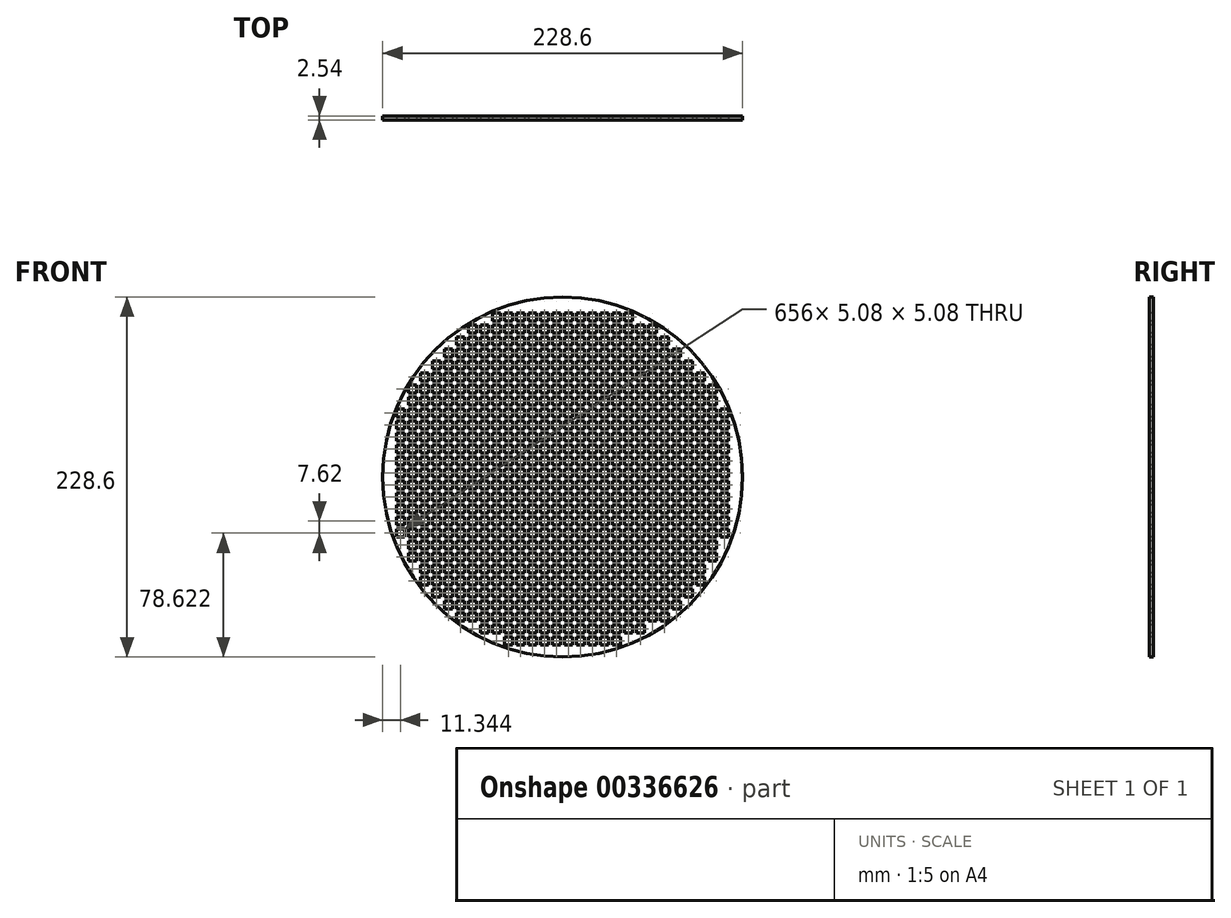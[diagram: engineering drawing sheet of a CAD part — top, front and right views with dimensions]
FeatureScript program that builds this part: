
annotation { "Feature Type Name" : "Feature", "Feature Type Description" : "" }
export const myFeature = defineFeature(function(context is Context, id is Id, definition is map)
    precondition{}
    {
        {
            var Q0;
            Q0=qCreatedBy(makeId("Front.planeOp"),FACE);
            var sketch = newSketch(context, id + "F0", { "sketchPlane" : qUnion([Q0])});
            skCircle(sketch, "E0", {"center": v(0, 0) * mm, "radius": 114.3 * mm});
            skSolve(sketch);
        }
        {
            var Q0;
            Q0=makeQuery(id+"F0.imprint","IMPRINT",FACE,{"disambiguationData":[TD([[makeQuery(id+"F0.imprint","IMPRINT",EDGE,{"derivedFrom":sQuery(id+"F0.wireOp",EDGE,"E0")}),1.0]])]});
            extrude(context, id + "F1", {"entities" : qUnion([Q0]), "depth" : 2.54 * mm});
        }
        {
            var Q0;
            Q0=makeQuery(id+"F1.opExtrude","CAP_FACE",FACE,{"disambiguationData":[OSD([sQuery(id+"F0.wireOp",EDGE,"E0")])],"isStart":false});
            var sketch = newSketch(context, id + "F2", { "sketchPlane" : qUnion([Q0])});
            skLineSegment(sketch, "E1.bottom", {"start": v(-67.4, 81.17) * mm, "end": v(-62.32, 81.17) * mm});
            skLineSegment(sketch, "E1.top", {"start": v(-67.4, 76.09) * mm, "end": v(-62.32, 76.09) * mm});
            skLineSegment(sketch, "E1.left", {"start": v(-67.4, 81.17) * mm, "end": v(-67.4, 76.09) * mm});
            skLineSegment(sketch, "E1.right", {"start": v(-62.32, 81.17) * mm, "end": v(-62.32, 76.09) * mm});
            skLineSegment(sketch, "E2.0.1.0", {"start": v(-67.4, 73.55) * mm, "end": v(-62.32, 73.55) * mm});
            skLineSegment(sketch, "E2.0.1.1", {"start": v(-67.4, 68.47) * mm, "end": v(-62.32, 68.47) * mm});
            skLineSegment(sketch, "E2.0.1.2", {"start": v(-67.4, 73.55) * mm, "end": v(-67.4, 68.47) * mm});
            skLineSegment(sketch, "E2.0.1.3", {"start": v(-62.32, 73.55) * mm, "end": v(-62.32, 68.47) * mm});
            skLineSegment(sketch, "E2.0.2.0", {"start": v(-67.4, 65.93) * mm, "end": v(-62.32, 65.93) * mm});
            skLineSegment(sketch, "E2.0.2.1", {"start": v(-67.4, 60.85) * mm, "end": v(-62.32, 60.85) * mm});
            skLineSegment(sketch, "E2.0.2.2", {"start": v(-67.4, 65.93) * mm, "end": v(-67.4, 60.85) * mm});
            skLineSegment(sketch, "E2.0.2.3", {"start": v(-62.32, 65.93) * mm, "end": v(-62.32, 60.85) * mm});
            skLineSegment(sketch, "E2.0.3.0", {"start": v(-67.4, 58.3) * mm, "end": v(-62.32, 58.3) * mm});
            skLineSegment(sketch, "E2.0.3.1", {"start": v(-67.4, 53.23) * mm, "end": v(-62.32, 53.23) * mm});
            skLineSegment(sketch, "E2.0.3.2", {"start": v(-67.4, 58.3) * mm, "end": v(-67.4, 53.23) * mm});
            skLineSegment(sketch, "E2.0.3.3", {"start": v(-62.32, 58.3) * mm, "end": v(-62.32, 53.23) * mm});
            skLineSegment(sketch, "E2.0.4.0", {"start": v(-67.4, 50.69) * mm, "end": v(-62.32, 50.69) * mm});
            skLineSegment(sketch, "E2.0.4.1", {"start": v(-67.4, 45.6) * mm, "end": v(-62.32, 45.6) * mm});
            skLineSegment(sketch, "E2.0.4.2", {"start": v(-67.4, 50.69) * mm, "end": v(-67.4, 45.6) * mm});
            skLineSegment(sketch, "E2.0.4.3", {"start": v(-62.32, 50.69) * mm, "end": v(-62.32, 45.6) * mm});
            skLineSegment(sketch, "E2.0.5.0", {"start": v(-67.4, 43.07) * mm, "end": v(-62.32, 43.07) * mm});
            skLineSegment(sketch, "E2.0.5.1", {"start": v(-67.4, 37.99) * mm, "end": v(-62.32, 37.99) * mm});
            skLineSegment(sketch, "E2.0.5.2", {"start": v(-67.4, 43.07) * mm, "end": v(-67.4, 37.99) * mm});
            skLineSegment(sketch, "E2.0.5.3", {"start": v(-62.32, 43.07) * mm, "end": v(-62.32, 37.99) * mm});
            skLineSegment(sketch, "E2.0.6.0", {"start": v(-67.4, 35.45) * mm, "end": v(-62.32, 35.45) * mm});
            skLineSegment(sketch, "E2.0.6.1", {"start": v(-67.4, 30.37) * mm, "end": v(-62.32, 30.37) * mm});
            skLineSegment(sketch, "E2.0.6.2", {"start": v(-67.4, 35.45) * mm, "end": v(-67.4, 30.37) * mm});
            skLineSegment(sketch, "E2.0.6.3", {"start": v(-62.32, 35.45) * mm, "end": v(-62.32, 30.37) * mm});
            skLineSegment(sketch, "E2.0.7.0", {"start": v(-67.4, 27.83) * mm, "end": v(-62.32, 27.83) * mm});
            skLineSegment(sketch, "E2.0.7.1", {"start": v(-67.4, 22.75) * mm, "end": v(-62.32, 22.75) * mm});
            skLineSegment(sketch, "E2.0.7.2", {"start": v(-67.4, 27.83) * mm, "end": v(-67.4, 22.75) * mm});
            skLineSegment(sketch, "E2.0.7.3", {"start": v(-62.32, 27.83) * mm, "end": v(-62.32, 22.75) * mm});
            skLineSegment(sketch, "E2.0.8.0", {"start": v(-67.4, 20.2) * mm, "end": v(-62.32, 20.2) * mm});
            skLineSegment(sketch, "E2.0.8.1", {"start": v(-67.4, 15.13) * mm, "end": v(-62.32, 15.13) * mm});
            skLineSegment(sketch, "E2.0.8.2", {"start": v(-67.4, 20.2) * mm, "end": v(-67.4, 15.13) * mm});
            skLineSegment(sketch, "E2.0.8.3", {"start": v(-62.32, 20.2) * mm, "end": v(-62.32, 15.13) * mm});
            skLineSegment(sketch, "E2.0.9.0", {"start": v(-67.4, 12.59) * mm, "end": v(-62.32, 12.59) * mm});
            skLineSegment(sketch, "E2.0.9.1", {"start": v(-67.4, 7.5) * mm, "end": v(-62.32, 7.5) * mm});
            skLineSegment(sketch, "E2.0.9.2", {"start": v(-67.4, 12.59) * mm, "end": v(-67.4, 7.5) * mm});
            skLineSegment(sketch, "E2.0.9.3", {"start": v(-62.32, 12.59) * mm, "end": v(-62.32, 7.5) * mm});
            skLineSegment(sketch, "E2.0.10.0", {"start": v(-67.4, 4.97) * mm, "end": v(-62.32, 4.97) * mm});
            skLineSegment(sketch, "E2.0.10.1", {"start": v(-67.4, -0.11) * mm, "end": v(-62.32, -0.11) * mm});
            skLineSegment(sketch, "E2.0.10.2", {"start": v(-67.4, 4.97) * mm, "end": v(-67.4, -0.11) * mm});
            skLineSegment(sketch, "E2.0.10.3", {"start": v(-62.32, 4.97) * mm, "end": v(-62.32, -0.11) * mm});
            skLineSegment(sketch, "E2.0.11.0", {"start": v(-67.4, -2.65) * mm, "end": v(-62.32, -2.65) * mm});
            skLineSegment(sketch, "E2.0.11.1", {"start": v(-67.4, -7.73) * mm, "end": v(-62.32, -7.73) * mm});
            skLineSegment(sketch, "E2.0.11.2", {"start": v(-67.4, -2.65) * mm, "end": v(-67.4, -7.73) * mm});
            skLineSegment(sketch, "E2.0.11.3", {"start": v(-62.32, -2.65) * mm, "end": v(-62.32, -7.73) * mm});
            skLineSegment(sketch, "E2.0.12.0", {"start": v(-67.4, -10.27) * mm, "end": v(-62.32, -10.27) * mm});
            skLineSegment(sketch, "E2.0.12.1", {"start": v(-67.4, -15.35) * mm, "end": v(-62.32, -15.35) * mm});
            skLineSegment(sketch, "E2.0.12.2", {"start": v(-67.4, -10.27) * mm, "end": v(-67.4, -15.35) * mm});
            skLineSegment(sketch, "E2.0.12.3", {"start": v(-62.32, -10.27) * mm, "end": v(-62.32, -15.35) * mm});
            skLineSegment(sketch, "E2.0.13.0", {"start": v(-67.4, -17.9) * mm, "end": v(-62.32, -17.9) * mm});
            skLineSegment(sketch, "E2.0.13.1", {"start": v(-67.4, -22.97) * mm, "end": v(-62.32, -22.97) * mm});
            skLineSegment(sketch, "E2.0.13.2", {"start": v(-67.4, -17.9) * mm, "end": v(-67.4, -22.97) * mm});
            skLineSegment(sketch, "E2.0.13.3", {"start": v(-62.32, -17.9) * mm, "end": v(-62.32, -22.97) * mm});
            skLineSegment(sketch, "E2.0.14.0", {"start": v(-67.4, -25.51) * mm, "end": v(-62.32, -25.51) * mm});
            skLineSegment(sketch, "E2.0.14.1", {"start": v(-67.4, -30.6) * mm, "end": v(-62.32, -30.6) * mm});
            skLineSegment(sketch, "E2.0.14.2", {"start": v(-67.4, -25.51) * mm, "end": v(-67.4, -30.6) * mm});
            skLineSegment(sketch, "E2.0.14.3", {"start": v(-62.32, -25.51) * mm, "end": v(-62.32, -30.6) * mm});
            skLineSegment(sketch, "E2.0.15.0", {"start": v(-67.4, -33.13) * mm, "end": v(-62.32, -33.13) * mm});
            skLineSegment(sketch, "E2.0.15.1", {"start": v(-67.4, -38.21) * mm, "end": v(-62.32, -38.21) * mm});
            skLineSegment(sketch, "E2.0.15.2", {"start": v(-67.4, -33.13) * mm, "end": v(-67.4, -38.21) * mm});
            skLineSegment(sketch, "E2.0.15.3", {"start": v(-62.32, -33.13) * mm, "end": v(-62.32, -38.21) * mm});
            skLineSegment(sketch, "E2.0.16.0", {"start": v(-67.4, -40.75) * mm, "end": v(-62.32, -40.75) * mm});
            skLineSegment(sketch, "E2.0.16.1", {"start": v(-67.4, -45.83) * mm, "end": v(-62.32, -45.83) * mm});
            skLineSegment(sketch, "E2.0.16.2", {"start": v(-67.4, -40.75) * mm, "end": v(-67.4, -45.83) * mm});
            skLineSegment(sketch, "E2.0.16.3", {"start": v(-62.32, -40.75) * mm, "end": v(-62.32, -45.83) * mm});
            skLineSegment(sketch, "E2.0.17.0", {"start": v(-67.4, -48.37) * mm, "end": v(-62.32, -48.37) * mm});
            skLineSegment(sketch, "E2.0.17.1", {"start": v(-67.4, -53.45) * mm, "end": v(-62.32, -53.45) * mm});
            skLineSegment(sketch, "E2.0.17.2", {"start": v(-67.4, -48.37) * mm, "end": v(-67.4, -53.45) * mm});
            skLineSegment(sketch, "E2.0.17.3", {"start": v(-62.32, -48.37) * mm, "end": v(-62.32, -53.45) * mm});
            skLineSegment(sketch, "E2.0.18.0", {"start": v(-67.4, -56) * mm, "end": v(-62.32, -56) * mm});
            skLineSegment(sketch, "E2.0.18.1", {"start": v(-67.4, -61.07) * mm, "end": v(-62.32, -61.07) * mm});
            skLineSegment(sketch, "E2.0.18.2", {"start": v(-67.4, -56) * mm, "end": v(-67.4, -61.07) * mm});
            skLineSegment(sketch, "E2.0.18.3", {"start": v(-62.32, -56) * mm, "end": v(-62.32, -61.07) * mm});
            skLineSegment(sketch, "E2.0.19.0", {"start": v(-67.4, -63.61) * mm, "end": v(-62.32, -63.61) * mm});
            skLineSegment(sketch, "E2.0.19.1", {"start": v(-67.4, -68.7) * mm, "end": v(-62.32, -68.7) * mm});
            skLineSegment(sketch, "E2.0.19.2", {"start": v(-67.4, -63.61) * mm, "end": v(-67.4, -68.7) * mm});
            skLineSegment(sketch, "E2.0.19.3", {"start": v(-62.32, -63.61) * mm, "end": v(-62.32, -68.7) * mm});
            skLineSegment(sketch, "E2.0.20.0", {"start": v(-67.4, -71.23) * mm, "end": v(-62.32, -71.23) * mm});
            skLineSegment(sketch, "E2.0.20.1", {"start": v(-67.4, -76.31) * mm, "end": v(-62.32, -76.31) * mm});
            skLineSegment(sketch, "E2.0.20.2", {"start": v(-67.4, -71.23) * mm, "end": v(-67.4, -76.31) * mm});
            skLineSegment(sketch, "E2.0.20.3", {"start": v(-62.32, -71.23) * mm, "end": v(-62.32, -76.31) * mm});
            skLineSegment(sketch, "E2.0.21.0", {"start": v(-67.4, -78.85) * mm, "end": v(-62.32, -78.85) * mm});
            skLineSegment(sketch, "E2.0.21.1", {"start": v(-67.4, -83.93) * mm, "end": v(-62.32, -83.93) * mm});
            skLineSegment(sketch, "E2.0.21.2", {"start": v(-67.4, -78.85) * mm, "end": v(-67.4, -83.93) * mm});
            skLineSegment(sketch, "E2.0.21.3", {"start": v(-62.32, -78.85) * mm, "end": v(-62.32, -83.93) * mm});
            skLineSegment(sketch, "E2.1.0.0", {"start": v(-59.78, 81.17) * mm, "end": v(-54.7, 81.17) * mm});
            skLineSegment(sketch, "E2.1.0.1", {"start": v(-59.78, 76.09) * mm, "end": v(-54.7, 76.09) * mm});
            skLineSegment(sketch, "E2.1.0.2", {"start": v(-59.78, 81.17) * mm, "end": v(-59.78, 76.09) * mm});
            skLineSegment(sketch, "E2.1.0.3", {"start": v(-54.7, 81.17) * mm, "end": v(-54.7, 76.09) * mm});
            skLineSegment(sketch, "E2.1.1.0", {"start": v(-59.78, 73.55) * mm, "end": v(-54.7, 73.55) * mm});
            skLineSegment(sketch, "E2.1.1.1", {"start": v(-59.78, 68.47) * mm, "end": v(-54.7, 68.47) * mm});
            skLineSegment(sketch, "E2.1.1.2", {"start": v(-59.78, 73.55) * mm, "end": v(-59.78, 68.47) * mm});
            skLineSegment(sketch, "E2.1.1.3", {"start": v(-54.7, 73.55) * mm, "end": v(-54.7, 68.47) * mm});
            skLineSegment(sketch, "E2.1.2.0", {"start": v(-59.78, 65.93) * mm, "end": v(-54.7, 65.93) * mm});
            skLineSegment(sketch, "E2.1.2.1", {"start": v(-59.78, 60.85) * mm, "end": v(-54.7, 60.85) * mm});
            skLineSegment(sketch, "E2.1.2.2", {"start": v(-59.78, 65.93) * mm, "end": v(-59.78, 60.85) * mm});
            skLineSegment(sketch, "E2.1.2.3", {"start": v(-54.7, 65.93) * mm, "end": v(-54.7, 60.85) * mm});
            skLineSegment(sketch, "E2.1.3.0", {"start": v(-59.78, 58.3) * mm, "end": v(-54.7, 58.3) * mm});
            skLineSegment(sketch, "E2.1.3.1", {"start": v(-59.78, 53.23) * mm, "end": v(-54.7, 53.23) * mm});
            skLineSegment(sketch, "E2.1.3.2", {"start": v(-59.78, 58.3) * mm, "end": v(-59.78, 53.23) * mm});
            skLineSegment(sketch, "E2.1.3.3", {"start": v(-54.7, 58.3) * mm, "end": v(-54.7, 53.23) * mm});
            skLineSegment(sketch, "E2.1.4.0", {"start": v(-59.78, 50.69) * mm, "end": v(-54.7, 50.69) * mm});
            skLineSegment(sketch, "E2.1.4.1", {"start": v(-59.78, 45.6) * mm, "end": v(-54.7, 45.6) * mm});
            skLineSegment(sketch, "E2.1.4.2", {"start": v(-59.78, 50.69) * mm, "end": v(-59.78, 45.6) * mm});
            skLineSegment(sketch, "E2.1.4.3", {"start": v(-54.7, 50.69) * mm, "end": v(-54.7, 45.6) * mm});
            skLineSegment(sketch, "E2.1.5.0", {"start": v(-59.78, 43.07) * mm, "end": v(-54.7, 43.07) * mm});
            skLineSegment(sketch, "E2.1.5.1", {"start": v(-59.78, 37.99) * mm, "end": v(-54.7, 37.99) * mm});
            skLineSegment(sketch, "E2.1.5.2", {"start": v(-59.78, 43.07) * mm, "end": v(-59.78, 37.99) * mm});
            skLineSegment(sketch, "E2.1.5.3", {"start": v(-54.7, 43.07) * mm, "end": v(-54.7, 37.99) * mm});
            skLineSegment(sketch, "E2.1.6.0", {"start": v(-59.78, 35.45) * mm, "end": v(-54.7, 35.45) * mm});
            skLineSegment(sketch, "E2.1.6.1", {"start": v(-59.78, 30.37) * mm, "end": v(-54.7, 30.37) * mm});
            skLineSegment(sketch, "E2.1.6.2", {"start": v(-59.78, 35.45) * mm, "end": v(-59.78, 30.37) * mm});
            skLineSegment(sketch, "E2.1.6.3", {"start": v(-54.7, 35.45) * mm, "end": v(-54.7, 30.37) * mm});
            skLineSegment(sketch, "E2.1.7.0", {"start": v(-59.78, 27.83) * mm, "end": v(-54.7, 27.83) * mm});
            skLineSegment(sketch, "E2.1.7.1", {"start": v(-59.78, 22.75) * mm, "end": v(-54.7, 22.75) * mm});
            skLineSegment(sketch, "E2.1.7.2", {"start": v(-59.78, 27.83) * mm, "end": v(-59.78, 22.75) * mm});
            skLineSegment(sketch, "E2.1.7.3", {"start": v(-54.7, 27.83) * mm, "end": v(-54.7, 22.75) * mm});
            skLineSegment(sketch, "E2.1.8.0", {"start": v(-59.78, 20.2) * mm, "end": v(-54.7, 20.2) * mm});
            skLineSegment(sketch, "E2.1.8.1", {"start": v(-59.78, 15.13) * mm, "end": v(-54.7, 15.13) * mm});
            skLineSegment(sketch, "E2.1.8.2", {"start": v(-59.78, 20.2) * mm, "end": v(-59.78, 15.13) * mm});
            skLineSegment(sketch, "E2.1.8.3", {"start": v(-54.7, 20.2) * mm, "end": v(-54.7, 15.13) * mm});
            skLineSegment(sketch, "E2.1.9.0", {"start": v(-59.78, 12.59) * mm, "end": v(-54.7, 12.59) * mm});
            skLineSegment(sketch, "E2.1.9.1", {"start": v(-59.78, 7.5) * mm, "end": v(-54.7, 7.5) * mm});
            skLineSegment(sketch, "E2.1.9.2", {"start": v(-59.78, 12.59) * mm, "end": v(-59.78, 7.5) * mm});
            skLineSegment(sketch, "E2.1.9.3", {"start": v(-54.7, 12.59) * mm, "end": v(-54.7, 7.5) * mm});
            skLineSegment(sketch, "E2.1.10.0", {"start": v(-59.78, 4.97) * mm, "end": v(-54.7, 4.97) * mm});
            skLineSegment(sketch, "E2.1.10.1", {"start": v(-59.78, -0.11) * mm, "end": v(-54.7, -0.11) * mm});
            skLineSegment(sketch, "E2.1.10.2", {"start": v(-59.78, 4.97) * mm, "end": v(-59.78, -0.11) * mm});
            skLineSegment(sketch, "E2.1.10.3", {"start": v(-54.7, 4.97) * mm, "end": v(-54.7, -0.11) * mm});
            skLineSegment(sketch, "E2.1.11.0", {"start": v(-59.78, -2.65) * mm, "end": v(-54.7, -2.65) * mm});
            skLineSegment(sketch, "E2.1.11.1", {"start": v(-59.78, -7.73) * mm, "end": v(-54.7, -7.73) * mm});
            skLineSegment(sketch, "E2.1.11.2", {"start": v(-59.78, -2.65) * mm, "end": v(-59.78, -7.73) * mm});
            skLineSegment(sketch, "E2.1.11.3", {"start": v(-54.7, -2.65) * mm, "end": v(-54.7, -7.73) * mm});
            skLineSegment(sketch, "E2.1.12.0", {"start": v(-59.78, -10.27) * mm, "end": v(-54.7, -10.27) * mm});
            skLineSegment(sketch, "E2.1.12.1", {"start": v(-59.78, -15.35) * mm, "end": v(-54.7, -15.35) * mm});
            skLineSegment(sketch, "E2.1.12.2", {"start": v(-59.78, -10.27) * mm, "end": v(-59.78, -15.35) * mm});
            skLineSegment(sketch, "E2.1.12.3", {"start": v(-54.7, -10.27) * mm, "end": v(-54.7, -15.35) * mm});
            skLineSegment(sketch, "E2.1.13.0", {"start": v(-59.78, -17.9) * mm, "end": v(-54.7, -17.9) * mm});
            skLineSegment(sketch, "E2.1.13.1", {"start": v(-59.78, -22.97) * mm, "end": v(-54.7, -22.97) * mm});
            skLineSegment(sketch, "E2.1.13.2", {"start": v(-59.78, -17.9) * mm, "end": v(-59.78, -22.97) * mm});
            skLineSegment(sketch, "E2.1.13.3", {"start": v(-54.7, -17.9) * mm, "end": v(-54.7, -22.97) * mm});
            skLineSegment(sketch, "E2.1.14.0", {"start": v(-59.78, -25.51) * mm, "end": v(-54.7, -25.51) * mm});
            skLineSegment(sketch, "E2.1.14.1", {"start": v(-59.78, -30.6) * mm, "end": v(-54.7, -30.6) * mm});
            skLineSegment(sketch, "E2.1.14.2", {"start": v(-59.78, -25.51) * mm, "end": v(-59.78, -30.6) * mm});
            skLineSegment(sketch, "E2.1.14.3", {"start": v(-54.7, -25.51) * mm, "end": v(-54.7, -30.6) * mm});
            skLineSegment(sketch, "E2.1.15.0", {"start": v(-59.78, -33.13) * mm, "end": v(-54.7, -33.13) * mm});
            skLineSegment(sketch, "E2.1.15.1", {"start": v(-59.78, -38.21) * mm, "end": v(-54.7, -38.21) * mm});
            skLineSegment(sketch, "E2.1.15.2", {"start": v(-59.78, -33.13) * mm, "end": v(-59.78, -38.21) * mm});
            skLineSegment(sketch, "E2.1.15.3", {"start": v(-54.7, -33.13) * mm, "end": v(-54.7, -38.21) * mm});
            skLineSegment(sketch, "E2.1.16.0", {"start": v(-59.78, -40.75) * mm, "end": v(-54.7, -40.75) * mm});
            skLineSegment(sketch, "E2.1.16.1", {"start": v(-59.78, -45.83) * mm, "end": v(-54.7, -45.83) * mm});
            skLineSegment(sketch, "E2.1.16.2", {"start": v(-59.78, -40.75) * mm, "end": v(-59.78, -45.83) * mm});
            skLineSegment(sketch, "E2.1.16.3", {"start": v(-54.7, -40.75) * mm, "end": v(-54.7, -45.83) * mm});
            skLineSegment(sketch, "E2.1.17.0", {"start": v(-59.78, -48.37) * mm, "end": v(-54.7, -48.37) * mm});
            skLineSegment(sketch, "E2.1.17.1", {"start": v(-59.78, -53.45) * mm, "end": v(-54.7, -53.45) * mm});
            skLineSegment(sketch, "E2.1.17.2", {"start": v(-59.78, -48.37) * mm, "end": v(-59.78, -53.45) * mm});
            skLineSegment(sketch, "E2.1.17.3", {"start": v(-54.7, -48.37) * mm, "end": v(-54.7, -53.45) * mm});
            skLineSegment(sketch, "E2.1.18.0", {"start": v(-59.78, -56) * mm, "end": v(-54.7, -56) * mm});
            skLineSegment(sketch, "E2.1.18.1", {"start": v(-59.78, -61.07) * mm, "end": v(-54.7, -61.07) * mm});
            skLineSegment(sketch, "E2.1.18.2", {"start": v(-59.78, -56) * mm, "end": v(-59.78, -61.07) * mm});
            skLineSegment(sketch, "E2.1.18.3", {"start": v(-54.7, -56) * mm, "end": v(-54.7, -61.07) * mm});
            skLineSegment(sketch, "E2.1.19.0", {"start": v(-59.78, -63.61) * mm, "end": v(-54.7, -63.61) * mm});
            skLineSegment(sketch, "E2.1.19.1", {"start": v(-59.78, -68.7) * mm, "end": v(-54.7, -68.7) * mm});
            skLineSegment(sketch, "E2.1.19.2", {"start": v(-59.78, -63.61) * mm, "end": v(-59.78, -68.7) * mm});
            skLineSegment(sketch, "E2.1.19.3", {"start": v(-54.7, -63.61) * mm, "end": v(-54.7, -68.7) * mm});
            skLineSegment(sketch, "E2.1.20.0", {"start": v(-59.78, -71.23) * mm, "end": v(-54.7, -71.23) * mm});
            skLineSegment(sketch, "E2.1.20.1", {"start": v(-59.78, -76.31) * mm, "end": v(-54.7, -76.31) * mm});
            skLineSegment(sketch, "E2.1.20.2", {"start": v(-59.78, -71.23) * mm, "end": v(-59.78, -76.31) * mm});
            skLineSegment(sketch, "E2.1.20.3", {"start": v(-54.7, -71.23) * mm, "end": v(-54.7, -76.31) * mm});
            skLineSegment(sketch, "E2.1.21.0", {"start": v(-59.78, -78.85) * mm, "end": v(-54.7, -78.85) * mm});
            skLineSegment(sketch, "E2.1.21.1", {"start": v(-59.78, -83.93) * mm, "end": v(-54.7, -83.93) * mm});
            skLineSegment(sketch, "E2.1.21.2", {"start": v(-59.78, -78.85) * mm, "end": v(-59.78, -83.93) * mm});
            skLineSegment(sketch, "E2.1.21.3", {"start": v(-54.7, -78.85) * mm, "end": v(-54.7, -83.93) * mm});
            skLineSegment(sketch, "E2.2.0.0", {"start": v(-52.16, 81.17) * mm, "end": v(-47.08, 81.17) * mm});
            skLineSegment(sketch, "E2.2.0.1", {"start": v(-52.16, 76.09) * mm, "end": v(-47.08, 76.09) * mm});
            skLineSegment(sketch, "E2.2.0.2", {"start": v(-52.16, 81.17) * mm, "end": v(-52.16, 76.09) * mm});
            skLineSegment(sketch, "E2.2.0.3", {"start": v(-47.08, 81.17) * mm, "end": v(-47.08, 76.09) * mm});
            skLineSegment(sketch, "E2.2.1.0", {"start": v(-52.16, 73.55) * mm, "end": v(-47.08, 73.55) * mm});
            skLineSegment(sketch, "E2.2.1.1", {"start": v(-52.16, 68.47) * mm, "end": v(-47.08, 68.47) * mm});
            skLineSegment(sketch, "E2.2.1.2", {"start": v(-52.16, 73.55) * mm, "end": v(-52.16, 68.47) * mm});
            skLineSegment(sketch, "E2.2.1.3", {"start": v(-47.08, 73.55) * mm, "end": v(-47.08, 68.47) * mm});
            skLineSegment(sketch, "E2.2.2.0", {"start": v(-52.16, 65.93) * mm, "end": v(-47.08, 65.93) * mm});
            skLineSegment(sketch, "E2.2.2.1", {"start": v(-52.16, 60.85) * mm, "end": v(-47.08, 60.85) * mm});
            skLineSegment(sketch, "E2.2.2.2", {"start": v(-52.16, 65.93) * mm, "end": v(-52.16, 60.85) * mm});
            skLineSegment(sketch, "E2.2.2.3", {"start": v(-47.08, 65.93) * mm, "end": v(-47.08, 60.85) * mm});
            skLineSegment(sketch, "E2.2.3.0", {"start": v(-52.16, 58.3) * mm, "end": v(-47.08, 58.3) * mm});
            skLineSegment(sketch, "E2.2.3.1", {"start": v(-52.16, 53.23) * mm, "end": v(-47.08, 53.23) * mm});
            skLineSegment(sketch, "E2.2.3.2", {"start": v(-52.16, 58.3) * mm, "end": v(-52.16, 53.23) * mm});
            skLineSegment(sketch, "E2.2.3.3", {"start": v(-47.08, 58.3) * mm, "end": v(-47.08, 53.23) * mm});
            skLineSegment(sketch, "E2.2.4.0", {"start": v(-52.16, 50.69) * mm, "end": v(-47.08, 50.69) * mm});
            skLineSegment(sketch, "E2.2.4.1", {"start": v(-52.16, 45.6) * mm, "end": v(-47.08, 45.6) * mm});
            skLineSegment(sketch, "E2.2.4.2", {"start": v(-52.16, 50.69) * mm, "end": v(-52.16, 45.6) * mm});
            skLineSegment(sketch, "E2.2.4.3", {"start": v(-47.08, 50.69) * mm, "end": v(-47.08, 45.6) * mm});
            skLineSegment(sketch, "E2.2.5.0", {"start": v(-52.16, 43.07) * mm, "end": v(-47.08, 43.07) * mm});
            skLineSegment(sketch, "E2.2.5.1", {"start": v(-52.16, 37.99) * mm, "end": v(-47.08, 37.99) * mm});
            skLineSegment(sketch, "E2.2.5.2", {"start": v(-52.16, 43.07) * mm, "end": v(-52.16, 37.99) * mm});
            skLineSegment(sketch, "E2.2.5.3", {"start": v(-47.08, 43.07) * mm, "end": v(-47.08, 37.99) * mm});
            skLineSegment(sketch, "E2.2.6.0", {"start": v(-52.16, 35.45) * mm, "end": v(-47.08, 35.45) * mm});
            skLineSegment(sketch, "E2.2.6.1", {"start": v(-52.16, 30.37) * mm, "end": v(-47.08, 30.37) * mm});
            skLineSegment(sketch, "E2.2.6.2", {"start": v(-52.16, 35.45) * mm, "end": v(-52.16, 30.37) * mm});
            skLineSegment(sketch, "E2.2.6.3", {"start": v(-47.08, 35.45) * mm, "end": v(-47.08, 30.37) * mm});
            skLineSegment(sketch, "E2.2.7.0", {"start": v(-52.16, 27.83) * mm, "end": v(-47.08, 27.83) * mm});
            skLineSegment(sketch, "E2.2.7.1", {"start": v(-52.16, 22.75) * mm, "end": v(-47.08, 22.75) * mm});
            skLineSegment(sketch, "E2.2.7.2", {"start": v(-52.16, 27.83) * mm, "end": v(-52.16, 22.75) * mm});
            skLineSegment(sketch, "E2.2.7.3", {"start": v(-47.08, 27.83) * mm, "end": v(-47.08, 22.75) * mm});
            skLineSegment(sketch, "E2.2.8.0", {"start": v(-52.16, 20.2) * mm, "end": v(-47.08, 20.2) * mm});
            skLineSegment(sketch, "E2.2.8.1", {"start": v(-52.16, 15.13) * mm, "end": v(-47.08, 15.13) * mm});
            skLineSegment(sketch, "E2.2.8.2", {"start": v(-52.16, 20.2) * mm, "end": v(-52.16, 15.13) * mm});
            skLineSegment(sketch, "E2.2.8.3", {"start": v(-47.08, 20.2) * mm, "end": v(-47.08, 15.13) * mm});
            skLineSegment(sketch, "E2.2.9.0", {"start": v(-52.16, 12.59) * mm, "end": v(-47.08, 12.59) * mm});
            skLineSegment(sketch, "E2.2.9.1", {"start": v(-52.16, 7.5) * mm, "end": v(-47.08, 7.5) * mm});
            skLineSegment(sketch, "E2.2.9.2", {"start": v(-52.16, 12.59) * mm, "end": v(-52.16, 7.5) * mm});
            skLineSegment(sketch, "E2.2.9.3", {"start": v(-47.08, 12.59) * mm, "end": v(-47.08, 7.5) * mm});
            skLineSegment(sketch, "E2.2.10.0", {"start": v(-52.16, 4.97) * mm, "end": v(-47.08, 4.97) * mm});
            skLineSegment(sketch, "E2.2.10.1", {"start": v(-52.16, -0.11) * mm, "end": v(-47.08, -0.11) * mm});
            skLineSegment(sketch, "E2.2.10.2", {"start": v(-52.16, 4.97) * mm, "end": v(-52.16, -0.11) * mm});
            skLineSegment(sketch, "E2.2.10.3", {"start": v(-47.08, 4.97) * mm, "end": v(-47.08, -0.11) * mm});
            skLineSegment(sketch, "E2.2.11.0", {"start": v(-52.16, -2.65) * mm, "end": v(-47.08, -2.65) * mm});
            skLineSegment(sketch, "E2.2.11.1", {"start": v(-52.16, -7.73) * mm, "end": v(-47.08, -7.73) * mm});
            skLineSegment(sketch, "E2.2.11.2", {"start": v(-52.16, -2.65) * mm, "end": v(-52.16, -7.73) * mm});
            skLineSegment(sketch, "E2.2.11.3", {"start": v(-47.08, -2.65) * mm, "end": v(-47.08, -7.73) * mm});
            skLineSegment(sketch, "E2.2.12.0", {"start": v(-52.16, -10.27) * mm, "end": v(-47.08, -10.27) * mm});
            skLineSegment(sketch, "E2.2.12.1", {"start": v(-52.16, -15.35) * mm, "end": v(-47.08, -15.35) * mm});
            skLineSegment(sketch, "E2.2.12.2", {"start": v(-52.16, -10.27) * mm, "end": v(-52.16, -15.35) * mm});
            skLineSegment(sketch, "E2.2.12.3", {"start": v(-47.08, -10.27) * mm, "end": v(-47.08, -15.35) * mm});
            skLineSegment(sketch, "E2.2.13.0", {"start": v(-52.16, -17.9) * mm, "end": v(-47.08, -17.9) * mm});
            skLineSegment(sketch, "E2.2.13.1", {"start": v(-52.16, -22.97) * mm, "end": v(-47.08, -22.97) * mm});
            skLineSegment(sketch, "E2.2.13.2", {"start": v(-52.16, -17.9) * mm, "end": v(-52.16, -22.97) * mm});
            skLineSegment(sketch, "E2.2.13.3", {"start": v(-47.08, -17.9) * mm, "end": v(-47.08, -22.97) * mm});
            skLineSegment(sketch, "E2.2.14.0", {"start": v(-52.16, -25.51) * mm, "end": v(-47.08, -25.51) * mm});
            skLineSegment(sketch, "E2.2.14.1", {"start": v(-52.16, -30.6) * mm, "end": v(-47.08, -30.6) * mm});
            skLineSegment(sketch, "E2.2.14.2", {"start": v(-52.16, -25.51) * mm, "end": v(-52.16, -30.6) * mm});
            skLineSegment(sketch, "E2.2.14.3", {"start": v(-47.08, -25.51) * mm, "end": v(-47.08, -30.6) * mm});
            skLineSegment(sketch, "E2.2.15.0", {"start": v(-52.16, -33.13) * mm, "end": v(-47.08, -33.13) * mm});
            skLineSegment(sketch, "E2.2.15.1", {"start": v(-52.16, -38.21) * mm, "end": v(-47.08, -38.21) * mm});
            skLineSegment(sketch, "E2.2.15.2", {"start": v(-52.16, -33.13) * mm, "end": v(-52.16, -38.21) * mm});
            skLineSegment(sketch, "E2.2.15.3", {"start": v(-47.08, -33.13) * mm, "end": v(-47.08, -38.21) * mm});
            skLineSegment(sketch, "E2.2.16.0", {"start": v(-52.16, -40.75) * mm, "end": v(-47.08, -40.75) * mm});
            skLineSegment(sketch, "E2.2.16.1", {"start": v(-52.16, -45.83) * mm, "end": v(-47.08, -45.83) * mm});
            skLineSegment(sketch, "E2.2.16.2", {"start": v(-52.16, -40.75) * mm, "end": v(-52.16, -45.83) * mm});
            skLineSegment(sketch, "E2.2.16.3", {"start": v(-47.08, -40.75) * mm, "end": v(-47.08, -45.83) * mm});
            skLineSegment(sketch, "E2.2.17.0", {"start": v(-52.16, -48.37) * mm, "end": v(-47.08, -48.37) * mm});
            skLineSegment(sketch, "E2.2.17.1", {"start": v(-52.16, -53.45) * mm, "end": v(-47.08, -53.45) * mm});
            skLineSegment(sketch, "E2.2.17.2", {"start": v(-52.16, -48.37) * mm, "end": v(-52.16, -53.45) * mm});
            skLineSegment(sketch, "E2.2.17.3", {"start": v(-47.08, -48.37) * mm, "end": v(-47.08, -53.45) * mm});
            skLineSegment(sketch, "E2.2.18.0", {"start": v(-52.16, -56) * mm, "end": v(-47.08, -56) * mm});
            skLineSegment(sketch, "E2.2.18.1", {"start": v(-52.16, -61.07) * mm, "end": v(-47.08, -61.07) * mm});
            skLineSegment(sketch, "E2.2.18.2", {"start": v(-52.16, -56) * mm, "end": v(-52.16, -61.07) * mm});
            skLineSegment(sketch, "E2.2.18.3", {"start": v(-47.08, -56) * mm, "end": v(-47.08, -61.07) * mm});
            skLineSegment(sketch, "E2.2.19.0", {"start": v(-52.16, -63.61) * mm, "end": v(-47.08, -63.61) * mm});
            skLineSegment(sketch, "E2.2.19.1", {"start": v(-52.16, -68.7) * mm, "end": v(-47.08, -68.7) * mm});
            skLineSegment(sketch, "E2.2.19.2", {"start": v(-52.16, -63.61) * mm, "end": v(-52.16, -68.7) * mm});
            skLineSegment(sketch, "E2.2.19.3", {"start": v(-47.08, -63.61) * mm, "end": v(-47.08, -68.7) * mm});
            skLineSegment(sketch, "E2.2.20.0", {"start": v(-52.16, -71.23) * mm, "end": v(-47.08, -71.23) * mm});
            skLineSegment(sketch, "E2.2.20.1", {"start": v(-52.16, -76.31) * mm, "end": v(-47.08, -76.31) * mm});
            skLineSegment(sketch, "E2.2.20.2", {"start": v(-52.16, -71.23) * mm, "end": v(-52.16, -76.31) * mm});
            skLineSegment(sketch, "E2.2.20.3", {"start": v(-47.08, -71.23) * mm, "end": v(-47.08, -76.31) * mm});
            skLineSegment(sketch, "E2.2.21.0", {"start": v(-52.16, -78.85) * mm, "end": v(-47.08, -78.85) * mm});
            skLineSegment(sketch, "E2.2.21.1", {"start": v(-52.16, -83.93) * mm, "end": v(-47.08, -83.93) * mm});
            skLineSegment(sketch, "E2.2.21.2", {"start": v(-52.16, -78.85) * mm, "end": v(-52.16, -83.93) * mm});
            skLineSegment(sketch, "E2.2.21.3", {"start": v(-47.08, -78.85) * mm, "end": v(-47.08, -83.93) * mm});
            skLineSegment(sketch, "E2.direction1", {"start": v(-67.4, 81.17) * mm, "end": v(-59.78, 81.17) * mm, "construction": true});
            skLineSegment(sketch, "E2.direction2", {"start": v(-67.4, 81.17) * mm, "end": v(-67.4, 73.55) * mm, "construction": true});
            skLineSegment(sketch, "E3.0.3.0", {"start": v(-44.54, 81.17) * mm, "end": v(-39.46, 81.17) * mm});
            skLineSegment(sketch, "E3.3.3.0", {"start": v(-44.54, 76.09) * mm, "end": v(-39.46, 76.09) * mm});
            skLineSegment(sketch, "E3.6.3.0", {"start": v(-44.54, 81.17) * mm, "end": v(-44.54, 76.09) * mm});
            skLineSegment(sketch, "E3.9.3.0", {"start": v(-39.46, 81.17) * mm, "end": v(-39.46, 76.09) * mm});
            skLineSegment(sketch, "E3.0.3.1", {"start": v(-44.54, 73.55) * mm, "end": v(-39.46, 73.55) * mm});
            skLineSegment(sketch, "E3.3.3.1", {"start": v(-44.54, 68.47) * mm, "end": v(-39.46, 68.47) * mm});
            skLineSegment(sketch, "E3.6.3.1", {"start": v(-44.54, 73.55) * mm, "end": v(-44.54, 68.47) * mm});
            skLineSegment(sketch, "E3.9.3.1", {"start": v(-39.46, 73.55) * mm, "end": v(-39.46, 68.47) * mm});
            skLineSegment(sketch, "E3.0.3.2", {"start": v(-44.54, 65.93) * mm, "end": v(-39.46, 65.93) * mm});
            skLineSegment(sketch, "E3.3.3.2", {"start": v(-44.54, 60.85) * mm, "end": v(-39.46, 60.85) * mm});
            skLineSegment(sketch, "E3.6.3.2", {"start": v(-44.54, 65.93) * mm, "end": v(-44.54, 60.85) * mm});
            skLineSegment(sketch, "E3.9.3.2", {"start": v(-39.46, 65.93) * mm, "end": v(-39.46, 60.85) * mm});
            skLineSegment(sketch, "E3.0.3.3", {"start": v(-44.54, 58.3) * mm, "end": v(-39.46, 58.3) * mm});
            skLineSegment(sketch, "E3.3.3.3", {"start": v(-44.54, 53.23) * mm, "end": v(-39.46, 53.23) * mm});
            skLineSegment(sketch, "E3.6.3.3", {"start": v(-44.54, 58.3) * mm, "end": v(-44.54, 53.23) * mm});
            skLineSegment(sketch, "E3.9.3.3", {"start": v(-39.46, 58.3) * mm, "end": v(-39.46, 53.23) * mm});
            skLineSegment(sketch, "E3.0.3.4", {"start": v(-44.54, 50.69) * mm, "end": v(-39.46, 50.69) * mm});
            skLineSegment(sketch, "E3.3.3.4", {"start": v(-44.54, 45.6) * mm, "end": v(-39.46, 45.6) * mm});
            skLineSegment(sketch, "E3.6.3.4", {"start": v(-44.54, 50.69) * mm, "end": v(-44.54, 45.6) * mm});
            skLineSegment(sketch, "E3.9.3.4", {"start": v(-39.46, 50.69) * mm, "end": v(-39.46, 45.6) * mm});
            skLineSegment(sketch, "E3.0.3.5", {"start": v(-44.54, 43.07) * mm, "end": v(-39.46, 43.07) * mm});
            skLineSegment(sketch, "E3.3.3.5", {"start": v(-44.54, 37.99) * mm, "end": v(-39.46, 37.99) * mm});
            skLineSegment(sketch, "E3.6.3.5", {"start": v(-44.54, 43.07) * mm, "end": v(-44.54, 37.99) * mm});
            skLineSegment(sketch, "E3.9.3.5", {"start": v(-39.46, 43.07) * mm, "end": v(-39.46, 37.99) * mm});
            skLineSegment(sketch, "E3.0.3.6", {"start": v(-44.54, 35.45) * mm, "end": v(-39.46, 35.45) * mm});
            skLineSegment(sketch, "E3.3.3.6", {"start": v(-44.54, 30.37) * mm, "end": v(-39.46, 30.37) * mm});
            skLineSegment(sketch, "E3.6.3.6", {"start": v(-44.54, 35.45) * mm, "end": v(-44.54, 30.37) * mm});
            skLineSegment(sketch, "E3.9.3.6", {"start": v(-39.46, 35.45) * mm, "end": v(-39.46, 30.37) * mm});
            skLineSegment(sketch, "E3.0.3.7", {"start": v(-44.54, 27.83) * mm, "end": v(-39.46, 27.83) * mm});
            skLineSegment(sketch, "E3.3.3.7", {"start": v(-44.54, 22.75) * mm, "end": v(-39.46, 22.75) * mm});
            skLineSegment(sketch, "E3.6.3.7", {"start": v(-44.54, 27.83) * mm, "end": v(-44.54, 22.75) * mm});
            skLineSegment(sketch, "E3.9.3.7", {"start": v(-39.46, 27.83) * mm, "end": v(-39.46, 22.75) * mm});
            skLineSegment(sketch, "E3.0.3.8", {"start": v(-44.54, 20.2) * mm, "end": v(-39.46, 20.2) * mm});
            skLineSegment(sketch, "E3.3.3.8", {"start": v(-44.54, 15.13) * mm, "end": v(-39.46, 15.13) * mm});
            skLineSegment(sketch, "E3.6.3.8", {"start": v(-44.54, 20.2) * mm, "end": v(-44.54, 15.13) * mm});
            skLineSegment(sketch, "E3.9.3.8", {"start": v(-39.46, 20.2) * mm, "end": v(-39.46, 15.13) * mm});
            skLineSegment(sketch, "E3.0.3.9", {"start": v(-44.54, 12.59) * mm, "end": v(-39.46, 12.59) * mm});
            skLineSegment(sketch, "E3.3.3.9", {"start": v(-44.54, 7.5) * mm, "end": v(-39.46, 7.5) * mm});
            skLineSegment(sketch, "E3.6.3.9", {"start": v(-44.54, 12.59) * mm, "end": v(-44.54, 7.5) * mm});
            skLineSegment(sketch, "E3.9.3.9", {"start": v(-39.46, 12.59) * mm, "end": v(-39.46, 7.5) * mm});
            skLineSegment(sketch, "E3.0.3.10", {"start": v(-44.54, 4.97) * mm, "end": v(-39.46, 4.97) * mm});
            skLineSegment(sketch, "E3.3.3.10", {"start": v(-44.54, -0.11) * mm, "end": v(-39.46, -0.11) * mm});
            skLineSegment(sketch, "E3.6.3.10", {"start": v(-44.54, 4.97) * mm, "end": v(-44.54, -0.11) * mm});
            skLineSegment(sketch, "E3.9.3.10", {"start": v(-39.46, 4.97) * mm, "end": v(-39.46, -0.11) * mm});
            skLineSegment(sketch, "E3.0.3.11", {"start": v(-44.54, -2.65) * mm, "end": v(-39.46, -2.65) * mm});
            skLineSegment(sketch, "E3.3.3.11", {"start": v(-44.54, -7.73) * mm, "end": v(-39.46, -7.73) * mm});
            skLineSegment(sketch, "E3.6.3.11", {"start": v(-44.54, -2.65) * mm, "end": v(-44.54, -7.73) * mm});
            skLineSegment(sketch, "E3.9.3.11", {"start": v(-39.46, -2.65) * mm, "end": v(-39.46, -7.73) * mm});
            skLineSegment(sketch, "E3.0.3.12", {"start": v(-44.54, -10.27) * mm, "end": v(-39.46, -10.27) * mm});
            skLineSegment(sketch, "E3.3.3.12", {"start": v(-44.54, -15.35) * mm, "end": v(-39.46, -15.35) * mm});
            skLineSegment(sketch, "E3.6.3.12", {"start": v(-44.54, -10.27) * mm, "end": v(-44.54, -15.35) * mm});
            skLineSegment(sketch, "E3.9.3.12", {"start": v(-39.46, -10.27) * mm, "end": v(-39.46, -15.35) * mm});
            skLineSegment(sketch, "E3.0.3.13", {"start": v(-44.54, -17.9) * mm, "end": v(-39.46, -17.9) * mm});
            skLineSegment(sketch, "E3.3.3.13", {"start": v(-44.54, -22.97) * mm, "end": v(-39.46, -22.97) * mm});
            skLineSegment(sketch, "E3.6.3.13", {"start": v(-44.54, -17.9) * mm, "end": v(-44.54, -22.97) * mm});
            skLineSegment(sketch, "E3.9.3.13", {"start": v(-39.46, -17.9) * mm, "end": v(-39.46, -22.97) * mm});
            skLineSegment(sketch, "E3.0.3.14", {"start": v(-44.54, -25.51) * mm, "end": v(-39.46, -25.51) * mm});
            skLineSegment(sketch, "E3.3.3.14", {"start": v(-44.54, -30.6) * mm, "end": v(-39.46, -30.6) * mm});
            skLineSegment(sketch, "E3.6.3.14", {"start": v(-44.54, -25.51) * mm, "end": v(-44.54, -30.6) * mm});
            skLineSegment(sketch, "E3.9.3.14", {"start": v(-39.46, -25.51) * mm, "end": v(-39.46, -30.6) * mm});
            skLineSegment(sketch, "E3.0.3.15", {"start": v(-44.54, -33.13) * mm, "end": v(-39.46, -33.13) * mm});
            skLineSegment(sketch, "E3.3.3.15", {"start": v(-44.54, -38.21) * mm, "end": v(-39.46, -38.21) * mm});
            skLineSegment(sketch, "E3.6.3.15", {"start": v(-44.54, -33.13) * mm, "end": v(-44.54, -38.21) * mm});
            skLineSegment(sketch, "E3.9.3.15", {"start": v(-39.46, -33.13) * mm, "end": v(-39.46, -38.21) * mm});
            skLineSegment(sketch, "E3.0.3.16", {"start": v(-44.54, -40.75) * mm, "end": v(-39.46, -40.75) * mm});
            skLineSegment(sketch, "E3.3.3.16", {"start": v(-44.54, -45.83) * mm, "end": v(-39.46, -45.83) * mm});
            skLineSegment(sketch, "E3.6.3.16", {"start": v(-44.54, -40.75) * mm, "end": v(-44.54, -45.83) * mm});
            skLineSegment(sketch, "E3.9.3.16", {"start": v(-39.46, -40.75) * mm, "end": v(-39.46, -45.83) * mm});
            skLineSegment(sketch, "E3.0.3.17", {"start": v(-44.54, -48.37) * mm, "end": v(-39.46, -48.37) * mm});
            skLineSegment(sketch, "E3.3.3.17", {"start": v(-44.54, -53.45) * mm, "end": v(-39.46, -53.45) * mm});
            skLineSegment(sketch, "E3.6.3.17", {"start": v(-44.54, -48.37) * mm, "end": v(-44.54, -53.45) * mm});
            skLineSegment(sketch, "E3.9.3.17", {"start": v(-39.46, -48.37) * mm, "end": v(-39.46, -53.45) * mm});
            skLineSegment(sketch, "E3.0.3.18", {"start": v(-44.54, -56) * mm, "end": v(-39.46, -56) * mm});
            skLineSegment(sketch, "E3.3.3.18", {"start": v(-44.54, -61.07) * mm, "end": v(-39.46, -61.07) * mm});
            skLineSegment(sketch, "E3.6.3.18", {"start": v(-44.54, -56) * mm, "end": v(-44.54, -61.07) * mm});
            skLineSegment(sketch, "E3.9.3.18", {"start": v(-39.46, -56) * mm, "end": v(-39.46, -61.07) * mm});
            skLineSegment(sketch, "E3.0.3.19", {"start": v(-44.54, -63.61) * mm, "end": v(-39.46, -63.61) * mm});
            skLineSegment(sketch, "E3.3.3.19", {"start": v(-44.54, -68.7) * mm, "end": v(-39.46, -68.7) * mm});
            skLineSegment(sketch, "E3.6.3.19", {"start": v(-44.54, -63.61) * mm, "end": v(-44.54, -68.7) * mm});
            skLineSegment(sketch, "E3.9.3.19", {"start": v(-39.46, -63.61) * mm, "end": v(-39.46, -68.7) * mm});
            skLineSegment(sketch, "E3.0.3.20", {"start": v(-44.54, -71.23) * mm, "end": v(-39.46, -71.23) * mm});
            skLineSegment(sketch, "E3.3.3.20", {"start": v(-44.54, -76.31) * mm, "end": v(-39.46, -76.31) * mm});
            skLineSegment(sketch, "E3.6.3.20", {"start": v(-44.54, -71.23) * mm, "end": v(-44.54, -76.31) * mm});
            skLineSegment(sketch, "E3.9.3.20", {"start": v(-39.46, -71.23) * mm, "end": v(-39.46, -76.31) * mm});
            skLineSegment(sketch, "E3.0.3.21", {"start": v(-44.54, -78.85) * mm, "end": v(-39.46, -78.85) * mm});
            skLineSegment(sketch, "E3.3.3.21", {"start": v(-44.54, -83.93) * mm, "end": v(-39.46, -83.93) * mm});
            skLineSegment(sketch, "E3.6.3.21", {"start": v(-44.54, -78.85) * mm, "end": v(-44.54, -83.93) * mm});
            skLineSegment(sketch, "E3.9.3.21", {"start": v(-39.46, -78.85) * mm, "end": v(-39.46, -83.93) * mm});
            skLineSegment(sketch, "E3.0.4.0", {"start": v(-36.92, 81.17) * mm, "end": v(-31.84, 81.17) * mm});
            skLineSegment(sketch, "E3.3.4.0", {"start": v(-36.92, 76.09) * mm, "end": v(-31.84, 76.09) * mm});
            skLineSegment(sketch, "E3.6.4.0", {"start": v(-36.92, 81.17) * mm, "end": v(-36.92, 76.09) * mm});
            skLineSegment(sketch, "E3.9.4.0", {"start": v(-31.84, 81.17) * mm, "end": v(-31.84, 76.09) * mm});
            skLineSegment(sketch, "E3.0.4.1", {"start": v(-36.92, 73.55) * mm, "end": v(-31.84, 73.55) * mm});
            skLineSegment(sketch, "E3.3.4.1", {"start": v(-36.92, 68.47) * mm, "end": v(-31.84, 68.47) * mm});
            skLineSegment(sketch, "E3.6.4.1", {"start": v(-36.92, 73.55) * mm, "end": v(-36.92, 68.47) * mm});
            skLineSegment(sketch, "E3.9.4.1", {"start": v(-31.84, 73.55) * mm, "end": v(-31.84, 68.47) * mm});
            skLineSegment(sketch, "E3.0.4.2", {"start": v(-36.92, 65.93) * mm, "end": v(-31.84, 65.93) * mm});
            skLineSegment(sketch, "E3.3.4.2", {"start": v(-36.92, 60.85) * mm, "end": v(-31.84, 60.85) * mm});
            skLineSegment(sketch, "E3.6.4.2", {"start": v(-36.92, 65.93) * mm, "end": v(-36.92, 60.85) * mm});
            skLineSegment(sketch, "E3.9.4.2", {"start": v(-31.84, 65.93) * mm, "end": v(-31.84, 60.85) * mm});
            skLineSegment(sketch, "E3.0.4.3", {"start": v(-36.92, 58.3) * mm, "end": v(-31.84, 58.3) * mm});
            skLineSegment(sketch, "E3.3.4.3", {"start": v(-36.92, 53.23) * mm, "end": v(-31.84, 53.23) * mm});
            skLineSegment(sketch, "E3.6.4.3", {"start": v(-36.92, 58.3) * mm, "end": v(-36.92, 53.23) * mm});
            skLineSegment(sketch, "E3.9.4.3", {"start": v(-31.84, 58.3) * mm, "end": v(-31.84, 53.23) * mm});
            skLineSegment(sketch, "E3.0.4.4", {"start": v(-36.92, 50.69) * mm, "end": v(-31.84, 50.69) * mm});
            skLineSegment(sketch, "E3.3.4.4", {"start": v(-36.92, 45.6) * mm, "end": v(-31.84, 45.6) * mm});
            skLineSegment(sketch, "E3.6.4.4", {"start": v(-36.92, 50.69) * mm, "end": v(-36.92, 45.6) * mm});
            skLineSegment(sketch, "E3.9.4.4", {"start": v(-31.84, 50.69) * mm, "end": v(-31.84, 45.6) * mm});
            skLineSegment(sketch, "E3.0.4.5", {"start": v(-36.92, 43.07) * mm, "end": v(-31.84, 43.07) * mm});
            skLineSegment(sketch, "E3.3.4.5", {"start": v(-36.92, 37.99) * mm, "end": v(-31.84, 37.99) * mm});
            skLineSegment(sketch, "E3.6.4.5", {"start": v(-36.92, 43.07) * mm, "end": v(-36.92, 37.99) * mm});
            skLineSegment(sketch, "E3.9.4.5", {"start": v(-31.84, 43.07) * mm, "end": v(-31.84, 37.99) * mm});
            skLineSegment(sketch, "E3.0.4.6", {"start": v(-36.92, 35.45) * mm, "end": v(-31.84, 35.45) * mm});
            skLineSegment(sketch, "E3.3.4.6", {"start": v(-36.92, 30.37) * mm, "end": v(-31.84, 30.37) * mm});
            skLineSegment(sketch, "E3.6.4.6", {"start": v(-36.92, 35.45) * mm, "end": v(-36.92, 30.37) * mm});
            skLineSegment(sketch, "E3.9.4.6", {"start": v(-31.84, 35.45) * mm, "end": v(-31.84, 30.37) * mm});
            skLineSegment(sketch, "E3.0.4.7", {"start": v(-36.92, 27.83) * mm, "end": v(-31.84, 27.83) * mm});
            skLineSegment(sketch, "E3.3.4.7", {"start": v(-36.92, 22.75) * mm, "end": v(-31.84, 22.75) * mm});
            skLineSegment(sketch, "E3.6.4.7", {"start": v(-36.92, 27.83) * mm, "end": v(-36.92, 22.75) * mm});
            skLineSegment(sketch, "E3.9.4.7", {"start": v(-31.84, 27.83) * mm, "end": v(-31.84, 22.75) * mm});
            skLineSegment(sketch, "E3.0.4.8", {"start": v(-36.92, 20.2) * mm, "end": v(-31.84, 20.2) * mm});
            skLineSegment(sketch, "E3.3.4.8", {"start": v(-36.92, 15.13) * mm, "end": v(-31.84, 15.13) * mm});
            skLineSegment(sketch, "E3.6.4.8", {"start": v(-36.92, 20.2) * mm, "end": v(-36.92, 15.13) * mm});
            skLineSegment(sketch, "E3.9.4.8", {"start": v(-31.84, 20.2) * mm, "end": v(-31.84, 15.13) * mm});
            skLineSegment(sketch, "E3.0.4.9", {"start": v(-36.92, 12.59) * mm, "end": v(-31.84, 12.59) * mm});
            skLineSegment(sketch, "E3.3.4.9", {"start": v(-36.92, 7.5) * mm, "end": v(-31.84, 7.5) * mm});
            skLineSegment(sketch, "E3.6.4.9", {"start": v(-36.92, 12.59) * mm, "end": v(-36.92, 7.5) * mm});
            skLineSegment(sketch, "E3.9.4.9", {"start": v(-31.84, 12.59) * mm, "end": v(-31.84, 7.5) * mm});
            skLineSegment(sketch, "E3.0.4.10", {"start": v(-36.92, 4.97) * mm, "end": v(-31.84, 4.97) * mm});
            skLineSegment(sketch, "E3.3.4.10", {"start": v(-36.92, -0.11) * mm, "end": v(-31.84, -0.11) * mm});
            skLineSegment(sketch, "E3.6.4.10", {"start": v(-36.92, 4.97) * mm, "end": v(-36.92, -0.11) * mm});
            skLineSegment(sketch, "E3.9.4.10", {"start": v(-31.84, 4.97) * mm, "end": v(-31.84, -0.11) * mm});
            skLineSegment(sketch, "E3.0.4.11", {"start": v(-36.92, -2.65) * mm, "end": v(-31.84, -2.65) * mm});
            skLineSegment(sketch, "E3.3.4.11", {"start": v(-36.92, -7.73) * mm, "end": v(-31.84, -7.73) * mm});
            skLineSegment(sketch, "E3.6.4.11", {"start": v(-36.92, -2.65) * mm, "end": v(-36.92, -7.73) * mm});
            skLineSegment(sketch, "E3.9.4.11", {"start": v(-31.84, -2.65) * mm, "end": v(-31.84, -7.73) * mm});
            skLineSegment(sketch, "E3.0.4.12", {"start": v(-36.92, -10.27) * mm, "end": v(-31.84, -10.27) * mm});
            skLineSegment(sketch, "E3.3.4.12", {"start": v(-36.92, -15.35) * mm, "end": v(-31.84, -15.35) * mm});
            skLineSegment(sketch, "E3.6.4.12", {"start": v(-36.92, -10.27) * mm, "end": v(-36.92, -15.35) * mm});
            skLineSegment(sketch, "E3.9.4.12", {"start": v(-31.84, -10.27) * mm, "end": v(-31.84, -15.35) * mm});
            skLineSegment(sketch, "E3.0.4.13", {"start": v(-36.92, -17.9) * mm, "end": v(-31.84, -17.9) * mm});
            skLineSegment(sketch, "E3.3.4.13", {"start": v(-36.92, -22.97) * mm, "end": v(-31.84, -22.97) * mm});
            skLineSegment(sketch, "E3.6.4.13", {"start": v(-36.92, -17.9) * mm, "end": v(-36.92, -22.97) * mm});
            skLineSegment(sketch, "E3.9.4.13", {"start": v(-31.84, -17.9) * mm, "end": v(-31.84, -22.97) * mm});
            skLineSegment(sketch, "E3.0.4.14", {"start": v(-36.92, -25.51) * mm, "end": v(-31.84, -25.51) * mm});
            skLineSegment(sketch, "E3.3.4.14", {"start": v(-36.92, -30.6) * mm, "end": v(-31.84, -30.6) * mm});
            skLineSegment(sketch, "E3.6.4.14", {"start": v(-36.92, -25.51) * mm, "end": v(-36.92, -30.6) * mm});
            skLineSegment(sketch, "E3.9.4.14", {"start": v(-31.84, -25.51) * mm, "end": v(-31.84, -30.6) * mm});
            skLineSegment(sketch, "E3.0.4.15", {"start": v(-36.92, -33.13) * mm, "end": v(-31.84, -33.13) * mm});
            skLineSegment(sketch, "E3.3.4.15", {"start": v(-36.92, -38.21) * mm, "end": v(-31.84, -38.21) * mm});
            skLineSegment(sketch, "E3.6.4.15", {"start": v(-36.92, -33.13) * mm, "end": v(-36.92, -38.21) * mm});
            skLineSegment(sketch, "E3.9.4.15", {"start": v(-31.84, -33.13) * mm, "end": v(-31.84, -38.21) * mm});
            skLineSegment(sketch, "E3.0.4.16", {"start": v(-36.92, -40.75) * mm, "end": v(-31.84, -40.75) * mm});
            skLineSegment(sketch, "E3.3.4.16", {"start": v(-36.92, -45.83) * mm, "end": v(-31.84, -45.83) * mm});
            skLineSegment(sketch, "E3.6.4.16", {"start": v(-36.92, -40.75) * mm, "end": v(-36.92, -45.83) * mm});
            skLineSegment(sketch, "E3.9.4.16", {"start": v(-31.84, -40.75) * mm, "end": v(-31.84, -45.83) * mm});
            skLineSegment(sketch, "E3.0.4.17", {"start": v(-36.92, -48.37) * mm, "end": v(-31.84, -48.37) * mm});
            skLineSegment(sketch, "E3.3.4.17", {"start": v(-36.92, -53.45) * mm, "end": v(-31.84, -53.45) * mm});
            skLineSegment(sketch, "E3.6.4.17", {"start": v(-36.92, -48.37) * mm, "end": v(-36.92, -53.45) * mm});
            skLineSegment(sketch, "E3.9.4.17", {"start": v(-31.84, -48.37) * mm, "end": v(-31.84, -53.45) * mm});
            skLineSegment(sketch, "E3.0.4.18", {"start": v(-36.92, -56) * mm, "end": v(-31.84, -56) * mm});
            skLineSegment(sketch, "E3.3.4.18", {"start": v(-36.92, -61.07) * mm, "end": v(-31.84, -61.07) * mm});
            skLineSegment(sketch, "E3.6.4.18", {"start": v(-36.92, -56) * mm, "end": v(-36.92, -61.07) * mm});
            skLineSegment(sketch, "E3.9.4.18", {"start": v(-31.84, -56) * mm, "end": v(-31.84, -61.07) * mm});
            skLineSegment(sketch, "E3.0.4.19", {"start": v(-36.92, -63.61) * mm, "end": v(-31.84, -63.61) * mm});
            skLineSegment(sketch, "E3.3.4.19", {"start": v(-36.92, -68.7) * mm, "end": v(-31.84, -68.7) * mm});
            skLineSegment(sketch, "E3.6.4.19", {"start": v(-36.92, -63.61) * mm, "end": v(-36.92, -68.7) * mm});
            skLineSegment(sketch, "E3.9.4.19", {"start": v(-31.84, -63.61) * mm, "end": v(-31.84, -68.7) * mm});
            skLineSegment(sketch, "E3.0.4.20", {"start": v(-36.92, -71.23) * mm, "end": v(-31.84, -71.23) * mm});
            skLineSegment(sketch, "E3.3.4.20", {"start": v(-36.92, -76.31) * mm, "end": v(-31.84, -76.31) * mm});
            skLineSegment(sketch, "E3.6.4.20", {"start": v(-36.92, -71.23) * mm, "end": v(-36.92, -76.31) * mm});
            skLineSegment(sketch, "E3.9.4.20", {"start": v(-31.84, -71.23) * mm, "end": v(-31.84, -76.31) * mm});
            skLineSegment(sketch, "E3.0.4.21", {"start": v(-36.92, -78.85) * mm, "end": v(-31.84, -78.85) * mm});
            skLineSegment(sketch, "E3.3.4.21", {"start": v(-36.92, -83.93) * mm, "end": v(-31.84, -83.93) * mm});
            skLineSegment(sketch, "E3.6.4.21", {"start": v(-36.92, -78.85) * mm, "end": v(-36.92, -83.93) * mm});
            skLineSegment(sketch, "E3.9.4.21", {"start": v(-31.84, -78.85) * mm, "end": v(-31.84, -83.93) * mm});
            skLineSegment(sketch, "E3.0.5.0", {"start": v(-29.3, 81.17) * mm, "end": v(-24.22, 81.17) * mm});
            skLineSegment(sketch, "E3.3.5.0", {"start": v(-29.3, 76.09) * mm, "end": v(-24.22, 76.09) * mm});
            skLineSegment(sketch, "E3.6.5.0", {"start": v(-29.3, 81.17) * mm, "end": v(-29.3, 76.09) * mm});
            skLineSegment(sketch, "E3.9.5.0", {"start": v(-24.22, 81.17) * mm, "end": v(-24.22, 76.09) * mm});
            skLineSegment(sketch, "E3.0.5.1", {"start": v(-29.3, 73.55) * mm, "end": v(-24.22, 73.55) * mm});
            skLineSegment(sketch, "E3.3.5.1", {"start": v(-29.3, 68.47) * mm, "end": v(-24.22, 68.47) * mm});
            skLineSegment(sketch, "E3.6.5.1", {"start": v(-29.3, 73.55) * mm, "end": v(-29.3, 68.47) * mm});
            skLineSegment(sketch, "E3.9.5.1", {"start": v(-24.22, 73.55) * mm, "end": v(-24.22, 68.47) * mm});
            skLineSegment(sketch, "E3.0.5.2", {"start": v(-29.3, 65.93) * mm, "end": v(-24.22, 65.93) * mm});
            skLineSegment(sketch, "E3.3.5.2", {"start": v(-29.3, 60.85) * mm, "end": v(-24.22, 60.85) * mm});
            skLineSegment(sketch, "E3.6.5.2", {"start": v(-29.3, 65.93) * mm, "end": v(-29.3, 60.85) * mm});
            skLineSegment(sketch, "E3.9.5.2", {"start": v(-24.22, 65.93) * mm, "end": v(-24.22, 60.85) * mm});
            skLineSegment(sketch, "E3.0.5.3", {"start": v(-29.3, 58.3) * mm, "end": v(-24.22, 58.3) * mm});
            skLineSegment(sketch, "E3.3.5.3", {"start": v(-29.3, 53.23) * mm, "end": v(-24.22, 53.23) * mm});
            skLineSegment(sketch, "E3.6.5.3", {"start": v(-29.3, 58.3) * mm, "end": v(-29.3, 53.23) * mm});
            skLineSegment(sketch, "E3.9.5.3", {"start": v(-24.22, 58.3) * mm, "end": v(-24.22, 53.23) * mm});
            skLineSegment(sketch, "E3.0.5.4", {"start": v(-29.3, 50.69) * mm, "end": v(-24.22, 50.69) * mm});
            skLineSegment(sketch, "E3.3.5.4", {"start": v(-29.3, 45.6) * mm, "end": v(-24.22, 45.6) * mm});
            skLineSegment(sketch, "E3.6.5.4", {"start": v(-29.3, 50.69) * mm, "end": v(-29.3, 45.6) * mm});
            skLineSegment(sketch, "E3.9.5.4", {"start": v(-24.22, 50.69) * mm, "end": v(-24.22, 45.6) * mm});
            skLineSegment(sketch, "E3.0.5.5", {"start": v(-29.3, 43.07) * mm, "end": v(-24.22, 43.07) * mm});
            skLineSegment(sketch, "E3.3.5.5", {"start": v(-29.3, 37.99) * mm, "end": v(-24.22, 37.99) * mm});
            skLineSegment(sketch, "E3.6.5.5", {"start": v(-29.3, 43.07) * mm, "end": v(-29.3, 37.99) * mm});
            skLineSegment(sketch, "E3.9.5.5", {"start": v(-24.22, 43.07) * mm, "end": v(-24.22, 37.99) * mm});
            skLineSegment(sketch, "E3.0.5.6", {"start": v(-29.3, 35.45) * mm, "end": v(-24.22, 35.45) * mm});
            skLineSegment(sketch, "E3.3.5.6", {"start": v(-29.3, 30.37) * mm, "end": v(-24.22, 30.37) * mm});
            skLineSegment(sketch, "E3.6.5.6", {"start": v(-29.3, 35.45) * mm, "end": v(-29.3, 30.37) * mm});
            skLineSegment(sketch, "E3.9.5.6", {"start": v(-24.22, 35.45) * mm, "end": v(-24.22, 30.37) * mm});
            skLineSegment(sketch, "E3.0.5.7", {"start": v(-29.3, 27.83) * mm, "end": v(-24.22, 27.83) * mm});
            skLineSegment(sketch, "E3.3.5.7", {"start": v(-29.3, 22.75) * mm, "end": v(-24.22, 22.75) * mm});
            skLineSegment(sketch, "E3.6.5.7", {"start": v(-29.3, 27.83) * mm, "end": v(-29.3, 22.75) * mm});
            skLineSegment(sketch, "E3.9.5.7", {"start": v(-24.22, 27.83) * mm, "end": v(-24.22, 22.75) * mm});
            skLineSegment(sketch, "E3.0.5.8", {"start": v(-29.3, 20.2) * mm, "end": v(-24.22, 20.2) * mm});
            skLineSegment(sketch, "E3.3.5.8", {"start": v(-29.3, 15.13) * mm, "end": v(-24.22, 15.13) * mm});
            skLineSegment(sketch, "E3.6.5.8", {"start": v(-29.3, 20.2) * mm, "end": v(-29.3, 15.13) * mm});
            skLineSegment(sketch, "E3.9.5.8", {"start": v(-24.22, 20.2) * mm, "end": v(-24.22, 15.13) * mm});
            skLineSegment(sketch, "E3.0.5.9", {"start": v(-29.3, 12.59) * mm, "end": v(-24.22, 12.59) * mm});
            skLineSegment(sketch, "E3.3.5.9", {"start": v(-29.3, 7.5) * mm, "end": v(-24.22, 7.5) * mm});
            skLineSegment(sketch, "E3.6.5.9", {"start": v(-29.3, 12.59) * mm, "end": v(-29.3, 7.5) * mm});
            skLineSegment(sketch, "E3.9.5.9", {"start": v(-24.22, 12.59) * mm, "end": v(-24.22, 7.5) * mm});
            skLineSegment(sketch, "E3.0.5.10", {"start": v(-29.3, 4.97) * mm, "end": v(-24.22, 4.97) * mm});
            skLineSegment(sketch, "E3.3.5.10", {"start": v(-29.3, -0.11) * mm, "end": v(-24.22, -0.11) * mm});
            skLineSegment(sketch, "E3.6.5.10", {"start": v(-29.3, 4.97) * mm, "end": v(-29.3, -0.11) * mm});
            skLineSegment(sketch, "E3.9.5.10", {"start": v(-24.22, 4.97) * mm, "end": v(-24.22, -0.11) * mm});
            skLineSegment(sketch, "E3.0.5.11", {"start": v(-29.3, -2.65) * mm, "end": v(-24.22, -2.65) * mm});
            skLineSegment(sketch, "E3.3.5.11", {"start": v(-29.3, -7.73) * mm, "end": v(-24.22, -7.73) * mm});
            skLineSegment(sketch, "E3.6.5.11", {"start": v(-29.3, -2.65) * mm, "end": v(-29.3, -7.73) * mm});
            skLineSegment(sketch, "E3.9.5.11", {"start": v(-24.22, -2.65) * mm, "end": v(-24.22, -7.73) * mm});
            skLineSegment(sketch, "E3.0.5.12", {"start": v(-29.3, -10.27) * mm, "end": v(-24.22, -10.27) * mm});
            skLineSegment(sketch, "E3.3.5.12", {"start": v(-29.3, -15.35) * mm, "end": v(-24.22, -15.35) * mm});
            skLineSegment(sketch, "E3.6.5.12", {"start": v(-29.3, -10.27) * mm, "end": v(-29.3, -15.35) * mm});
            skLineSegment(sketch, "E3.9.5.12", {"start": v(-24.22, -10.27) * mm, "end": v(-24.22, -15.35) * mm});
            skLineSegment(sketch, "E3.0.5.13", {"start": v(-29.3, -17.9) * mm, "end": v(-24.22, -17.9) * mm});
            skLineSegment(sketch, "E3.3.5.13", {"start": v(-29.3, -22.97) * mm, "end": v(-24.22, -22.97) * mm});
            skLineSegment(sketch, "E3.6.5.13", {"start": v(-29.3, -17.9) * mm, "end": v(-29.3, -22.97) * mm});
            skLineSegment(sketch, "E3.9.5.13", {"start": v(-24.22, -17.9) * mm, "end": v(-24.22, -22.97) * mm});
            skLineSegment(sketch, "E3.0.5.14", {"start": v(-29.3, -25.51) * mm, "end": v(-24.22, -25.51) * mm});
            skLineSegment(sketch, "E3.3.5.14", {"start": v(-29.3, -30.6) * mm, "end": v(-24.22, -30.6) * mm});
            skLineSegment(sketch, "E3.6.5.14", {"start": v(-29.3, -25.51) * mm, "end": v(-29.3, -30.6) * mm});
            skLineSegment(sketch, "E3.9.5.14", {"start": v(-24.22, -25.51) * mm, "end": v(-24.22, -30.6) * mm});
            skLineSegment(sketch, "E3.0.5.15", {"start": v(-29.3, -33.13) * mm, "end": v(-24.22, -33.13) * mm});
            skLineSegment(sketch, "E3.3.5.15", {"start": v(-29.3, -38.21) * mm, "end": v(-24.22, -38.21) * mm});
            skLineSegment(sketch, "E3.6.5.15", {"start": v(-29.3, -33.13) * mm, "end": v(-29.3, -38.21) * mm});
            skLineSegment(sketch, "E3.9.5.15", {"start": v(-24.22, -33.13) * mm, "end": v(-24.22, -38.21) * mm});
            skLineSegment(sketch, "E3.0.5.16", {"start": v(-29.3, -40.75) * mm, "end": v(-24.22, -40.75) * mm});
            skLineSegment(sketch, "E3.3.5.16", {"start": v(-29.3, -45.83) * mm, "end": v(-24.22, -45.83) * mm});
            skLineSegment(sketch, "E3.6.5.16", {"start": v(-29.3, -40.75) * mm, "end": v(-29.3, -45.83) * mm});
            skLineSegment(sketch, "E3.9.5.16", {"start": v(-24.22, -40.75) * mm, "end": v(-24.22, -45.83) * mm});
            skLineSegment(sketch, "E3.0.5.17", {"start": v(-29.3, -48.37) * mm, "end": v(-24.22, -48.37) * mm});
            skLineSegment(sketch, "E3.3.5.17", {"start": v(-29.3, -53.45) * mm, "end": v(-24.22, -53.45) * mm});
            skLineSegment(sketch, "E3.6.5.17", {"start": v(-29.3, -48.37) * mm, "end": v(-29.3, -53.45) * mm});
            skLineSegment(sketch, "E3.9.5.17", {"start": v(-24.22, -48.37) * mm, "end": v(-24.22, -53.45) * mm});
            skLineSegment(sketch, "E3.0.5.18", {"start": v(-29.3, -56) * mm, "end": v(-24.22, -56) * mm});
            skLineSegment(sketch, "E3.3.5.18", {"start": v(-29.3, -61.07) * mm, "end": v(-24.22, -61.07) * mm});
            skLineSegment(sketch, "E3.6.5.18", {"start": v(-29.3, -56) * mm, "end": v(-29.3, -61.07) * mm});
            skLineSegment(sketch, "E3.9.5.18", {"start": v(-24.22, -56) * mm, "end": v(-24.22, -61.07) * mm});
            skLineSegment(sketch, "E3.0.5.19", {"start": v(-29.3, -63.61) * mm, "end": v(-24.22, -63.61) * mm});
            skLineSegment(sketch, "E3.3.5.19", {"start": v(-29.3, -68.7) * mm, "end": v(-24.22, -68.7) * mm});
            skLineSegment(sketch, "E3.6.5.19", {"start": v(-29.3, -63.61) * mm, "end": v(-29.3, -68.7) * mm});
            skLineSegment(sketch, "E3.9.5.19", {"start": v(-24.22, -63.61) * mm, "end": v(-24.22, -68.7) * mm});
            skLineSegment(sketch, "E3.0.5.20", {"start": v(-29.3, -71.23) * mm, "end": v(-24.22, -71.23) * mm});
            skLineSegment(sketch, "E3.3.5.20", {"start": v(-29.3, -76.31) * mm, "end": v(-24.22, -76.31) * mm});
            skLineSegment(sketch, "E3.6.5.20", {"start": v(-29.3, -71.23) * mm, "end": v(-29.3, -76.31) * mm});
            skLineSegment(sketch, "E3.9.5.20", {"start": v(-24.22, -71.23) * mm, "end": v(-24.22, -76.31) * mm});
            skLineSegment(sketch, "E3.0.5.21", {"start": v(-29.3, -78.85) * mm, "end": v(-24.22, -78.85) * mm});
            skLineSegment(sketch, "E3.3.5.21", {"start": v(-29.3, -83.93) * mm, "end": v(-24.22, -83.93) * mm});
            skLineSegment(sketch, "E3.6.5.21", {"start": v(-29.3, -78.85) * mm, "end": v(-29.3, -83.93) * mm});
            skLineSegment(sketch, "E3.9.5.21", {"start": v(-24.22, -78.85) * mm, "end": v(-24.22, -83.93) * mm});
            skLineSegment(sketch, "E3.0.6.0", {"start": v(-21.68, 81.17) * mm, "end": v(-16.6, 81.17) * mm});
            skLineSegment(sketch, "E3.3.6.0", {"start": v(-21.68, 76.09) * mm, "end": v(-16.6, 76.09) * mm});
            skLineSegment(sketch, "E3.6.6.0", {"start": v(-21.68, 81.17) * mm, "end": v(-21.68, 76.09) * mm});
            skLineSegment(sketch, "E3.9.6.0", {"start": v(-16.6, 81.17) * mm, "end": v(-16.6, 76.09) * mm});
            skLineSegment(sketch, "E3.0.6.1", {"start": v(-21.68, 73.55) * mm, "end": v(-16.6, 73.55) * mm});
            skLineSegment(sketch, "E3.3.6.1", {"start": v(-21.68, 68.47) * mm, "end": v(-16.6, 68.47) * mm});
            skLineSegment(sketch, "E3.6.6.1", {"start": v(-21.68, 73.55) * mm, "end": v(-21.68, 68.47) * mm});
            skLineSegment(sketch, "E3.9.6.1", {"start": v(-16.6, 73.55) * mm, "end": v(-16.6, 68.47) * mm});
            skLineSegment(sketch, "E3.0.6.2", {"start": v(-21.68, 65.93) * mm, "end": v(-16.6, 65.93) * mm});
            skLineSegment(sketch, "E3.3.6.2", {"start": v(-21.68, 60.85) * mm, "end": v(-16.6, 60.85) * mm});
            skLineSegment(sketch, "E3.6.6.2", {"start": v(-21.68, 65.93) * mm, "end": v(-21.68, 60.85) * mm});
            skLineSegment(sketch, "E3.9.6.2", {"start": v(-16.6, 65.93) * mm, "end": v(-16.6, 60.85) * mm});
            skLineSegment(sketch, "E3.0.6.3", {"start": v(-21.68, 58.3) * mm, "end": v(-16.6, 58.3) * mm});
            skLineSegment(sketch, "E3.3.6.3", {"start": v(-21.68, 53.23) * mm, "end": v(-16.6, 53.23) * mm});
            skLineSegment(sketch, "E3.6.6.3", {"start": v(-21.68, 58.3) * mm, "end": v(-21.68, 53.23) * mm});
            skLineSegment(sketch, "E3.9.6.3", {"start": v(-16.6, 58.3) * mm, "end": v(-16.6, 53.23) * mm});
            skLineSegment(sketch, "E3.0.6.4", {"start": v(-21.68, 50.69) * mm, "end": v(-16.6, 50.69) * mm});
            skLineSegment(sketch, "E3.3.6.4", {"start": v(-21.68, 45.6) * mm, "end": v(-16.6, 45.6) * mm});
            skLineSegment(sketch, "E3.6.6.4", {"start": v(-21.68, 50.69) * mm, "end": v(-21.68, 45.6) * mm});
            skLineSegment(sketch, "E3.9.6.4", {"start": v(-16.6, 50.69) * mm, "end": v(-16.6, 45.6) * mm});
            skLineSegment(sketch, "E3.0.6.5", {"start": v(-21.68, 43.07) * mm, "end": v(-16.6, 43.07) * mm});
            skLineSegment(sketch, "E3.3.6.5", {"start": v(-21.68, 37.99) * mm, "end": v(-16.6, 37.99) * mm});
            skLineSegment(sketch, "E3.6.6.5", {"start": v(-21.68, 43.07) * mm, "end": v(-21.68, 37.99) * mm});
            skLineSegment(sketch, "E3.9.6.5", {"start": v(-16.6, 43.07) * mm, "end": v(-16.6, 37.99) * mm});
            skLineSegment(sketch, "E3.0.6.6", {"start": v(-21.68, 35.45) * mm, "end": v(-16.6, 35.45) * mm});
            skLineSegment(sketch, "E3.3.6.6", {"start": v(-21.68, 30.37) * mm, "end": v(-16.6, 30.37) * mm});
            skLineSegment(sketch, "E3.6.6.6", {"start": v(-21.68, 35.45) * mm, "end": v(-21.68, 30.37) * mm});
            skLineSegment(sketch, "E3.9.6.6", {"start": v(-16.6, 35.45) * mm, "end": v(-16.6, 30.37) * mm});
            skLineSegment(sketch, "E3.0.6.7", {"start": v(-21.68, 27.83) * mm, "end": v(-16.6, 27.83) * mm});
            skLineSegment(sketch, "E3.3.6.7", {"start": v(-21.68, 22.75) * mm, "end": v(-16.6, 22.75) * mm});
            skLineSegment(sketch, "E3.6.6.7", {"start": v(-21.68, 27.83) * mm, "end": v(-21.68, 22.75) * mm});
            skLineSegment(sketch, "E3.9.6.7", {"start": v(-16.6, 27.83) * mm, "end": v(-16.6, 22.75) * mm});
            skLineSegment(sketch, "E3.0.6.8", {"start": v(-21.68, 20.2) * mm, "end": v(-16.6, 20.2) * mm});
            skLineSegment(sketch, "E3.3.6.8", {"start": v(-21.68, 15.13) * mm, "end": v(-16.6, 15.13) * mm});
            skLineSegment(sketch, "E3.6.6.8", {"start": v(-21.68, 20.2) * mm, "end": v(-21.68, 15.13) * mm});
            skLineSegment(sketch, "E3.9.6.8", {"start": v(-16.6, 20.2) * mm, "end": v(-16.6, 15.13) * mm});
            skLineSegment(sketch, "E3.0.6.9", {"start": v(-21.68, 12.59) * mm, "end": v(-16.6, 12.59) * mm});
            skLineSegment(sketch, "E3.3.6.9", {"start": v(-21.68, 7.5) * mm, "end": v(-16.6, 7.5) * mm});
            skLineSegment(sketch, "E3.6.6.9", {"start": v(-21.68, 12.59) * mm, "end": v(-21.68, 7.5) * mm});
            skLineSegment(sketch, "E3.9.6.9", {"start": v(-16.6, 12.59) * mm, "end": v(-16.6, 7.5) * mm});
            skLineSegment(sketch, "E3.0.6.10", {"start": v(-21.68, 4.97) * mm, "end": v(-16.6, 4.97) * mm});
            skLineSegment(sketch, "E3.3.6.10", {"start": v(-21.68, -0.11) * mm, "end": v(-16.6, -0.11) * mm});
            skLineSegment(sketch, "E3.6.6.10", {"start": v(-21.68, 4.97) * mm, "end": v(-21.68, -0.11) * mm});
            skLineSegment(sketch, "E3.9.6.10", {"start": v(-16.6, 4.97) * mm, "end": v(-16.6, -0.11) * mm});
            skLineSegment(sketch, "E3.0.6.11", {"start": v(-21.68, -2.65) * mm, "end": v(-16.6, -2.65) * mm});
            skLineSegment(sketch, "E3.3.6.11", {"start": v(-21.68, -7.73) * mm, "end": v(-16.6, -7.73) * mm});
            skLineSegment(sketch, "E3.6.6.11", {"start": v(-21.68, -2.65) * mm, "end": v(-21.68, -7.73) * mm});
            skLineSegment(sketch, "E3.9.6.11", {"start": v(-16.6, -2.65) * mm, "end": v(-16.6, -7.73) * mm});
            skLineSegment(sketch, "E3.0.6.12", {"start": v(-21.68, -10.27) * mm, "end": v(-16.6, -10.27) * mm});
            skLineSegment(sketch, "E3.3.6.12", {"start": v(-21.68, -15.35) * mm, "end": v(-16.6, -15.35) * mm});
            skLineSegment(sketch, "E3.6.6.12", {"start": v(-21.68, -10.27) * mm, "end": v(-21.68, -15.35) * mm});
            skLineSegment(sketch, "E3.9.6.12", {"start": v(-16.6, -10.27) * mm, "end": v(-16.6, -15.35) * mm});
            skLineSegment(sketch, "E3.0.6.13", {"start": v(-21.68, -17.9) * mm, "end": v(-16.6, -17.9) * mm});
            skLineSegment(sketch, "E3.3.6.13", {"start": v(-21.68, -22.97) * mm, "end": v(-16.6, -22.97) * mm});
            skLineSegment(sketch, "E3.6.6.13", {"start": v(-21.68, -17.9) * mm, "end": v(-21.68, -22.97) * mm});
            skLineSegment(sketch, "E3.9.6.13", {"start": v(-16.6, -17.9) * mm, "end": v(-16.6, -22.97) * mm});
            skLineSegment(sketch, "E3.0.6.14", {"start": v(-21.68, -25.51) * mm, "end": v(-16.6, -25.51) * mm});
            skLineSegment(sketch, "E3.3.6.14", {"start": v(-21.68, -30.6) * mm, "end": v(-16.6, -30.6) * mm});
            skLineSegment(sketch, "E3.6.6.14", {"start": v(-21.68, -25.51) * mm, "end": v(-21.68, -30.6) * mm});
            skLineSegment(sketch, "E3.9.6.14", {"start": v(-16.6, -25.51) * mm, "end": v(-16.6, -30.6) * mm});
            skLineSegment(sketch, "E3.0.6.15", {"start": v(-21.68, -33.13) * mm, "end": v(-16.6, -33.13) * mm});
            skLineSegment(sketch, "E3.3.6.15", {"start": v(-21.68, -38.21) * mm, "end": v(-16.6, -38.21) * mm});
            skLineSegment(sketch, "E3.6.6.15", {"start": v(-21.68, -33.13) * mm, "end": v(-21.68, -38.21) * mm});
            skLineSegment(sketch, "E3.9.6.15", {"start": v(-16.6, -33.13) * mm, "end": v(-16.6, -38.21) * mm});
            skLineSegment(sketch, "E3.0.6.16", {"start": v(-21.68, -40.75) * mm, "end": v(-16.6, -40.75) * mm});
            skLineSegment(sketch, "E3.3.6.16", {"start": v(-21.68, -45.83) * mm, "end": v(-16.6, -45.83) * mm});
            skLineSegment(sketch, "E3.6.6.16", {"start": v(-21.68, -40.75) * mm, "end": v(-21.68, -45.83) * mm});
            skLineSegment(sketch, "E3.9.6.16", {"start": v(-16.6, -40.75) * mm, "end": v(-16.6, -45.83) * mm});
            skLineSegment(sketch, "E3.0.6.17", {"start": v(-21.68, -48.37) * mm, "end": v(-16.6, -48.37) * mm});
            skLineSegment(sketch, "E3.3.6.17", {"start": v(-21.68, -53.45) * mm, "end": v(-16.6, -53.45) * mm});
            skLineSegment(sketch, "E3.6.6.17", {"start": v(-21.68, -48.37) * mm, "end": v(-21.68, -53.45) * mm});
            skLineSegment(sketch, "E3.9.6.17", {"start": v(-16.6, -48.37) * mm, "end": v(-16.6, -53.45) * mm});
            skLineSegment(sketch, "E3.0.6.18", {"start": v(-21.68, -56) * mm, "end": v(-16.6, -56) * mm});
            skLineSegment(sketch, "E3.3.6.18", {"start": v(-21.68, -61.07) * mm, "end": v(-16.6, -61.07) * mm});
            skLineSegment(sketch, "E3.6.6.18", {"start": v(-21.68, -56) * mm, "end": v(-21.68, -61.07) * mm});
            skLineSegment(sketch, "E3.9.6.18", {"start": v(-16.6, -56) * mm, "end": v(-16.6, -61.07) * mm});
            skLineSegment(sketch, "E3.0.6.19", {"start": v(-21.68, -63.61) * mm, "end": v(-16.6, -63.61) * mm});
            skLineSegment(sketch, "E3.3.6.19", {"start": v(-21.68, -68.7) * mm, "end": v(-16.6, -68.7) * mm});
            skLineSegment(sketch, "E3.6.6.19", {"start": v(-21.68, -63.61) * mm, "end": v(-21.68, -68.7) * mm});
            skLineSegment(sketch, "E3.9.6.19", {"start": v(-16.6, -63.61) * mm, "end": v(-16.6, -68.7) * mm});
            skLineSegment(sketch, "E3.0.6.20", {"start": v(-21.68, -71.23) * mm, "end": v(-16.6, -71.23) * mm});
            skLineSegment(sketch, "E3.3.6.20", {"start": v(-21.68, -76.31) * mm, "end": v(-16.6, -76.31) * mm});
            skLineSegment(sketch, "E3.6.6.20", {"start": v(-21.68, -71.23) * mm, "end": v(-21.68, -76.31) * mm});
            skLineSegment(sketch, "E3.9.6.20", {"start": v(-16.6, -71.23) * mm, "end": v(-16.6, -76.31) * mm});
            skLineSegment(sketch, "E3.0.6.21", {"start": v(-21.68, -78.85) * mm, "end": v(-16.6, -78.85) * mm});
            skLineSegment(sketch, "E3.3.6.21", {"start": v(-21.68, -83.93) * mm, "end": v(-16.6, -83.93) * mm});
            skLineSegment(sketch, "E3.6.6.21", {"start": v(-21.68, -78.85) * mm, "end": v(-21.68, -83.93) * mm});
            skLineSegment(sketch, "E3.9.6.21", {"start": v(-16.6, -78.85) * mm, "end": v(-16.6, -83.93) * mm});
            skLineSegment(sketch, "E3.0.7.0", {"start": v(-14.06, 81.17) * mm, "end": v(-8.98, 81.17) * mm});
            skLineSegment(sketch, "E3.3.7.0", {"start": v(-14.06, 76.09) * mm, "end": v(-8.98, 76.09) * mm});
            skLineSegment(sketch, "E3.6.7.0", {"start": v(-14.06, 81.17) * mm, "end": v(-14.06, 76.09) * mm});
            skLineSegment(sketch, "E3.9.7.0", {"start": v(-8.98, 81.17) * mm, "end": v(-8.98, 76.09) * mm});
            skLineSegment(sketch, "E3.0.7.1", {"start": v(-14.06, 73.55) * mm, "end": v(-8.98, 73.55) * mm});
            skLineSegment(sketch, "E3.3.7.1", {"start": v(-14.06, 68.47) * mm, "end": v(-8.98, 68.47) * mm});
            skLineSegment(sketch, "E3.6.7.1", {"start": v(-14.06, 73.55) * mm, "end": v(-14.06, 68.47) * mm});
            skLineSegment(sketch, "E3.9.7.1", {"start": v(-8.98, 73.55) * mm, "end": v(-8.98, 68.47) * mm});
            skLineSegment(sketch, "E3.0.7.2", {"start": v(-14.06, 65.93) * mm, "end": v(-8.98, 65.93) * mm});
            skLineSegment(sketch, "E3.3.7.2", {"start": v(-14.06, 60.85) * mm, "end": v(-8.98, 60.85) * mm});
            skLineSegment(sketch, "E3.6.7.2", {"start": v(-14.06, 65.93) * mm, "end": v(-14.06, 60.85) * mm});
            skLineSegment(sketch, "E3.9.7.2", {"start": v(-8.98, 65.93) * mm, "end": v(-8.98, 60.85) * mm});
            skLineSegment(sketch, "E3.0.7.3", {"start": v(-14.06, 58.3) * mm, "end": v(-8.98, 58.3) * mm});
            skLineSegment(sketch, "E3.3.7.3", {"start": v(-14.06, 53.23) * mm, "end": v(-8.98, 53.23) * mm});
            skLineSegment(sketch, "E3.6.7.3", {"start": v(-14.06, 58.3) * mm, "end": v(-14.06, 53.23) * mm});
            skLineSegment(sketch, "E3.9.7.3", {"start": v(-8.98, 58.3) * mm, "end": v(-8.98, 53.23) * mm});
            skLineSegment(sketch, "E3.0.7.4", {"start": v(-14.06, 50.69) * mm, "end": v(-8.98, 50.69) * mm});
            skLineSegment(sketch, "E3.3.7.4", {"start": v(-14.06, 45.6) * mm, "end": v(-8.98, 45.6) * mm});
            skLineSegment(sketch, "E3.6.7.4", {"start": v(-14.06, 50.69) * mm, "end": v(-14.06, 45.6) * mm});
            skLineSegment(sketch, "E3.9.7.4", {"start": v(-8.98, 50.69) * mm, "end": v(-8.98, 45.6) * mm});
            skLineSegment(sketch, "E3.0.7.5", {"start": v(-14.06, 43.07) * mm, "end": v(-8.98, 43.07) * mm});
            skLineSegment(sketch, "E3.3.7.5", {"start": v(-14.06, 37.99) * mm, "end": v(-8.98, 37.99) * mm});
            skLineSegment(sketch, "E3.6.7.5", {"start": v(-14.06, 43.07) * mm, "end": v(-14.06, 37.99) * mm});
            skLineSegment(sketch, "E3.9.7.5", {"start": v(-8.98, 43.07) * mm, "end": v(-8.98, 37.99) * mm});
            skLineSegment(sketch, "E3.0.7.6", {"start": v(-14.06, 35.45) * mm, "end": v(-8.98, 35.45) * mm});
            skLineSegment(sketch, "E3.3.7.6", {"start": v(-14.06, 30.37) * mm, "end": v(-8.98, 30.37) * mm});
            skLineSegment(sketch, "E3.6.7.6", {"start": v(-14.06, 35.45) * mm, "end": v(-14.06, 30.37) * mm});
            skLineSegment(sketch, "E3.9.7.6", {"start": v(-8.98, 35.45) * mm, "end": v(-8.98, 30.37) * mm});
            skLineSegment(sketch, "E3.0.7.7", {"start": v(-14.06, 27.83) * mm, "end": v(-8.98, 27.83) * mm});
            skLineSegment(sketch, "E3.3.7.7", {"start": v(-14.06, 22.75) * mm, "end": v(-8.98, 22.75) * mm});
            skLineSegment(sketch, "E3.6.7.7", {"start": v(-14.06, 27.83) * mm, "end": v(-14.06, 22.75) * mm});
            skLineSegment(sketch, "E3.9.7.7", {"start": v(-8.98, 27.83) * mm, "end": v(-8.98, 22.75) * mm});
            skLineSegment(sketch, "E3.0.7.8", {"start": v(-14.06, 20.2) * mm, "end": v(-8.98, 20.2) * mm});
            skLineSegment(sketch, "E3.3.7.8", {"start": v(-14.06, 15.13) * mm, "end": v(-8.98, 15.13) * mm});
            skLineSegment(sketch, "E3.6.7.8", {"start": v(-14.06, 20.2) * mm, "end": v(-14.06, 15.13) * mm});
            skLineSegment(sketch, "E3.9.7.8", {"start": v(-8.98, 20.2) * mm, "end": v(-8.98, 15.13) * mm});
            skLineSegment(sketch, "E3.0.7.9", {"start": v(-14.06, 12.59) * mm, "end": v(-8.98, 12.59) * mm});
            skLineSegment(sketch, "E3.3.7.9", {"start": v(-14.06, 7.5) * mm, "end": v(-8.98, 7.5) * mm});
            skLineSegment(sketch, "E3.6.7.9", {"start": v(-14.06, 12.59) * mm, "end": v(-14.06, 7.5) * mm});
            skLineSegment(sketch, "E3.9.7.9", {"start": v(-8.98, 12.59) * mm, "end": v(-8.98, 7.5) * mm});
            skLineSegment(sketch, "E3.0.7.10", {"start": v(-14.06, 4.97) * mm, "end": v(-8.98, 4.97) * mm});
            skLineSegment(sketch, "E3.3.7.10", {"start": v(-14.06, -0.11) * mm, "end": v(-8.98, -0.11) * mm});
            skLineSegment(sketch, "E3.6.7.10", {"start": v(-14.06, 4.97) * mm, "end": v(-14.06, -0.11) * mm});
            skLineSegment(sketch, "E3.9.7.10", {"start": v(-8.98, 4.97) * mm, "end": v(-8.98, -0.11) * mm});
            skLineSegment(sketch, "E3.0.7.11", {"start": v(-14.06, -2.65) * mm, "end": v(-8.98, -2.65) * mm});
            skLineSegment(sketch, "E3.3.7.11", {"start": v(-14.06, -7.73) * mm, "end": v(-8.98, -7.73) * mm});
            skLineSegment(sketch, "E3.6.7.11", {"start": v(-14.06, -2.65) * mm, "end": v(-14.06, -7.73) * mm});
            skLineSegment(sketch, "E3.9.7.11", {"start": v(-8.98, -2.65) * mm, "end": v(-8.98, -7.73) * mm});
            skLineSegment(sketch, "E3.0.7.12", {"start": v(-14.06, -10.27) * mm, "end": v(-8.98, -10.27) * mm});
            skLineSegment(sketch, "E3.3.7.12", {"start": v(-14.06, -15.35) * mm, "end": v(-8.98, -15.35) * mm});
            skLineSegment(sketch, "E3.6.7.12", {"start": v(-14.06, -10.27) * mm, "end": v(-14.06, -15.35) * mm});
            skLineSegment(sketch, "E3.9.7.12", {"start": v(-8.98, -10.27) * mm, "end": v(-8.98, -15.35) * mm});
            skLineSegment(sketch, "E3.0.7.13", {"start": v(-14.06, -17.9) * mm, "end": v(-8.98, -17.9) * mm});
            skLineSegment(sketch, "E3.3.7.13", {"start": v(-14.06, -22.97) * mm, "end": v(-8.98, -22.97) * mm});
            skLineSegment(sketch, "E3.6.7.13", {"start": v(-14.06, -17.9) * mm, "end": v(-14.06, -22.97) * mm});
            skLineSegment(sketch, "E3.9.7.13", {"start": v(-8.98, -17.9) * mm, "end": v(-8.98, -22.97) * mm});
            skLineSegment(sketch, "E3.0.7.14", {"start": v(-14.06, -25.51) * mm, "end": v(-8.98, -25.51) * mm});
            skLineSegment(sketch, "E3.3.7.14", {"start": v(-14.06, -30.6) * mm, "end": v(-8.98, -30.6) * mm});
            skLineSegment(sketch, "E3.6.7.14", {"start": v(-14.06, -25.51) * mm, "end": v(-14.06, -30.6) * mm});
            skLineSegment(sketch, "E3.9.7.14", {"start": v(-8.98, -25.51) * mm, "end": v(-8.98, -30.6) * mm});
            skLineSegment(sketch, "E3.0.7.15", {"start": v(-14.06, -33.13) * mm, "end": v(-8.98, -33.13) * mm});
            skLineSegment(sketch, "E3.3.7.15", {"start": v(-14.06, -38.21) * mm, "end": v(-8.98, -38.21) * mm});
            skLineSegment(sketch, "E3.6.7.15", {"start": v(-14.06, -33.13) * mm, "end": v(-14.06, -38.21) * mm});
            skLineSegment(sketch, "E3.9.7.15", {"start": v(-8.98, -33.13) * mm, "end": v(-8.98, -38.21) * mm});
            skLineSegment(sketch, "E3.0.7.16", {"start": v(-14.06, -40.75) * mm, "end": v(-8.98, -40.75) * mm});
            skLineSegment(sketch, "E3.3.7.16", {"start": v(-14.06, -45.83) * mm, "end": v(-8.98, -45.83) * mm});
            skLineSegment(sketch, "E3.6.7.16", {"start": v(-14.06, -40.75) * mm, "end": v(-14.06, -45.83) * mm});
            skLineSegment(sketch, "E3.9.7.16", {"start": v(-8.98, -40.75) * mm, "end": v(-8.98, -45.83) * mm});
            skLineSegment(sketch, "E3.0.7.17", {"start": v(-14.06, -48.37) * mm, "end": v(-8.98, -48.37) * mm});
            skLineSegment(sketch, "E3.3.7.17", {"start": v(-14.06, -53.45) * mm, "end": v(-8.98, -53.45) * mm});
            skLineSegment(sketch, "E3.6.7.17", {"start": v(-14.06, -48.37) * mm, "end": v(-14.06, -53.45) * mm});
            skLineSegment(sketch, "E3.9.7.17", {"start": v(-8.98, -48.37) * mm, "end": v(-8.98, -53.45) * mm});
            skLineSegment(sketch, "E3.0.7.18", {"start": v(-14.06, -56) * mm, "end": v(-8.98, -56) * mm});
            skLineSegment(sketch, "E3.3.7.18", {"start": v(-14.06, -61.07) * mm, "end": v(-8.98, -61.07) * mm});
            skLineSegment(sketch, "E3.6.7.18", {"start": v(-14.06, -56) * mm, "end": v(-14.06, -61.07) * mm});
            skLineSegment(sketch, "E3.9.7.18", {"start": v(-8.98, -56) * mm, "end": v(-8.98, -61.07) * mm});
            skLineSegment(sketch, "E3.0.7.19", {"start": v(-14.06, -63.61) * mm, "end": v(-8.98, -63.61) * mm});
            skLineSegment(sketch, "E3.3.7.19", {"start": v(-14.06, -68.7) * mm, "end": v(-8.98, -68.7) * mm});
            skLineSegment(sketch, "E3.6.7.19", {"start": v(-14.06, -63.61) * mm, "end": v(-14.06, -68.7) * mm});
            skLineSegment(sketch, "E3.9.7.19", {"start": v(-8.98, -63.61) * mm, "end": v(-8.98, -68.7) * mm});
            skLineSegment(sketch, "E3.0.7.20", {"start": v(-14.06, -71.23) * mm, "end": v(-8.98, -71.23) * mm});
            skLineSegment(sketch, "E3.3.7.20", {"start": v(-14.06, -76.31) * mm, "end": v(-8.98, -76.31) * mm});
            skLineSegment(sketch, "E3.6.7.20", {"start": v(-14.06, -71.23) * mm, "end": v(-14.06, -76.31) * mm});
            skLineSegment(sketch, "E3.9.7.20", {"start": v(-8.98, -71.23) * mm, "end": v(-8.98, -76.31) * mm});
            skLineSegment(sketch, "E3.0.7.21", {"start": v(-14.06, -78.85) * mm, "end": v(-8.98, -78.85) * mm});
            skLineSegment(sketch, "E3.3.7.21", {"start": v(-14.06, -83.93) * mm, "end": v(-8.98, -83.93) * mm});
            skLineSegment(sketch, "E3.6.7.21", {"start": v(-14.06, -78.85) * mm, "end": v(-14.06, -83.93) * mm});
            skLineSegment(sketch, "E3.9.7.21", {"start": v(-8.98, -78.85) * mm, "end": v(-8.98, -83.93) * mm});
            skLineSegment(sketch, "E3.0.8.0", {"start": v(-6.44, 81.17) * mm, "end": v(-1.36, 81.17) * mm});
            skLineSegment(sketch, "E3.3.8.0", {"start": v(-6.44, 76.09) * mm, "end": v(-1.36, 76.09) * mm});
            skLineSegment(sketch, "E3.6.8.0", {"start": v(-6.44, 81.17) * mm, "end": v(-6.44, 76.09) * mm});
            skLineSegment(sketch, "E3.9.8.0", {"start": v(-1.36, 81.17) * mm, "end": v(-1.36, 76.09) * mm});
            skLineSegment(sketch, "E3.0.8.1", {"start": v(-6.44, 73.55) * mm, "end": v(-1.36, 73.55) * mm});
            skLineSegment(sketch, "E3.3.8.1", {"start": v(-6.44, 68.47) * mm, "end": v(-1.36, 68.47) * mm});
            skLineSegment(sketch, "E3.6.8.1", {"start": v(-6.44, 73.55) * mm, "end": v(-6.44, 68.47) * mm});
            skLineSegment(sketch, "E3.9.8.1", {"start": v(-1.36, 73.55) * mm, "end": v(-1.36, 68.47) * mm});
            skLineSegment(sketch, "E3.0.8.2", {"start": v(-6.44, 65.93) * mm, "end": v(-1.36, 65.93) * mm});
            skLineSegment(sketch, "E3.3.8.2", {"start": v(-6.44, 60.85) * mm, "end": v(-1.36, 60.85) * mm});
            skLineSegment(sketch, "E3.6.8.2", {"start": v(-6.44, 65.93) * mm, "end": v(-6.44, 60.85) * mm});
            skLineSegment(sketch, "E3.9.8.2", {"start": v(-1.36, 65.93) * mm, "end": v(-1.36, 60.85) * mm});
            skLineSegment(sketch, "E3.0.8.3", {"start": v(-6.44, 58.3) * mm, "end": v(-1.36, 58.3) * mm});
            skLineSegment(sketch, "E3.3.8.3", {"start": v(-6.44, 53.23) * mm, "end": v(-1.36, 53.23) * mm});
            skLineSegment(sketch, "E3.6.8.3", {"start": v(-6.44, 58.3) * mm, "end": v(-6.44, 53.23) * mm});
            skLineSegment(sketch, "E3.9.8.3", {"start": v(-1.36, 58.3) * mm, "end": v(-1.36, 53.23) * mm});
            skLineSegment(sketch, "E3.0.8.4", {"start": v(-6.44, 50.69) * mm, "end": v(-1.36, 50.69) * mm});
            skLineSegment(sketch, "E3.3.8.4", {"start": v(-6.44, 45.6) * mm, "end": v(-1.36, 45.6) * mm});
            skLineSegment(sketch, "E3.6.8.4", {"start": v(-6.44, 50.69) * mm, "end": v(-6.44, 45.6) * mm});
            skLineSegment(sketch, "E3.9.8.4", {"start": v(-1.36, 50.69) * mm, "end": v(-1.36, 45.6) * mm});
            skLineSegment(sketch, "E3.0.8.5", {"start": v(-6.44, 43.07) * mm, "end": v(-1.36, 43.07) * mm});
            skLineSegment(sketch, "E3.3.8.5", {"start": v(-6.44, 37.99) * mm, "end": v(-1.36, 37.99) * mm});
            skLineSegment(sketch, "E3.6.8.5", {"start": v(-6.44, 43.07) * mm, "end": v(-6.44, 37.99) * mm});
            skLineSegment(sketch, "E3.9.8.5", {"start": v(-1.36, 43.07) * mm, "end": v(-1.36, 37.99) * mm});
            skLineSegment(sketch, "E3.0.8.6", {"start": v(-6.44, 35.45) * mm, "end": v(-1.36, 35.45) * mm});
            skLineSegment(sketch, "E3.3.8.6", {"start": v(-6.44, 30.37) * mm, "end": v(-1.36, 30.37) * mm});
            skLineSegment(sketch, "E3.6.8.6", {"start": v(-6.44, 35.45) * mm, "end": v(-6.44, 30.37) * mm});
            skLineSegment(sketch, "E3.9.8.6", {"start": v(-1.36, 35.45) * mm, "end": v(-1.36, 30.37) * mm});
            skLineSegment(sketch, "E3.0.8.7", {"start": v(-6.44, 27.83) * mm, "end": v(-1.36, 27.83) * mm});
            skLineSegment(sketch, "E3.3.8.7", {"start": v(-6.44, 22.75) * mm, "end": v(-1.36, 22.75) * mm});
            skLineSegment(sketch, "E3.6.8.7", {"start": v(-6.44, 27.83) * mm, "end": v(-6.44, 22.75) * mm});
            skLineSegment(sketch, "E3.9.8.7", {"start": v(-1.36, 27.83) * mm, "end": v(-1.36, 22.75) * mm});
            skLineSegment(sketch, "E3.0.8.8", {"start": v(-6.44, 20.2) * mm, "end": v(-1.36, 20.2) * mm});
            skLineSegment(sketch, "E3.3.8.8", {"start": v(-6.44, 15.13) * mm, "end": v(-1.36, 15.13) * mm});
            skLineSegment(sketch, "E3.6.8.8", {"start": v(-6.44, 20.2) * mm, "end": v(-6.44, 15.13) * mm});
            skLineSegment(sketch, "E3.9.8.8", {"start": v(-1.36, 20.2) * mm, "end": v(-1.36, 15.13) * mm});
            skLineSegment(sketch, "E3.0.8.9", {"start": v(-6.44, 12.59) * mm, "end": v(-1.36, 12.59) * mm});
            skLineSegment(sketch, "E3.3.8.9", {"start": v(-6.44, 7.5) * mm, "end": v(-1.36, 7.5) * mm});
            skLineSegment(sketch, "E3.6.8.9", {"start": v(-6.44, 12.59) * mm, "end": v(-6.44, 7.5) * mm});
            skLineSegment(sketch, "E3.9.8.9", {"start": v(-1.36, 12.59) * mm, "end": v(-1.36, 7.5) * mm});
            skLineSegment(sketch, "E3.0.8.10", {"start": v(-6.44, 4.97) * mm, "end": v(-1.36, 4.97) * mm});
            skLineSegment(sketch, "E3.3.8.10", {"start": v(-6.44, -0.11) * mm, "end": v(-1.36, -0.11) * mm});
            skLineSegment(sketch, "E3.6.8.10", {"start": v(-6.44, 4.97) * mm, "end": v(-6.44, -0.11) * mm});
            skLineSegment(sketch, "E3.9.8.10", {"start": v(-1.36, 4.97) * mm, "end": v(-1.36, -0.11) * mm});
            skLineSegment(sketch, "E3.0.8.11", {"start": v(-6.44, -2.65) * mm, "end": v(-1.36, -2.65) * mm});
            skLineSegment(sketch, "E3.3.8.11", {"start": v(-6.44, -7.73) * mm, "end": v(-1.36, -7.73) * mm});
            skLineSegment(sketch, "E3.6.8.11", {"start": v(-6.44, -2.65) * mm, "end": v(-6.44, -7.73) * mm});
            skLineSegment(sketch, "E3.9.8.11", {"start": v(-1.36, -2.65) * mm, "end": v(-1.36, -7.73) * mm});
            skLineSegment(sketch, "E3.0.8.12", {"start": v(-6.44, -10.27) * mm, "end": v(-1.36, -10.27) * mm});
            skLineSegment(sketch, "E3.3.8.12", {"start": v(-6.44, -15.35) * mm, "end": v(-1.36, -15.35) * mm});
            skLineSegment(sketch, "E3.6.8.12", {"start": v(-6.44, -10.27) * mm, "end": v(-6.44, -15.35) * mm});
            skLineSegment(sketch, "E3.9.8.12", {"start": v(-1.36, -10.27) * mm, "end": v(-1.36, -15.35) * mm});
            skLineSegment(sketch, "E3.0.8.13", {"start": v(-6.44, -17.9) * mm, "end": v(-1.36, -17.9) * mm});
            skLineSegment(sketch, "E3.3.8.13", {"start": v(-6.44, -22.97) * mm, "end": v(-1.36, -22.97) * mm});
            skLineSegment(sketch, "E3.6.8.13", {"start": v(-6.44, -17.9) * mm, "end": v(-6.44, -22.97) * mm});
            skLineSegment(sketch, "E3.9.8.13", {"start": v(-1.36, -17.9) * mm, "end": v(-1.36, -22.97) * mm});
            skLineSegment(sketch, "E3.0.8.14", {"start": v(-6.44, -25.51) * mm, "end": v(-1.36, -25.51) * mm});
            skLineSegment(sketch, "E3.3.8.14", {"start": v(-6.44, -30.6) * mm, "end": v(-1.36, -30.6) * mm});
            skLineSegment(sketch, "E3.6.8.14", {"start": v(-6.44, -25.51) * mm, "end": v(-6.44, -30.6) * mm});
            skLineSegment(sketch, "E3.9.8.14", {"start": v(-1.36, -25.51) * mm, "end": v(-1.36, -30.6) * mm});
            skLineSegment(sketch, "E3.0.8.15", {"start": v(-6.44, -33.13) * mm, "end": v(-1.36, -33.13) * mm});
            skLineSegment(sketch, "E3.3.8.15", {"start": v(-6.44, -38.21) * mm, "end": v(-1.36, -38.21) * mm});
            skLineSegment(sketch, "E3.6.8.15", {"start": v(-6.44, -33.13) * mm, "end": v(-6.44, -38.21) * mm});
            skLineSegment(sketch, "E3.9.8.15", {"start": v(-1.36, -33.13) * mm, "end": v(-1.36, -38.21) * mm});
            skLineSegment(sketch, "E3.0.8.16", {"start": v(-6.44, -40.75) * mm, "end": v(-1.36, -40.75) * mm});
            skLineSegment(sketch, "E3.3.8.16", {"start": v(-6.44, -45.83) * mm, "end": v(-1.36, -45.83) * mm});
            skLineSegment(sketch, "E3.6.8.16", {"start": v(-6.44, -40.75) * mm, "end": v(-6.44, -45.83) * mm});
            skLineSegment(sketch, "E3.9.8.16", {"start": v(-1.36, -40.75) * mm, "end": v(-1.36, -45.83) * mm});
            skLineSegment(sketch, "E3.0.8.17", {"start": v(-6.44, -48.37) * mm, "end": v(-1.36, -48.37) * mm});
            skLineSegment(sketch, "E3.3.8.17", {"start": v(-6.44, -53.45) * mm, "end": v(-1.36, -53.45) * mm});
            skLineSegment(sketch, "E3.6.8.17", {"start": v(-6.44, -48.37) * mm, "end": v(-6.44, -53.45) * mm});
            skLineSegment(sketch, "E3.9.8.17", {"start": v(-1.36, -48.37) * mm, "end": v(-1.36, -53.45) * mm});
            skLineSegment(sketch, "E3.0.8.18", {"start": v(-6.44, -56) * mm, "end": v(-1.36, -56) * mm});
            skLineSegment(sketch, "E3.3.8.18", {"start": v(-6.44, -61.07) * mm, "end": v(-1.36, -61.07) * mm});
            skLineSegment(sketch, "E3.6.8.18", {"start": v(-6.44, -56) * mm, "end": v(-6.44, -61.07) * mm});
            skLineSegment(sketch, "E3.9.8.18", {"start": v(-1.36, -56) * mm, "end": v(-1.36, -61.07) * mm});
            skLineSegment(sketch, "E3.0.8.19", {"start": v(-6.44, -63.61) * mm, "end": v(-1.36, -63.61) * mm});
            skLineSegment(sketch, "E3.3.8.19", {"start": v(-6.44, -68.7) * mm, "end": v(-1.36, -68.7) * mm});
            skLineSegment(sketch, "E3.6.8.19", {"start": v(-6.44, -63.61) * mm, "end": v(-6.44, -68.7) * mm});
            skLineSegment(sketch, "E3.9.8.19", {"start": v(-1.36, -63.61) * mm, "end": v(-1.36, -68.7) * mm});
            skLineSegment(sketch, "E3.0.8.20", {"start": v(-6.44, -71.23) * mm, "end": v(-1.36, -71.23) * mm});
            skLineSegment(sketch, "E3.3.8.20", {"start": v(-6.44, -76.31) * mm, "end": v(-1.36, -76.31) * mm});
            skLineSegment(sketch, "E3.6.8.20", {"start": v(-6.44, -71.23) * mm, "end": v(-6.44, -76.31) * mm});
            skLineSegment(sketch, "E3.9.8.20", {"start": v(-1.36, -71.23) * mm, "end": v(-1.36, -76.31) * mm});
            skLineSegment(sketch, "E3.0.8.21", {"start": v(-6.44, -78.85) * mm, "end": v(-1.36, -78.85) * mm});
            skLineSegment(sketch, "E3.3.8.21", {"start": v(-6.44, -83.93) * mm, "end": v(-1.36, -83.93) * mm});
            skLineSegment(sketch, "E3.6.8.21", {"start": v(-6.44, -78.85) * mm, "end": v(-6.44, -83.93) * mm});
            skLineSegment(sketch, "E3.9.8.21", {"start": v(-1.36, -78.85) * mm, "end": v(-1.36, -83.93) * mm});
            skLineSegment(sketch, "E3.0.9.0", {"start": v(1.18, 81.17) * mm, "end": v(6.26, 81.17) * mm});
            skLineSegment(sketch, "E3.3.9.0", {"start": v(1.18, 76.09) * mm, "end": v(6.26, 76.09) * mm});
            skLineSegment(sketch, "E3.6.9.0", {"start": v(1.18, 81.17) * mm, "end": v(1.18, 76.09) * mm});
            skLineSegment(sketch, "E3.9.9.0", {"start": v(6.26, 81.17) * mm, "end": v(6.26, 76.09) * mm});
            skLineSegment(sketch, "E3.0.9.1", {"start": v(1.18, 73.55) * mm, "end": v(6.26, 73.55) * mm});
            skLineSegment(sketch, "E3.3.9.1", {"start": v(1.18, 68.47) * mm, "end": v(6.26, 68.47) * mm});
            skLineSegment(sketch, "E3.6.9.1", {"start": v(1.18, 73.55) * mm, "end": v(1.18, 68.47) * mm});
            skLineSegment(sketch, "E3.9.9.1", {"start": v(6.26, 73.55) * mm, "end": v(6.26, 68.47) * mm});
            skLineSegment(sketch, "E3.0.9.2", {"start": v(1.18, 65.93) * mm, "end": v(6.26, 65.93) * mm});
            skLineSegment(sketch, "E3.3.9.2", {"start": v(1.18, 60.85) * mm, "end": v(6.26, 60.85) * mm});
            skLineSegment(sketch, "E3.6.9.2", {"start": v(1.18, 65.93) * mm, "end": v(1.18, 60.85) * mm});
            skLineSegment(sketch, "E3.9.9.2", {"start": v(6.26, 65.93) * mm, "end": v(6.26, 60.85) * mm});
            skLineSegment(sketch, "E3.0.9.3", {"start": v(1.18, 58.3) * mm, "end": v(6.26, 58.3) * mm});
            skLineSegment(sketch, "E3.3.9.3", {"start": v(1.18, 53.23) * mm, "end": v(6.26, 53.23) * mm});
            skLineSegment(sketch, "E3.6.9.3", {"start": v(1.18, 58.3) * mm, "end": v(1.18, 53.23) * mm});
            skLineSegment(sketch, "E3.9.9.3", {"start": v(6.26, 58.3) * mm, "end": v(6.26, 53.23) * mm});
            skLineSegment(sketch, "E3.0.9.4", {"start": v(1.18, 50.69) * mm, "end": v(6.26, 50.69) * mm});
            skLineSegment(sketch, "E3.3.9.4", {"start": v(1.18, 45.6) * mm, "end": v(6.26, 45.6) * mm});
            skLineSegment(sketch, "E3.6.9.4", {"start": v(1.18, 50.69) * mm, "end": v(1.18, 45.6) * mm});
            skLineSegment(sketch, "E3.9.9.4", {"start": v(6.26, 50.69) * mm, "end": v(6.26, 45.6) * mm});
            skLineSegment(sketch, "E3.0.9.5", {"start": v(1.18, 43.07) * mm, "end": v(6.26, 43.07) * mm});
            skLineSegment(sketch, "E3.3.9.5", {"start": v(1.18, 37.99) * mm, "end": v(6.26, 37.99) * mm});
            skLineSegment(sketch, "E3.6.9.5", {"start": v(1.18, 43.07) * mm, "end": v(1.18, 37.99) * mm});
            skLineSegment(sketch, "E3.9.9.5", {"start": v(6.26, 43.07) * mm, "end": v(6.26, 37.99) * mm});
            skLineSegment(sketch, "E3.0.9.6", {"start": v(1.18, 35.45) * mm, "end": v(6.26, 35.45) * mm});
            skLineSegment(sketch, "E3.3.9.6", {"start": v(1.18, 30.37) * mm, "end": v(6.26, 30.37) * mm});
            skLineSegment(sketch, "E3.6.9.6", {"start": v(1.18, 35.45) * mm, "end": v(1.18, 30.37) * mm});
            skLineSegment(sketch, "E3.9.9.6", {"start": v(6.26, 35.45) * mm, "end": v(6.26, 30.37) * mm});
            skLineSegment(sketch, "E3.0.9.7", {"start": v(1.18, 27.83) * mm, "end": v(6.26, 27.83) * mm});
            skLineSegment(sketch, "E3.3.9.7", {"start": v(1.18, 22.75) * mm, "end": v(6.26, 22.75) * mm});
            skLineSegment(sketch, "E3.6.9.7", {"start": v(1.18, 27.83) * mm, "end": v(1.18, 22.75) * mm});
            skLineSegment(sketch, "E3.9.9.7", {"start": v(6.26, 27.83) * mm, "end": v(6.26, 22.75) * mm});
            skLineSegment(sketch, "E3.0.9.8", {"start": v(1.18, 20.2) * mm, "end": v(6.26, 20.2) * mm});
            skLineSegment(sketch, "E3.3.9.8", {"start": v(1.18, 15.13) * mm, "end": v(6.26, 15.13) * mm});
            skLineSegment(sketch, "E3.6.9.8", {"start": v(1.18, 20.2) * mm, "end": v(1.18, 15.13) * mm});
            skLineSegment(sketch, "E3.9.9.8", {"start": v(6.26, 20.2) * mm, "end": v(6.26, 15.13) * mm});
            skLineSegment(sketch, "E3.0.9.9", {"start": v(1.18, 12.59) * mm, "end": v(6.26, 12.59) * mm});
            skLineSegment(sketch, "E3.3.9.9", {"start": v(1.18, 7.5) * mm, "end": v(6.26, 7.5) * mm});
            skLineSegment(sketch, "E3.6.9.9", {"start": v(1.18, 12.59) * mm, "end": v(1.18, 7.5) * mm});
            skLineSegment(sketch, "E3.9.9.9", {"start": v(6.26, 12.59) * mm, "end": v(6.26, 7.5) * mm});
            skLineSegment(sketch, "E3.0.9.10", {"start": v(1.18, 4.97) * mm, "end": v(6.26, 4.97) * mm});
            skLineSegment(sketch, "E3.3.9.10", {"start": v(1.18, -0.11) * mm, "end": v(6.26, -0.11) * mm});
            skLineSegment(sketch, "E3.6.9.10", {"start": v(1.18, 4.97) * mm, "end": v(1.18, -0.11) * mm});
            skLineSegment(sketch, "E3.9.9.10", {"start": v(6.26, 4.97) * mm, "end": v(6.26, -0.11) * mm});
            skLineSegment(sketch, "E3.0.9.11", {"start": v(1.18, -2.65) * mm, "end": v(6.26, -2.65) * mm});
            skLineSegment(sketch, "E3.3.9.11", {"start": v(1.18, -7.73) * mm, "end": v(6.26, -7.73) * mm});
            skLineSegment(sketch, "E3.6.9.11", {"start": v(1.18, -2.65) * mm, "end": v(1.18, -7.73) * mm});
            skLineSegment(sketch, "E3.9.9.11", {"start": v(6.26, -2.65) * mm, "end": v(6.26, -7.73) * mm});
            skLineSegment(sketch, "E3.0.9.12", {"start": v(1.18, -10.27) * mm, "end": v(6.26, -10.27) * mm});
            skLineSegment(sketch, "E3.3.9.12", {"start": v(1.18, -15.35) * mm, "end": v(6.26, -15.35) * mm});
            skLineSegment(sketch, "E3.6.9.12", {"start": v(1.18, -10.27) * mm, "end": v(1.18, -15.35) * mm});
            skLineSegment(sketch, "E3.9.9.12", {"start": v(6.26, -10.27) * mm, "end": v(6.26, -15.35) * mm});
            skLineSegment(sketch, "E3.0.9.13", {"start": v(1.18, -17.9) * mm, "end": v(6.26, -17.9) * mm});
            skLineSegment(sketch, "E3.3.9.13", {"start": v(1.18, -22.97) * mm, "end": v(6.26, -22.97) * mm});
            skLineSegment(sketch, "E3.6.9.13", {"start": v(1.18, -17.9) * mm, "end": v(1.18, -22.97) * mm});
            skLineSegment(sketch, "E3.9.9.13", {"start": v(6.26, -17.9) * mm, "end": v(6.26, -22.97) * mm});
            skLineSegment(sketch, "E3.0.9.14", {"start": v(1.18, -25.51) * mm, "end": v(6.26, -25.51) * mm});
            skLineSegment(sketch, "E3.3.9.14", {"start": v(1.18, -30.6) * mm, "end": v(6.26, -30.6) * mm});
            skLineSegment(sketch, "E3.6.9.14", {"start": v(1.18, -25.51) * mm, "end": v(1.18, -30.6) * mm});
            skLineSegment(sketch, "E3.9.9.14", {"start": v(6.26, -25.51) * mm, "end": v(6.26, -30.6) * mm});
            skLineSegment(sketch, "E3.0.9.15", {"start": v(1.18, -33.13) * mm, "end": v(6.26, -33.13) * mm});
            skLineSegment(sketch, "E3.3.9.15", {"start": v(1.18, -38.21) * mm, "end": v(6.26, -38.21) * mm});
            skLineSegment(sketch, "E3.6.9.15", {"start": v(1.18, -33.13) * mm, "end": v(1.18, -38.21) * mm});
            skLineSegment(sketch, "E3.9.9.15", {"start": v(6.26, -33.13) * mm, "end": v(6.26, -38.21) * mm});
            skLineSegment(sketch, "E3.0.9.16", {"start": v(1.18, -40.75) * mm, "end": v(6.26, -40.75) * mm});
            skLineSegment(sketch, "E3.3.9.16", {"start": v(1.18, -45.83) * mm, "end": v(6.26, -45.83) * mm});
            skLineSegment(sketch, "E3.6.9.16", {"start": v(1.18, -40.75) * mm, "end": v(1.18, -45.83) * mm});
            skLineSegment(sketch, "E3.9.9.16", {"start": v(6.26, -40.75) * mm, "end": v(6.26, -45.83) * mm});
            skLineSegment(sketch, "E3.0.9.17", {"start": v(1.18, -48.37) * mm, "end": v(6.26, -48.37) * mm});
            skLineSegment(sketch, "E3.3.9.17", {"start": v(1.18, -53.45) * mm, "end": v(6.26, -53.45) * mm});
            skLineSegment(sketch, "E3.6.9.17", {"start": v(1.18, -48.37) * mm, "end": v(1.18, -53.45) * mm});
            skLineSegment(sketch, "E3.9.9.17", {"start": v(6.26, -48.37) * mm, "end": v(6.26, -53.45) * mm});
            skLineSegment(sketch, "E3.0.9.18", {"start": v(1.18, -56) * mm, "end": v(6.26, -56) * mm});
            skLineSegment(sketch, "E3.3.9.18", {"start": v(1.18, -61.07) * mm, "end": v(6.26, -61.07) * mm});
            skLineSegment(sketch, "E3.6.9.18", {"start": v(1.18, -56) * mm, "end": v(1.18, -61.07) * mm});
            skLineSegment(sketch, "E3.9.9.18", {"start": v(6.26, -56) * mm, "end": v(6.26, -61.07) * mm});
            skLineSegment(sketch, "E3.0.9.19", {"start": v(1.18, -63.61) * mm, "end": v(6.26, -63.61) * mm});
            skLineSegment(sketch, "E3.3.9.19", {"start": v(1.18, -68.7) * mm, "end": v(6.26, -68.7) * mm});
            skLineSegment(sketch, "E3.6.9.19", {"start": v(1.18, -63.61) * mm, "end": v(1.18, -68.7) * mm});
            skLineSegment(sketch, "E3.9.9.19", {"start": v(6.26, -63.61) * mm, "end": v(6.26, -68.7) * mm});
            skLineSegment(sketch, "E3.0.9.20", {"start": v(1.18, -71.23) * mm, "end": v(6.26, -71.23) * mm});
            skLineSegment(sketch, "E3.3.9.20", {"start": v(1.18, -76.31) * mm, "end": v(6.26, -76.31) * mm});
            skLineSegment(sketch, "E3.6.9.20", {"start": v(1.18, -71.23) * mm, "end": v(1.18, -76.31) * mm});
            skLineSegment(sketch, "E3.9.9.20", {"start": v(6.26, -71.23) * mm, "end": v(6.26, -76.31) * mm});
            skLineSegment(sketch, "E3.0.9.21", {"start": v(1.18, -78.85) * mm, "end": v(6.26, -78.85) * mm});
            skLineSegment(sketch, "E3.3.9.21", {"start": v(1.18, -83.93) * mm, "end": v(6.26, -83.93) * mm});
            skLineSegment(sketch, "E3.6.9.21", {"start": v(1.18, -78.85) * mm, "end": v(1.18, -83.93) * mm});
            skLineSegment(sketch, "E3.9.9.21", {"start": v(6.26, -78.85) * mm, "end": v(6.26, -83.93) * mm});
            skLineSegment(sketch, "E3.0.10.0", {"start": v(8.8, 81.17) * mm, "end": v(13.88, 81.17) * mm});
            skLineSegment(sketch, "E3.3.10.0", {"start": v(8.8, 76.09) * mm, "end": v(13.88, 76.09) * mm});
            skLineSegment(sketch, "E3.6.10.0", {"start": v(8.8, 81.17) * mm, "end": v(8.8, 76.09) * mm});
            skLineSegment(sketch, "E3.9.10.0", {"start": v(13.88, 81.17) * mm, "end": v(13.88, 76.09) * mm});
            skLineSegment(sketch, "E3.0.10.1", {"start": v(8.8, 73.55) * mm, "end": v(13.88, 73.55) * mm});
            skLineSegment(sketch, "E3.3.10.1", {"start": v(8.8, 68.47) * mm, "end": v(13.88, 68.47) * mm});
            skLineSegment(sketch, "E3.6.10.1", {"start": v(8.8, 73.55) * mm, "end": v(8.8, 68.47) * mm});
            skLineSegment(sketch, "E3.9.10.1", {"start": v(13.88, 73.55) * mm, "end": v(13.88, 68.47) * mm});
            skLineSegment(sketch, "E3.0.10.2", {"start": v(8.8, 65.93) * mm, "end": v(13.88, 65.93) * mm});
            skLineSegment(sketch, "E3.3.10.2", {"start": v(8.8, 60.85) * mm, "end": v(13.88, 60.85) * mm});
            skLineSegment(sketch, "E3.6.10.2", {"start": v(8.8, 65.93) * mm, "end": v(8.8, 60.85) * mm});
            skLineSegment(sketch, "E3.9.10.2", {"start": v(13.88, 65.93) * mm, "end": v(13.88, 60.85) * mm});
            skLineSegment(sketch, "E3.0.10.3", {"start": v(8.8, 58.3) * mm, "end": v(13.88, 58.3) * mm});
            skLineSegment(sketch, "E3.3.10.3", {"start": v(8.8, 53.23) * mm, "end": v(13.88, 53.23) * mm});
            skLineSegment(sketch, "E3.6.10.3", {"start": v(8.8, 58.3) * mm, "end": v(8.8, 53.23) * mm});
            skLineSegment(sketch, "E3.9.10.3", {"start": v(13.88, 58.3) * mm, "end": v(13.88, 53.23) * mm});
            skLineSegment(sketch, "E3.0.10.4", {"start": v(8.8, 50.69) * mm, "end": v(13.88, 50.69) * mm});
            skLineSegment(sketch, "E3.3.10.4", {"start": v(8.8, 45.6) * mm, "end": v(13.88, 45.6) * mm});
            skLineSegment(sketch, "E3.6.10.4", {"start": v(8.8, 50.69) * mm, "end": v(8.8, 45.6) * mm});
            skLineSegment(sketch, "E3.9.10.4", {"start": v(13.88, 50.69) * mm, "end": v(13.88, 45.6) * mm});
            skLineSegment(sketch, "E3.0.10.5", {"start": v(8.8, 43.07) * mm, "end": v(13.88, 43.07) * mm});
            skLineSegment(sketch, "E3.3.10.5", {"start": v(8.8, 37.99) * mm, "end": v(13.88, 37.99) * mm});
            skLineSegment(sketch, "E3.6.10.5", {"start": v(8.8, 43.07) * mm, "end": v(8.8, 37.99) * mm});
            skLineSegment(sketch, "E3.9.10.5", {"start": v(13.88, 43.07) * mm, "end": v(13.88, 37.99) * mm});
            skLineSegment(sketch, "E3.0.10.6", {"start": v(8.8, 35.45) * mm, "end": v(13.88, 35.45) * mm});
            skLineSegment(sketch, "E3.3.10.6", {"start": v(8.8, 30.37) * mm, "end": v(13.88, 30.37) * mm});
            skLineSegment(sketch, "E3.6.10.6", {"start": v(8.8, 35.45) * mm, "end": v(8.8, 30.37) * mm});
            skLineSegment(sketch, "E3.9.10.6", {"start": v(13.88, 35.45) * mm, "end": v(13.88, 30.37) * mm});
            skLineSegment(sketch, "E3.0.10.7", {"start": v(8.8, 27.83) * mm, "end": v(13.88, 27.83) * mm});
            skLineSegment(sketch, "E3.3.10.7", {"start": v(8.8, 22.75) * mm, "end": v(13.88, 22.75) * mm});
            skLineSegment(sketch, "E3.6.10.7", {"start": v(8.8, 27.83) * mm, "end": v(8.8, 22.75) * mm});
            skLineSegment(sketch, "E3.9.10.7", {"start": v(13.88, 27.83) * mm, "end": v(13.88, 22.75) * mm});
            skLineSegment(sketch, "E3.0.10.8", {"start": v(8.8, 20.2) * mm, "end": v(13.88, 20.2) * mm});
            skLineSegment(sketch, "E3.3.10.8", {"start": v(8.8, 15.13) * mm, "end": v(13.88, 15.13) * mm});
            skLineSegment(sketch, "E3.6.10.8", {"start": v(8.8, 20.2) * mm, "end": v(8.8, 15.13) * mm});
            skLineSegment(sketch, "E3.9.10.8", {"start": v(13.88, 20.2) * mm, "end": v(13.88, 15.13) * mm});
            skLineSegment(sketch, "E3.0.10.9", {"start": v(8.8, 12.59) * mm, "end": v(13.88, 12.59) * mm});
            skLineSegment(sketch, "E3.3.10.9", {"start": v(8.8, 7.5) * mm, "end": v(13.88, 7.5) * mm});
            skLineSegment(sketch, "E3.6.10.9", {"start": v(8.8, 12.59) * mm, "end": v(8.8, 7.5) * mm});
            skLineSegment(sketch, "E3.9.10.9", {"start": v(13.88, 12.59) * mm, "end": v(13.88, 7.5) * mm});
            skLineSegment(sketch, "E3.0.10.10", {"start": v(8.8, 4.97) * mm, "end": v(13.88, 4.97) * mm});
            skLineSegment(sketch, "E3.3.10.10", {"start": v(8.8, -0.11) * mm, "end": v(13.88, -0.11) * mm});
            skLineSegment(sketch, "E3.6.10.10", {"start": v(8.8, 4.97) * mm, "end": v(8.8, -0.11) * mm});
            skLineSegment(sketch, "E3.9.10.10", {"start": v(13.88, 4.97) * mm, "end": v(13.88, -0.11) * mm});
            skLineSegment(sketch, "E3.0.10.11", {"start": v(8.8, -2.65) * mm, "end": v(13.88, -2.65) * mm});
            skLineSegment(sketch, "E3.3.10.11", {"start": v(8.8, -7.73) * mm, "end": v(13.88, -7.73) * mm});
            skLineSegment(sketch, "E3.6.10.11", {"start": v(8.8, -2.65) * mm, "end": v(8.8, -7.73) * mm});
            skLineSegment(sketch, "E3.9.10.11", {"start": v(13.88, -2.65) * mm, "end": v(13.88, -7.73) * mm});
            skLineSegment(sketch, "E3.0.10.12", {"start": v(8.8, -10.27) * mm, "end": v(13.88, -10.27) * mm});
            skLineSegment(sketch, "E3.3.10.12", {"start": v(8.8, -15.35) * mm, "end": v(13.88, -15.35) * mm});
            skLineSegment(sketch, "E3.6.10.12", {"start": v(8.8, -10.27) * mm, "end": v(8.8, -15.35) * mm});
            skLineSegment(sketch, "E3.9.10.12", {"start": v(13.88, -10.27) * mm, "end": v(13.88, -15.35) * mm});
            skLineSegment(sketch, "E3.0.10.13", {"start": v(8.8, -17.9) * mm, "end": v(13.88, -17.9) * mm});
            skLineSegment(sketch, "E3.3.10.13", {"start": v(8.8, -22.97) * mm, "end": v(13.88, -22.97) * mm});
            skLineSegment(sketch, "E3.6.10.13", {"start": v(8.8, -17.9) * mm, "end": v(8.8, -22.97) * mm});
            skLineSegment(sketch, "E3.9.10.13", {"start": v(13.88, -17.9) * mm, "end": v(13.88, -22.97) * mm});
            skLineSegment(sketch, "E3.0.10.14", {"start": v(8.8, -25.51) * mm, "end": v(13.88, -25.51) * mm});
            skLineSegment(sketch, "E3.3.10.14", {"start": v(8.8, -30.6) * mm, "end": v(13.88, -30.6) * mm});
            skLineSegment(sketch, "E3.6.10.14", {"start": v(8.8, -25.51) * mm, "end": v(8.8, -30.6) * mm});
            skLineSegment(sketch, "E3.9.10.14", {"start": v(13.88, -25.51) * mm, "end": v(13.88, -30.6) * mm});
            skLineSegment(sketch, "E3.0.10.15", {"start": v(8.8, -33.13) * mm, "end": v(13.88, -33.13) * mm});
            skLineSegment(sketch, "E3.3.10.15", {"start": v(8.8, -38.21) * mm, "end": v(13.88, -38.21) * mm});
            skLineSegment(sketch, "E3.6.10.15", {"start": v(8.8, -33.13) * mm, "end": v(8.8, -38.21) * mm});
            skLineSegment(sketch, "E3.9.10.15", {"start": v(13.88, -33.13) * mm, "end": v(13.88, -38.21) * mm});
            skLineSegment(sketch, "E3.0.10.16", {"start": v(8.8, -40.75) * mm, "end": v(13.88, -40.75) * mm});
            skLineSegment(sketch, "E3.3.10.16", {"start": v(8.8, -45.83) * mm, "end": v(13.88, -45.83) * mm});
            skLineSegment(sketch, "E3.6.10.16", {"start": v(8.8, -40.75) * mm, "end": v(8.8, -45.83) * mm});
            skLineSegment(sketch, "E3.9.10.16", {"start": v(13.88, -40.75) * mm, "end": v(13.88, -45.83) * mm});
            skLineSegment(sketch, "E3.0.10.17", {"start": v(8.8, -48.37) * mm, "end": v(13.88, -48.37) * mm});
            skLineSegment(sketch, "E3.3.10.17", {"start": v(8.8, -53.45) * mm, "end": v(13.88, -53.45) * mm});
            skLineSegment(sketch, "E3.6.10.17", {"start": v(8.8, -48.37) * mm, "end": v(8.8, -53.45) * mm});
            skLineSegment(sketch, "E3.9.10.17", {"start": v(13.88, -48.37) * mm, "end": v(13.88, -53.45) * mm});
            skLineSegment(sketch, "E3.0.10.18", {"start": v(8.8, -56) * mm, "end": v(13.88, -56) * mm});
            skLineSegment(sketch, "E3.3.10.18", {"start": v(8.8, -61.07) * mm, "end": v(13.88, -61.07) * mm});
            skLineSegment(sketch, "E3.6.10.18", {"start": v(8.8, -56) * mm, "end": v(8.8, -61.07) * mm});
            skLineSegment(sketch, "E3.9.10.18", {"start": v(13.88, -56) * mm, "end": v(13.88, -61.07) * mm});
            skLineSegment(sketch, "E3.0.10.19", {"start": v(8.8, -63.61) * mm, "end": v(13.88, -63.61) * mm});
            skLineSegment(sketch, "E3.3.10.19", {"start": v(8.8, -68.7) * mm, "end": v(13.88, -68.7) * mm});
            skLineSegment(sketch, "E3.6.10.19", {"start": v(8.8, -63.61) * mm, "end": v(8.8, -68.7) * mm});
            skLineSegment(sketch, "E3.9.10.19", {"start": v(13.88, -63.61) * mm, "end": v(13.88, -68.7) * mm});
            skLineSegment(sketch, "E3.0.10.20", {"start": v(8.8, -71.23) * mm, "end": v(13.88, -71.23) * mm});
            skLineSegment(sketch, "E3.3.10.20", {"start": v(8.8, -76.31) * mm, "end": v(13.88, -76.31) * mm});
            skLineSegment(sketch, "E3.6.10.20", {"start": v(8.8, -71.23) * mm, "end": v(8.8, -76.31) * mm});
            skLineSegment(sketch, "E3.9.10.20", {"start": v(13.88, -71.23) * mm, "end": v(13.88, -76.31) * mm});
            skLineSegment(sketch, "E3.0.10.21", {"start": v(8.8, -78.85) * mm, "end": v(13.88, -78.85) * mm});
            skLineSegment(sketch, "E3.3.10.21", {"start": v(8.8, -83.93) * mm, "end": v(13.88, -83.93) * mm});
            skLineSegment(sketch, "E3.6.10.21", {"start": v(8.8, -78.85) * mm, "end": v(8.8, -83.93) * mm});
            skLineSegment(sketch, "E3.9.10.21", {"start": v(13.88, -78.85) * mm, "end": v(13.88, -83.93) * mm});
            skLineSegment(sketch, "E3.0.11.0", {"start": v(16.42, 81.17) * mm, "end": v(21.5, 81.17) * mm});
            skLineSegment(sketch, "E3.3.11.0", {"start": v(16.42, 76.09) * mm, "end": v(21.5, 76.09) * mm});
            skLineSegment(sketch, "E3.6.11.0", {"start": v(16.42, 81.17) * mm, "end": v(16.42, 76.09) * mm});
            skLineSegment(sketch, "E3.9.11.0", {"start": v(21.5, 81.17) * mm, "end": v(21.5, 76.09) * mm});
            skLineSegment(sketch, "E3.0.11.1", {"start": v(16.42, 73.55) * mm, "end": v(21.5, 73.55) * mm});
            skLineSegment(sketch, "E3.3.11.1", {"start": v(16.42, 68.47) * mm, "end": v(21.5, 68.47) * mm});
            skLineSegment(sketch, "E3.6.11.1", {"start": v(16.42, 73.55) * mm, "end": v(16.42, 68.47) * mm});
            skLineSegment(sketch, "E3.9.11.1", {"start": v(21.5, 73.55) * mm, "end": v(21.5, 68.47) * mm});
            skLineSegment(sketch, "E3.0.11.2", {"start": v(16.42, 65.93) * mm, "end": v(21.5, 65.93) * mm});
            skLineSegment(sketch, "E3.3.11.2", {"start": v(16.42, 60.85) * mm, "end": v(21.5, 60.85) * mm});
            skLineSegment(sketch, "E3.6.11.2", {"start": v(16.42, 65.93) * mm, "end": v(16.42, 60.85) * mm});
            skLineSegment(sketch, "E3.9.11.2", {"start": v(21.5, 65.93) * mm, "end": v(21.5, 60.85) * mm});
            skLineSegment(sketch, "E3.0.11.3", {"start": v(16.42, 58.3) * mm, "end": v(21.5, 58.3) * mm});
            skLineSegment(sketch, "E3.3.11.3", {"start": v(16.42, 53.23) * mm, "end": v(21.5, 53.23) * mm});
            skLineSegment(sketch, "E3.6.11.3", {"start": v(16.42, 58.3) * mm, "end": v(16.42, 53.23) * mm});
            skLineSegment(sketch, "E3.9.11.3", {"start": v(21.5, 58.3) * mm, "end": v(21.5, 53.23) * mm});
            skLineSegment(sketch, "E3.0.11.4", {"start": v(16.42, 50.69) * mm, "end": v(21.5, 50.69) * mm});
            skLineSegment(sketch, "E3.3.11.4", {"start": v(16.42, 45.6) * mm, "end": v(21.5, 45.6) * mm});
            skLineSegment(sketch, "E3.6.11.4", {"start": v(16.42, 50.69) * mm, "end": v(16.42, 45.6) * mm});
            skLineSegment(sketch, "E3.9.11.4", {"start": v(21.5, 50.69) * mm, "end": v(21.5, 45.6) * mm});
            skLineSegment(sketch, "E3.0.11.5", {"start": v(16.42, 43.07) * mm, "end": v(21.5, 43.07) * mm});
            skLineSegment(sketch, "E3.3.11.5", {"start": v(16.42, 37.99) * mm, "end": v(21.5, 37.99) * mm});
            skLineSegment(sketch, "E3.6.11.5", {"start": v(16.42, 43.07) * mm, "end": v(16.42, 37.99) * mm});
            skLineSegment(sketch, "E3.9.11.5", {"start": v(21.5, 43.07) * mm, "end": v(21.5, 37.99) * mm});
            skLineSegment(sketch, "E3.0.11.6", {"start": v(16.42, 35.45) * mm, "end": v(21.5, 35.45) * mm});
            skLineSegment(sketch, "E3.3.11.6", {"start": v(16.42, 30.37) * mm, "end": v(21.5, 30.37) * mm});
            skLineSegment(sketch, "E3.6.11.6", {"start": v(16.42, 35.45) * mm, "end": v(16.42, 30.37) * mm});
            skLineSegment(sketch, "E3.9.11.6", {"start": v(21.5, 35.45) * mm, "end": v(21.5, 30.37) * mm});
            skLineSegment(sketch, "E3.0.11.7", {"start": v(16.42, 27.83) * mm, "end": v(21.5, 27.83) * mm});
            skLineSegment(sketch, "E3.3.11.7", {"start": v(16.42, 22.75) * mm, "end": v(21.5, 22.75) * mm});
            skLineSegment(sketch, "E3.6.11.7", {"start": v(16.42, 27.83) * mm, "end": v(16.42, 22.75) * mm});
            skLineSegment(sketch, "E3.9.11.7", {"start": v(21.5, 27.83) * mm, "end": v(21.5, 22.75) * mm});
            skLineSegment(sketch, "E3.0.11.8", {"start": v(16.42, 20.2) * mm, "end": v(21.5, 20.2) * mm});
            skLineSegment(sketch, "E3.3.11.8", {"start": v(16.42, 15.13) * mm, "end": v(21.5, 15.13) * mm});
            skLineSegment(sketch, "E3.6.11.8", {"start": v(16.42, 20.2) * mm, "end": v(16.42, 15.13) * mm});
            skLineSegment(sketch, "E3.9.11.8", {"start": v(21.5, 20.2) * mm, "end": v(21.5, 15.13) * mm});
            skLineSegment(sketch, "E3.0.11.9", {"start": v(16.42, 12.59) * mm, "end": v(21.5, 12.59) * mm});
            skLineSegment(sketch, "E3.3.11.9", {"start": v(16.42, 7.5) * mm, "end": v(21.5, 7.5) * mm});
            skLineSegment(sketch, "E3.6.11.9", {"start": v(16.42, 12.59) * mm, "end": v(16.42, 7.5) * mm});
            skLineSegment(sketch, "E3.9.11.9", {"start": v(21.5, 12.59) * mm, "end": v(21.5, 7.5) * mm});
            skLineSegment(sketch, "E3.0.11.10", {"start": v(16.42, 4.97) * mm, "end": v(21.5, 4.97) * mm});
            skLineSegment(sketch, "E3.3.11.10", {"start": v(16.42, -0.11) * mm, "end": v(21.5, -0.11) * mm});
            skLineSegment(sketch, "E3.6.11.10", {"start": v(16.42, 4.97) * mm, "end": v(16.42, -0.11) * mm});
            skLineSegment(sketch, "E3.9.11.10", {"start": v(21.5, 4.97) * mm, "end": v(21.5, -0.11) * mm});
            skLineSegment(sketch, "E3.0.11.11", {"start": v(16.42, -2.65) * mm, "end": v(21.5, -2.65) * mm});
            skLineSegment(sketch, "E3.3.11.11", {"start": v(16.42, -7.73) * mm, "end": v(21.5, -7.73) * mm});
            skLineSegment(sketch, "E3.6.11.11", {"start": v(16.42, -2.65) * mm, "end": v(16.42, -7.73) * mm});
            skLineSegment(sketch, "E3.9.11.11", {"start": v(21.5, -2.65) * mm, "end": v(21.5, -7.73) * mm});
            skLineSegment(sketch, "E3.0.11.12", {"start": v(16.42, -10.27) * mm, "end": v(21.5, -10.27) * mm});
            skLineSegment(sketch, "E3.3.11.12", {"start": v(16.42, -15.35) * mm, "end": v(21.5, -15.35) * mm});
            skLineSegment(sketch, "E3.6.11.12", {"start": v(16.42, -10.27) * mm, "end": v(16.42, -15.35) * mm});
            skLineSegment(sketch, "E3.9.11.12", {"start": v(21.5, -10.27) * mm, "end": v(21.5, -15.35) * mm});
            skLineSegment(sketch, "E3.0.11.13", {"start": v(16.42, -17.9) * mm, "end": v(21.5, -17.9) * mm});
            skLineSegment(sketch, "E3.3.11.13", {"start": v(16.42, -22.97) * mm, "end": v(21.5, -22.97) * mm});
            skLineSegment(sketch, "E3.6.11.13", {"start": v(16.42, -17.9) * mm, "end": v(16.42, -22.97) * mm});
            skLineSegment(sketch, "E3.9.11.13", {"start": v(21.5, -17.9) * mm, "end": v(21.5, -22.97) * mm});
            skLineSegment(sketch, "E3.0.11.14", {"start": v(16.42, -25.51) * mm, "end": v(21.5, -25.51) * mm});
            skLineSegment(sketch, "E3.3.11.14", {"start": v(16.42, -30.6) * mm, "end": v(21.5, -30.6) * mm});
            skLineSegment(sketch, "E3.6.11.14", {"start": v(16.42, -25.51) * mm, "end": v(16.42, -30.6) * mm});
            skLineSegment(sketch, "E3.9.11.14", {"start": v(21.5, -25.51) * mm, "end": v(21.5, -30.6) * mm});
            skLineSegment(sketch, "E3.0.11.15", {"start": v(16.42, -33.13) * mm, "end": v(21.5, -33.13) * mm});
            skLineSegment(sketch, "E3.3.11.15", {"start": v(16.42, -38.21) * mm, "end": v(21.5, -38.21) * mm});
            skLineSegment(sketch, "E3.6.11.15", {"start": v(16.42, -33.13) * mm, "end": v(16.42, -38.21) * mm});
            skLineSegment(sketch, "E3.9.11.15", {"start": v(21.5, -33.13) * mm, "end": v(21.5, -38.21) * mm});
            skLineSegment(sketch, "E3.0.11.16", {"start": v(16.42, -40.75) * mm, "end": v(21.5, -40.75) * mm});
            skLineSegment(sketch, "E3.3.11.16", {"start": v(16.42, -45.83) * mm, "end": v(21.5, -45.83) * mm});
            skLineSegment(sketch, "E3.6.11.16", {"start": v(16.42, -40.75) * mm, "end": v(16.42, -45.83) * mm});
            skLineSegment(sketch, "E3.9.11.16", {"start": v(21.5, -40.75) * mm, "end": v(21.5, -45.83) * mm});
            skLineSegment(sketch, "E3.0.11.17", {"start": v(16.42, -48.37) * mm, "end": v(21.5, -48.37) * mm});
            skLineSegment(sketch, "E3.3.11.17", {"start": v(16.42, -53.45) * mm, "end": v(21.5, -53.45) * mm});
            skLineSegment(sketch, "E3.6.11.17", {"start": v(16.42, -48.37) * mm, "end": v(16.42, -53.45) * mm});
            skLineSegment(sketch, "E3.9.11.17", {"start": v(21.5, -48.37) * mm, "end": v(21.5, -53.45) * mm});
            skLineSegment(sketch, "E3.0.11.18", {"start": v(16.42, -56) * mm, "end": v(21.5, -56) * mm});
            skLineSegment(sketch, "E3.3.11.18", {"start": v(16.42, -61.07) * mm, "end": v(21.5, -61.07) * mm});
            skLineSegment(sketch, "E3.6.11.18", {"start": v(16.42, -56) * mm, "end": v(16.42, -61.07) * mm});
            skLineSegment(sketch, "E3.9.11.18", {"start": v(21.5, -56) * mm, "end": v(21.5, -61.07) * mm});
            skLineSegment(sketch, "E3.0.11.19", {"start": v(16.42, -63.61) * mm, "end": v(21.5, -63.61) * mm});
            skLineSegment(sketch, "E3.3.11.19", {"start": v(16.42, -68.7) * mm, "end": v(21.5, -68.7) * mm});
            skLineSegment(sketch, "E3.6.11.19", {"start": v(16.42, -63.61) * mm, "end": v(16.42, -68.7) * mm});
            skLineSegment(sketch, "E3.9.11.19", {"start": v(21.5, -63.61) * mm, "end": v(21.5, -68.7) * mm});
            skLineSegment(sketch, "E3.0.11.20", {"start": v(16.42, -71.23) * mm, "end": v(21.5, -71.23) * mm});
            skLineSegment(sketch, "E3.3.11.20", {"start": v(16.42, -76.31) * mm, "end": v(21.5, -76.31) * mm});
            skLineSegment(sketch, "E3.6.11.20", {"start": v(16.42, -71.23) * mm, "end": v(16.42, -76.31) * mm});
            skLineSegment(sketch, "E3.9.11.20", {"start": v(21.5, -71.23) * mm, "end": v(21.5, -76.31) * mm});
            skLineSegment(sketch, "E3.0.11.21", {"start": v(16.42, -78.85) * mm, "end": v(21.5, -78.85) * mm});
            skLineSegment(sketch, "E3.3.11.21", {"start": v(16.42, -83.93) * mm, "end": v(21.5, -83.93) * mm});
            skLineSegment(sketch, "E3.6.11.21", {"start": v(16.42, -78.85) * mm, "end": v(16.42, -83.93) * mm});
            skLineSegment(sketch, "E3.9.11.21", {"start": v(21.5, -78.85) * mm, "end": v(21.5, -83.93) * mm});
            skLineSegment(sketch, "E3.0.12.0", {"start": v(24.04, 81.17) * mm, "end": v(29.12, 81.17) * mm});
            skLineSegment(sketch, "E3.3.12.0", {"start": v(24.04, 76.09) * mm, "end": v(29.12, 76.09) * mm});
            skLineSegment(sketch, "E3.6.12.0", {"start": v(24.04, 81.17) * mm, "end": v(24.04, 76.09) * mm});
            skLineSegment(sketch, "E3.9.12.0", {"start": v(29.12, 81.17) * mm, "end": v(29.12, 76.09) * mm});
            skLineSegment(sketch, "E3.0.12.1", {"start": v(24.04, 73.55) * mm, "end": v(29.12, 73.55) * mm});
            skLineSegment(sketch, "E3.3.12.1", {"start": v(24.04, 68.47) * mm, "end": v(29.12, 68.47) * mm});
            skLineSegment(sketch, "E3.6.12.1", {"start": v(24.04, 73.55) * mm, "end": v(24.04, 68.47) * mm});
            skLineSegment(sketch, "E3.9.12.1", {"start": v(29.12, 73.55) * mm, "end": v(29.12, 68.47) * mm});
            skLineSegment(sketch, "E3.0.12.2", {"start": v(24.04, 65.93) * mm, "end": v(29.12, 65.93) * mm});
            skLineSegment(sketch, "E3.3.12.2", {"start": v(24.04, 60.85) * mm, "end": v(29.12, 60.85) * mm});
            skLineSegment(sketch, "E3.6.12.2", {"start": v(24.04, 65.93) * mm, "end": v(24.04, 60.85) * mm});
            skLineSegment(sketch, "E3.9.12.2", {"start": v(29.12, 65.93) * mm, "end": v(29.12, 60.85) * mm});
            skLineSegment(sketch, "E3.0.12.3", {"start": v(24.04, 58.3) * mm, "end": v(29.12, 58.3) * mm});
            skLineSegment(sketch, "E3.3.12.3", {"start": v(24.04, 53.23) * mm, "end": v(29.12, 53.23) * mm});
            skLineSegment(sketch, "E3.6.12.3", {"start": v(24.04, 58.3) * mm, "end": v(24.04, 53.23) * mm});
            skLineSegment(sketch, "E3.9.12.3", {"start": v(29.12, 58.3) * mm, "end": v(29.12, 53.23) * mm});
            skLineSegment(sketch, "E3.0.12.4", {"start": v(24.04, 50.69) * mm, "end": v(29.12, 50.69) * mm});
            skLineSegment(sketch, "E3.3.12.4", {"start": v(24.04, 45.6) * mm, "end": v(29.12, 45.6) * mm});
            skLineSegment(sketch, "E3.6.12.4", {"start": v(24.04, 50.69) * mm, "end": v(24.04, 45.6) * mm});
            skLineSegment(sketch, "E3.9.12.4", {"start": v(29.12, 50.69) * mm, "end": v(29.12, 45.6) * mm});
            skLineSegment(sketch, "E3.0.12.5", {"start": v(24.04, 43.07) * mm, "end": v(29.12, 43.07) * mm});
            skLineSegment(sketch, "E3.3.12.5", {"start": v(24.04, 37.99) * mm, "end": v(29.12, 37.99) * mm});
            skLineSegment(sketch, "E3.6.12.5", {"start": v(24.04, 43.07) * mm, "end": v(24.04, 37.99) * mm});
            skLineSegment(sketch, "E3.9.12.5", {"start": v(29.12, 43.07) * mm, "end": v(29.12, 37.99) * mm});
            skLineSegment(sketch, "E3.0.12.6", {"start": v(24.04, 35.45) * mm, "end": v(29.12, 35.45) * mm});
            skLineSegment(sketch, "E3.3.12.6", {"start": v(24.04, 30.37) * mm, "end": v(29.12, 30.37) * mm});
            skLineSegment(sketch, "E3.6.12.6", {"start": v(24.04, 35.45) * mm, "end": v(24.04, 30.37) * mm});
            skLineSegment(sketch, "E3.9.12.6", {"start": v(29.12, 35.45) * mm, "end": v(29.12, 30.37) * mm});
            skLineSegment(sketch, "E3.0.12.7", {"start": v(24.04, 27.83) * mm, "end": v(29.12, 27.83) * mm});
            skLineSegment(sketch, "E3.3.12.7", {"start": v(24.04, 22.75) * mm, "end": v(29.12, 22.75) * mm});
            skLineSegment(sketch, "E3.6.12.7", {"start": v(24.04, 27.83) * mm, "end": v(24.04, 22.75) * mm});
            skLineSegment(sketch, "E3.9.12.7", {"start": v(29.12, 27.83) * mm, "end": v(29.12, 22.75) * mm});
            skLineSegment(sketch, "E3.0.12.8", {"start": v(24.04, 20.2) * mm, "end": v(29.12, 20.2) * mm});
            skLineSegment(sketch, "E3.3.12.8", {"start": v(24.04, 15.13) * mm, "end": v(29.12, 15.13) * mm});
            skLineSegment(sketch, "E3.6.12.8", {"start": v(24.04, 20.2) * mm, "end": v(24.04, 15.13) * mm});
            skLineSegment(sketch, "E3.9.12.8", {"start": v(29.12, 20.2) * mm, "end": v(29.12, 15.13) * mm});
            skLineSegment(sketch, "E3.0.12.9", {"start": v(24.04, 12.59) * mm, "end": v(29.12, 12.59) * mm});
            skLineSegment(sketch, "E3.3.12.9", {"start": v(24.04, 7.5) * mm, "end": v(29.12, 7.5) * mm});
            skLineSegment(sketch, "E3.6.12.9", {"start": v(24.04, 12.59) * mm, "end": v(24.04, 7.5) * mm});
            skLineSegment(sketch, "E3.9.12.9", {"start": v(29.12, 12.59) * mm, "end": v(29.12, 7.5) * mm});
            skLineSegment(sketch, "E3.0.12.10", {"start": v(24.04, 4.97) * mm, "end": v(29.12, 4.97) * mm});
            skLineSegment(sketch, "E3.3.12.10", {"start": v(24.04, -0.11) * mm, "end": v(29.12, -0.11) * mm});
            skLineSegment(sketch, "E3.6.12.10", {"start": v(24.04, 4.97) * mm, "end": v(24.04, -0.11) * mm});
            skLineSegment(sketch, "E3.9.12.10", {"start": v(29.12, 4.97) * mm, "end": v(29.12, -0.11) * mm});
            skLineSegment(sketch, "E3.0.12.11", {"start": v(24.04, -2.65) * mm, "end": v(29.12, -2.65) * mm});
            skLineSegment(sketch, "E3.3.12.11", {"start": v(24.04, -7.73) * mm, "end": v(29.12, -7.73) * mm});
            skLineSegment(sketch, "E3.6.12.11", {"start": v(24.04, -2.65) * mm, "end": v(24.04, -7.73) * mm});
            skLineSegment(sketch, "E3.9.12.11", {"start": v(29.12, -2.65) * mm, "end": v(29.12, -7.73) * mm});
            skLineSegment(sketch, "E3.0.12.12", {"start": v(24.04, -10.27) * mm, "end": v(29.12, -10.27) * mm});
            skLineSegment(sketch, "E3.3.12.12", {"start": v(24.04, -15.35) * mm, "end": v(29.12, -15.35) * mm});
            skLineSegment(sketch, "E3.6.12.12", {"start": v(24.04, -10.27) * mm, "end": v(24.04, -15.35) * mm});
            skLineSegment(sketch, "E3.9.12.12", {"start": v(29.12, -10.27) * mm, "end": v(29.12, -15.35) * mm});
            skLineSegment(sketch, "E3.0.12.13", {"start": v(24.04, -17.9) * mm, "end": v(29.12, -17.9) * mm});
            skLineSegment(sketch, "E3.3.12.13", {"start": v(24.04, -22.97) * mm, "end": v(29.12, -22.97) * mm});
            skLineSegment(sketch, "E3.6.12.13", {"start": v(24.04, -17.9) * mm, "end": v(24.04, -22.97) * mm});
            skLineSegment(sketch, "E3.9.12.13", {"start": v(29.12, -17.9) * mm, "end": v(29.12, -22.97) * mm});
            skLineSegment(sketch, "E3.0.12.14", {"start": v(24.04, -25.51) * mm, "end": v(29.12, -25.51) * mm});
            skLineSegment(sketch, "E3.3.12.14", {"start": v(24.04, -30.6) * mm, "end": v(29.12, -30.6) * mm});
            skLineSegment(sketch, "E3.6.12.14", {"start": v(24.04, -25.51) * mm, "end": v(24.04, -30.6) * mm});
            skLineSegment(sketch, "E3.9.12.14", {"start": v(29.12, -25.51) * mm, "end": v(29.12, -30.6) * mm});
            skLineSegment(sketch, "E3.0.12.15", {"start": v(24.04, -33.13) * mm, "end": v(29.12, -33.13) * mm});
            skLineSegment(sketch, "E3.3.12.15", {"start": v(24.04, -38.21) * mm, "end": v(29.12, -38.21) * mm});
            skLineSegment(sketch, "E3.6.12.15", {"start": v(24.04, -33.13) * mm, "end": v(24.04, -38.21) * mm});
            skLineSegment(sketch, "E3.9.12.15", {"start": v(29.12, -33.13) * mm, "end": v(29.12, -38.21) * mm});
            skLineSegment(sketch, "E3.0.12.16", {"start": v(24.04, -40.75) * mm, "end": v(29.12, -40.75) * mm});
            skLineSegment(sketch, "E3.3.12.16", {"start": v(24.04, -45.83) * mm, "end": v(29.12, -45.83) * mm});
            skLineSegment(sketch, "E3.6.12.16", {"start": v(24.04, -40.75) * mm, "end": v(24.04, -45.83) * mm});
            skLineSegment(sketch, "E3.9.12.16", {"start": v(29.12, -40.75) * mm, "end": v(29.12, -45.83) * mm});
            skLineSegment(sketch, "E3.0.12.17", {"start": v(24.04, -48.37) * mm, "end": v(29.12, -48.37) * mm});
            skLineSegment(sketch, "E3.3.12.17", {"start": v(24.04, -53.45) * mm, "end": v(29.12, -53.45) * mm});
            skLineSegment(sketch, "E3.6.12.17", {"start": v(24.04, -48.37) * mm, "end": v(24.04, -53.45) * mm});
            skLineSegment(sketch, "E3.9.12.17", {"start": v(29.12, -48.37) * mm, "end": v(29.12, -53.45) * mm});
            skLineSegment(sketch, "E3.0.12.18", {"start": v(24.04, -56) * mm, "end": v(29.12, -56) * mm});
            skLineSegment(sketch, "E3.3.12.18", {"start": v(24.04, -61.07) * mm, "end": v(29.12, -61.07) * mm});
            skLineSegment(sketch, "E3.6.12.18", {"start": v(24.04, -56) * mm, "end": v(24.04, -61.07) * mm});
            skLineSegment(sketch, "E3.9.12.18", {"start": v(29.12, -56) * mm, "end": v(29.12, -61.07) * mm});
            skLineSegment(sketch, "E3.0.12.19", {"start": v(24.04, -63.61) * mm, "end": v(29.12, -63.61) * mm});
            skLineSegment(sketch, "E3.3.12.19", {"start": v(24.04, -68.7) * mm, "end": v(29.12, -68.7) * mm});
            skLineSegment(sketch, "E3.6.12.19", {"start": v(24.04, -63.61) * mm, "end": v(24.04, -68.7) * mm});
            skLineSegment(sketch, "E3.9.12.19", {"start": v(29.12, -63.61) * mm, "end": v(29.12, -68.7) * mm});
            skLineSegment(sketch, "E3.0.12.20", {"start": v(24.04, -71.23) * mm, "end": v(29.12, -71.23) * mm});
            skLineSegment(sketch, "E3.3.12.20", {"start": v(24.04, -76.31) * mm, "end": v(29.12, -76.31) * mm});
            skLineSegment(sketch, "E3.6.12.20", {"start": v(24.04, -71.23) * mm, "end": v(24.04, -76.31) * mm});
            skLineSegment(sketch, "E3.9.12.20", {"start": v(29.12, -71.23) * mm, "end": v(29.12, -76.31) * mm});
            skLineSegment(sketch, "E3.0.12.21", {"start": v(24.04, -78.85) * mm, "end": v(29.12, -78.85) * mm});
            skLineSegment(sketch, "E3.3.12.21", {"start": v(24.04, -83.93) * mm, "end": v(29.12, -83.93) * mm});
            skLineSegment(sketch, "E3.6.12.21", {"start": v(24.04, -78.85) * mm, "end": v(24.04, -83.93) * mm});
            skLineSegment(sketch, "E3.9.12.21", {"start": v(29.12, -78.85) * mm, "end": v(29.12, -83.93) * mm});
            skLineSegment(sketch, "E3.0.13.0", {"start": v(31.66, 81.17) * mm, "end": v(36.74, 81.17) * mm});
            skLineSegment(sketch, "E3.3.13.0", {"start": v(31.66, 76.09) * mm, "end": v(36.74, 76.09) * mm});
            skLineSegment(sketch, "E3.6.13.0", {"start": v(31.66, 81.17) * mm, "end": v(31.66, 76.09) * mm});
            skLineSegment(sketch, "E3.9.13.0", {"start": v(36.74, 81.17) * mm, "end": v(36.74, 76.09) * mm});
            skLineSegment(sketch, "E3.0.13.1", {"start": v(31.66, 73.55) * mm, "end": v(36.74, 73.55) * mm});
            skLineSegment(sketch, "E3.3.13.1", {"start": v(31.66, 68.47) * mm, "end": v(36.74, 68.47) * mm});
            skLineSegment(sketch, "E3.6.13.1", {"start": v(31.66, 73.55) * mm, "end": v(31.66, 68.47) * mm});
            skLineSegment(sketch, "E3.9.13.1", {"start": v(36.74, 73.55) * mm, "end": v(36.74, 68.47) * mm});
            skLineSegment(sketch, "E3.0.13.2", {"start": v(31.66, 65.93) * mm, "end": v(36.74, 65.93) * mm});
            skLineSegment(sketch, "E3.3.13.2", {"start": v(31.66, 60.85) * mm, "end": v(36.74, 60.85) * mm});
            skLineSegment(sketch, "E3.6.13.2", {"start": v(31.66, 65.93) * mm, "end": v(31.66, 60.85) * mm});
            skLineSegment(sketch, "E3.9.13.2", {"start": v(36.74, 65.93) * mm, "end": v(36.74, 60.85) * mm});
            skLineSegment(sketch, "E3.0.13.3", {"start": v(31.66, 58.3) * mm, "end": v(36.74, 58.3) * mm});
            skLineSegment(sketch, "E3.3.13.3", {"start": v(31.66, 53.23) * mm, "end": v(36.74, 53.23) * mm});
            skLineSegment(sketch, "E3.6.13.3", {"start": v(31.66, 58.3) * mm, "end": v(31.66, 53.23) * mm});
            skLineSegment(sketch, "E3.9.13.3", {"start": v(36.74, 58.3) * mm, "end": v(36.74, 53.23) * mm});
            skLineSegment(sketch, "E3.0.13.4", {"start": v(31.66, 50.69) * mm, "end": v(36.74, 50.69) * mm});
            skLineSegment(sketch, "E3.3.13.4", {"start": v(31.66, 45.6) * mm, "end": v(36.74, 45.6) * mm});
            skLineSegment(sketch, "E3.6.13.4", {"start": v(31.66, 50.69) * mm, "end": v(31.66, 45.6) * mm});
            skLineSegment(sketch, "E3.9.13.4", {"start": v(36.74, 50.69) * mm, "end": v(36.74, 45.6) * mm});
            skLineSegment(sketch, "E3.0.13.5", {"start": v(31.66, 43.07) * mm, "end": v(36.74, 43.07) * mm});
            skLineSegment(sketch, "E3.3.13.5", {"start": v(31.66, 37.99) * mm, "end": v(36.74, 37.99) * mm});
            skLineSegment(sketch, "E3.6.13.5", {"start": v(31.66, 43.07) * mm, "end": v(31.66, 37.99) * mm});
            skLineSegment(sketch, "E3.9.13.5", {"start": v(36.74, 43.07) * mm, "end": v(36.74, 37.99) * mm});
            skLineSegment(sketch, "E3.0.13.6", {"start": v(31.66, 35.45) * mm, "end": v(36.74, 35.45) * mm});
            skLineSegment(sketch, "E3.3.13.6", {"start": v(31.66, 30.37) * mm, "end": v(36.74, 30.37) * mm});
            skLineSegment(sketch, "E3.6.13.6", {"start": v(31.66, 35.45) * mm, "end": v(31.66, 30.37) * mm});
            skLineSegment(sketch, "E3.9.13.6", {"start": v(36.74, 35.45) * mm, "end": v(36.74, 30.37) * mm});
            skLineSegment(sketch, "E3.0.13.7", {"start": v(31.66, 27.83) * mm, "end": v(36.74, 27.83) * mm});
            skLineSegment(sketch, "E3.3.13.7", {"start": v(31.66, 22.75) * mm, "end": v(36.74, 22.75) * mm});
            skLineSegment(sketch, "E3.6.13.7", {"start": v(31.66, 27.83) * mm, "end": v(31.66, 22.75) * mm});
            skLineSegment(sketch, "E3.9.13.7", {"start": v(36.74, 27.83) * mm, "end": v(36.74, 22.75) * mm});
            skLineSegment(sketch, "E3.0.13.8", {"start": v(31.66, 20.2) * mm, "end": v(36.74, 20.2) * mm});
            skLineSegment(sketch, "E3.3.13.8", {"start": v(31.66, 15.13) * mm, "end": v(36.74, 15.13) * mm});
            skLineSegment(sketch, "E3.6.13.8", {"start": v(31.66, 20.2) * mm, "end": v(31.66, 15.13) * mm});
            skLineSegment(sketch, "E3.9.13.8", {"start": v(36.74, 20.2) * mm, "end": v(36.74, 15.13) * mm});
            skLineSegment(sketch, "E3.0.13.9", {"start": v(31.66, 12.59) * mm, "end": v(36.74, 12.59) * mm});
            skLineSegment(sketch, "E3.3.13.9", {"start": v(31.66, 7.5) * mm, "end": v(36.74, 7.5) * mm});
            skLineSegment(sketch, "E3.6.13.9", {"start": v(31.66, 12.59) * mm, "end": v(31.66, 7.5) * mm});
            skLineSegment(sketch, "E3.9.13.9", {"start": v(36.74, 12.59) * mm, "end": v(36.74, 7.5) * mm});
            skLineSegment(sketch, "E3.0.13.10", {"start": v(31.66, 4.97) * mm, "end": v(36.74, 4.97) * mm});
            skLineSegment(sketch, "E3.3.13.10", {"start": v(31.66, -0.11) * mm, "end": v(36.74, -0.11) * mm});
            skLineSegment(sketch, "E3.6.13.10", {"start": v(31.66, 4.97) * mm, "end": v(31.66, -0.11) * mm});
            skLineSegment(sketch, "E3.9.13.10", {"start": v(36.74, 4.97) * mm, "end": v(36.74, -0.11) * mm});
            skLineSegment(sketch, "E3.0.13.11", {"start": v(31.66, -2.65) * mm, "end": v(36.74, -2.65) * mm});
            skLineSegment(sketch, "E3.3.13.11", {"start": v(31.66, -7.73) * mm, "end": v(36.74, -7.73) * mm});
            skLineSegment(sketch, "E3.6.13.11", {"start": v(31.66, -2.65) * mm, "end": v(31.66, -7.73) * mm});
            skLineSegment(sketch, "E3.9.13.11", {"start": v(36.74, -2.65) * mm, "end": v(36.74, -7.73) * mm});
            skLineSegment(sketch, "E3.0.13.12", {"start": v(31.66, -10.27) * mm, "end": v(36.74, -10.27) * mm});
            skLineSegment(sketch, "E3.3.13.12", {"start": v(31.66, -15.35) * mm, "end": v(36.74, -15.35) * mm});
            skLineSegment(sketch, "E3.6.13.12", {"start": v(31.66, -10.27) * mm, "end": v(31.66, -15.35) * mm});
            skLineSegment(sketch, "E3.9.13.12", {"start": v(36.74, -10.27) * mm, "end": v(36.74, -15.35) * mm});
            skLineSegment(sketch, "E3.0.13.13", {"start": v(31.66, -17.9) * mm, "end": v(36.74, -17.9) * mm});
            skLineSegment(sketch, "E3.3.13.13", {"start": v(31.66, -22.97) * mm, "end": v(36.74, -22.97) * mm});
            skLineSegment(sketch, "E3.6.13.13", {"start": v(31.66, -17.9) * mm, "end": v(31.66, -22.97) * mm});
            skLineSegment(sketch, "E3.9.13.13", {"start": v(36.74, -17.9) * mm, "end": v(36.74, -22.97) * mm});
            skLineSegment(sketch, "E3.0.13.14", {"start": v(31.66, -25.51) * mm, "end": v(36.74, -25.51) * mm});
            skLineSegment(sketch, "E3.3.13.14", {"start": v(31.66, -30.6) * mm, "end": v(36.74, -30.6) * mm});
            skLineSegment(sketch, "E3.6.13.14", {"start": v(31.66, -25.51) * mm, "end": v(31.66, -30.6) * mm});
            skLineSegment(sketch, "E3.9.13.14", {"start": v(36.74, -25.51) * mm, "end": v(36.74, -30.6) * mm});
            skLineSegment(sketch, "E3.0.13.15", {"start": v(31.66, -33.13) * mm, "end": v(36.74, -33.13) * mm});
            skLineSegment(sketch, "E3.3.13.15", {"start": v(31.66, -38.21) * mm, "end": v(36.74, -38.21) * mm});
            skLineSegment(sketch, "E3.6.13.15", {"start": v(31.66, -33.13) * mm, "end": v(31.66, -38.21) * mm});
            skLineSegment(sketch, "E3.9.13.15", {"start": v(36.74, -33.13) * mm, "end": v(36.74, -38.21) * mm});
            skLineSegment(sketch, "E3.0.13.16", {"start": v(31.66, -40.75) * mm, "end": v(36.74, -40.75) * mm});
            skLineSegment(sketch, "E3.3.13.16", {"start": v(31.66, -45.83) * mm, "end": v(36.74, -45.83) * mm});
            skLineSegment(sketch, "E3.6.13.16", {"start": v(31.66, -40.75) * mm, "end": v(31.66, -45.83) * mm});
            skLineSegment(sketch, "E3.9.13.16", {"start": v(36.74, -40.75) * mm, "end": v(36.74, -45.83) * mm});
            skLineSegment(sketch, "E3.0.13.17", {"start": v(31.66, -48.37) * mm, "end": v(36.74, -48.37) * mm});
            skLineSegment(sketch, "E3.3.13.17", {"start": v(31.66, -53.45) * mm, "end": v(36.74, -53.45) * mm});
            skLineSegment(sketch, "E3.6.13.17", {"start": v(31.66, -48.37) * mm, "end": v(31.66, -53.45) * mm});
            skLineSegment(sketch, "E3.9.13.17", {"start": v(36.74, -48.37) * mm, "end": v(36.74, -53.45) * mm});
            skLineSegment(sketch, "E3.0.13.18", {"start": v(31.66, -56) * mm, "end": v(36.74, -56) * mm});
            skLineSegment(sketch, "E3.3.13.18", {"start": v(31.66, -61.07) * mm, "end": v(36.74, -61.07) * mm});
            skLineSegment(sketch, "E3.6.13.18", {"start": v(31.66, -56) * mm, "end": v(31.66, -61.07) * mm});
            skLineSegment(sketch, "E3.9.13.18", {"start": v(36.74, -56) * mm, "end": v(36.74, -61.07) * mm});
            skLineSegment(sketch, "E3.0.13.19", {"start": v(31.66, -63.61) * mm, "end": v(36.74, -63.61) * mm});
            skLineSegment(sketch, "E3.3.13.19", {"start": v(31.66, -68.7) * mm, "end": v(36.74, -68.7) * mm});
            skLineSegment(sketch, "E3.6.13.19", {"start": v(31.66, -63.61) * mm, "end": v(31.66, -68.7) * mm});
            skLineSegment(sketch, "E3.9.13.19", {"start": v(36.74, -63.61) * mm, "end": v(36.74, -68.7) * mm});
            skLineSegment(sketch, "E3.0.13.20", {"start": v(31.66, -71.23) * mm, "end": v(36.74, -71.23) * mm});
            skLineSegment(sketch, "E3.3.13.20", {"start": v(31.66, -76.31) * mm, "end": v(36.74, -76.31) * mm});
            skLineSegment(sketch, "E3.6.13.20", {"start": v(31.66, -71.23) * mm, "end": v(31.66, -76.31) * mm});
            skLineSegment(sketch, "E3.9.13.20", {"start": v(36.74, -71.23) * mm, "end": v(36.74, -76.31) * mm});
            skLineSegment(sketch, "E3.0.13.21", {"start": v(31.66, -78.85) * mm, "end": v(36.74, -78.85) * mm});
            skLineSegment(sketch, "E3.3.13.21", {"start": v(31.66, -83.93) * mm, "end": v(36.74, -83.93) * mm});
            skLineSegment(sketch, "E3.6.13.21", {"start": v(31.66, -78.85) * mm, "end": v(31.66, -83.93) * mm});
            skLineSegment(sketch, "E3.9.13.21", {"start": v(36.74, -78.85) * mm, "end": v(36.74, -83.93) * mm});
            skLineSegment(sketch, "E3.0.14.0", {"start": v(39.28, 81.17) * mm, "end": v(44.36, 81.17) * mm});
            skLineSegment(sketch, "E3.3.14.0", {"start": v(39.28, 76.09) * mm, "end": v(44.36, 76.09) * mm});
            skLineSegment(sketch, "E3.6.14.0", {"start": v(39.28, 81.17) * mm, "end": v(39.28, 76.09) * mm});
            skLineSegment(sketch, "E3.9.14.0", {"start": v(44.36, 81.17) * mm, "end": v(44.36, 76.09) * mm});
            skLineSegment(sketch, "E3.0.14.1", {"start": v(39.28, 73.55) * mm, "end": v(44.36, 73.55) * mm});
            skLineSegment(sketch, "E3.3.14.1", {"start": v(39.28, 68.47) * mm, "end": v(44.36, 68.47) * mm});
            skLineSegment(sketch, "E3.6.14.1", {"start": v(39.28, 73.55) * mm, "end": v(39.28, 68.47) * mm});
            skLineSegment(sketch, "E3.9.14.1", {"start": v(44.36, 73.55) * mm, "end": v(44.36, 68.47) * mm});
            skLineSegment(sketch, "E3.0.14.2", {"start": v(39.28, 65.93) * mm, "end": v(44.36, 65.93) * mm});
            skLineSegment(sketch, "E3.3.14.2", {"start": v(39.28, 60.85) * mm, "end": v(44.36, 60.85) * mm});
            skLineSegment(sketch, "E3.6.14.2", {"start": v(39.28, 65.93) * mm, "end": v(39.28, 60.85) * mm});
            skLineSegment(sketch, "E3.9.14.2", {"start": v(44.36, 65.93) * mm, "end": v(44.36, 60.85) * mm});
            skLineSegment(sketch, "E3.0.14.3", {"start": v(39.28, 58.3) * mm, "end": v(44.36, 58.3) * mm});
            skLineSegment(sketch, "E3.3.14.3", {"start": v(39.28, 53.23) * mm, "end": v(44.36, 53.23) * mm});
            skLineSegment(sketch, "E3.6.14.3", {"start": v(39.28, 58.3) * mm, "end": v(39.28, 53.23) * mm});
            skLineSegment(sketch, "E3.9.14.3", {"start": v(44.36, 58.3) * mm, "end": v(44.36, 53.23) * mm});
            skLineSegment(sketch, "E3.0.14.4", {"start": v(39.28, 50.69) * mm, "end": v(44.36, 50.69) * mm});
            skLineSegment(sketch, "E3.3.14.4", {"start": v(39.28, 45.6) * mm, "end": v(44.36, 45.6) * mm});
            skLineSegment(sketch, "E3.6.14.4", {"start": v(39.28, 50.69) * mm, "end": v(39.28, 45.6) * mm});
            skLineSegment(sketch, "E3.9.14.4", {"start": v(44.36, 50.69) * mm, "end": v(44.36, 45.6) * mm});
            skLineSegment(sketch, "E3.0.14.5", {"start": v(39.28, 43.07) * mm, "end": v(44.36, 43.07) * mm});
            skLineSegment(sketch, "E3.3.14.5", {"start": v(39.28, 37.99) * mm, "end": v(44.36, 37.99) * mm});
            skLineSegment(sketch, "E3.6.14.5", {"start": v(39.28, 43.07) * mm, "end": v(39.28, 37.99) * mm});
            skLineSegment(sketch, "E3.9.14.5", {"start": v(44.36, 43.07) * mm, "end": v(44.36, 37.99) * mm});
            skLineSegment(sketch, "E3.0.14.6", {"start": v(39.28, 35.45) * mm, "end": v(44.36, 35.45) * mm});
            skLineSegment(sketch, "E3.3.14.6", {"start": v(39.28, 30.37) * mm, "end": v(44.36, 30.37) * mm});
            skLineSegment(sketch, "E3.6.14.6", {"start": v(39.28, 35.45) * mm, "end": v(39.28, 30.37) * mm});
            skLineSegment(sketch, "E3.9.14.6", {"start": v(44.36, 35.45) * mm, "end": v(44.36, 30.37) * mm});
            skLineSegment(sketch, "E3.0.14.7", {"start": v(39.28, 27.83) * mm, "end": v(44.36, 27.83) * mm});
            skLineSegment(sketch, "E3.3.14.7", {"start": v(39.28, 22.75) * mm, "end": v(44.36, 22.75) * mm});
            skLineSegment(sketch, "E3.6.14.7", {"start": v(39.28, 27.83) * mm, "end": v(39.28, 22.75) * mm});
            skLineSegment(sketch, "E3.9.14.7", {"start": v(44.36, 27.83) * mm, "end": v(44.36, 22.75) * mm});
            skLineSegment(sketch, "E3.0.14.8", {"start": v(39.28, 20.2) * mm, "end": v(44.36, 20.2) * mm});
            skLineSegment(sketch, "E3.3.14.8", {"start": v(39.28, 15.13) * mm, "end": v(44.36, 15.13) * mm});
            skLineSegment(sketch, "E3.6.14.8", {"start": v(39.28, 20.2) * mm, "end": v(39.28, 15.13) * mm});
            skLineSegment(sketch, "E3.9.14.8", {"start": v(44.36, 20.2) * mm, "end": v(44.36, 15.13) * mm});
            skLineSegment(sketch, "E3.0.14.9", {"start": v(39.28, 12.59) * mm, "end": v(44.36, 12.59) * mm});
            skLineSegment(sketch, "E3.3.14.9", {"start": v(39.28, 7.5) * mm, "end": v(44.36, 7.5) * mm});
            skLineSegment(sketch, "E3.6.14.9", {"start": v(39.28, 12.59) * mm, "end": v(39.28, 7.5) * mm});
            skLineSegment(sketch, "E3.9.14.9", {"start": v(44.36, 12.59) * mm, "end": v(44.36, 7.5) * mm});
            skLineSegment(sketch, "E3.0.14.10", {"start": v(39.28, 4.97) * mm, "end": v(44.36, 4.97) * mm});
            skLineSegment(sketch, "E3.3.14.10", {"start": v(39.28, -0.11) * mm, "end": v(44.36, -0.11) * mm});
            skLineSegment(sketch, "E3.6.14.10", {"start": v(39.28, 4.97) * mm, "end": v(39.28, -0.11) * mm});
            skLineSegment(sketch, "E3.9.14.10", {"start": v(44.36, 4.97) * mm, "end": v(44.36, -0.11) * mm});
            skLineSegment(sketch, "E3.0.14.11", {"start": v(39.28, -2.65) * mm, "end": v(44.36, -2.65) * mm});
            skLineSegment(sketch, "E3.3.14.11", {"start": v(39.28, -7.73) * mm, "end": v(44.36, -7.73) * mm});
            skLineSegment(sketch, "E3.6.14.11", {"start": v(39.28, -2.65) * mm, "end": v(39.28, -7.73) * mm});
            skLineSegment(sketch, "E3.9.14.11", {"start": v(44.36, -2.65) * mm, "end": v(44.36, -7.73) * mm});
            skLineSegment(sketch, "E3.0.14.12", {"start": v(39.28, -10.27) * mm, "end": v(44.36, -10.27) * mm});
            skLineSegment(sketch, "E3.3.14.12", {"start": v(39.28, -15.35) * mm, "end": v(44.36, -15.35) * mm});
            skLineSegment(sketch, "E3.6.14.12", {"start": v(39.28, -10.27) * mm, "end": v(39.28, -15.35) * mm});
            skLineSegment(sketch, "E3.9.14.12", {"start": v(44.36, -10.27) * mm, "end": v(44.36, -15.35) * mm});
            skLineSegment(sketch, "E3.0.14.13", {"start": v(39.28, -17.9) * mm, "end": v(44.36, -17.9) * mm});
            skLineSegment(sketch, "E3.3.14.13", {"start": v(39.28, -22.97) * mm, "end": v(44.36, -22.97) * mm});
            skLineSegment(sketch, "E3.6.14.13", {"start": v(39.28, -17.9) * mm, "end": v(39.28, -22.97) * mm});
            skLineSegment(sketch, "E3.9.14.13", {"start": v(44.36, -17.9) * mm, "end": v(44.36, -22.97) * mm});
            skLineSegment(sketch, "E3.0.14.14", {"start": v(39.28, -25.51) * mm, "end": v(44.36, -25.51) * mm});
            skLineSegment(sketch, "E3.3.14.14", {"start": v(39.28, -30.6) * mm, "end": v(44.36, -30.6) * mm});
            skLineSegment(sketch, "E3.6.14.14", {"start": v(39.28, -25.51) * mm, "end": v(39.28, -30.6) * mm});
            skLineSegment(sketch, "E3.9.14.14", {"start": v(44.36, -25.51) * mm, "end": v(44.36, -30.6) * mm});
            skLineSegment(sketch, "E3.0.14.15", {"start": v(39.28, -33.13) * mm, "end": v(44.36, -33.13) * mm});
            skLineSegment(sketch, "E3.3.14.15", {"start": v(39.28, -38.21) * mm, "end": v(44.36, -38.21) * mm});
            skLineSegment(sketch, "E3.6.14.15", {"start": v(39.28, -33.13) * mm, "end": v(39.28, -38.21) * mm});
            skLineSegment(sketch, "E3.9.14.15", {"start": v(44.36, -33.13) * mm, "end": v(44.36, -38.21) * mm});
            skLineSegment(sketch, "E3.0.14.16", {"start": v(39.28, -40.75) * mm, "end": v(44.36, -40.75) * mm});
            skLineSegment(sketch, "E3.3.14.16", {"start": v(39.28, -45.83) * mm, "end": v(44.36, -45.83) * mm});
            skLineSegment(sketch, "E3.6.14.16", {"start": v(39.28, -40.75) * mm, "end": v(39.28, -45.83) * mm});
            skLineSegment(sketch, "E3.9.14.16", {"start": v(44.36, -40.75) * mm, "end": v(44.36, -45.83) * mm});
            skLineSegment(sketch, "E3.0.14.17", {"start": v(39.28, -48.37) * mm, "end": v(44.36, -48.37) * mm});
            skLineSegment(sketch, "E3.3.14.17", {"start": v(39.28, -53.45) * mm, "end": v(44.36, -53.45) * mm});
            skLineSegment(sketch, "E3.6.14.17", {"start": v(39.28, -48.37) * mm, "end": v(39.28, -53.45) * mm});
            skLineSegment(sketch, "E3.9.14.17", {"start": v(44.36, -48.37) * mm, "end": v(44.36, -53.45) * mm});
            skLineSegment(sketch, "E3.0.14.18", {"start": v(39.28, -56) * mm, "end": v(44.36, -56) * mm});
            skLineSegment(sketch, "E3.3.14.18", {"start": v(39.28, -61.07) * mm, "end": v(44.36, -61.07) * mm});
            skLineSegment(sketch, "E3.6.14.18", {"start": v(39.28, -56) * mm, "end": v(39.28, -61.07) * mm});
            skLineSegment(sketch, "E3.9.14.18", {"start": v(44.36, -56) * mm, "end": v(44.36, -61.07) * mm});
            skLineSegment(sketch, "E3.0.14.19", {"start": v(39.28, -63.61) * mm, "end": v(44.36, -63.61) * mm});
            skLineSegment(sketch, "E3.3.14.19", {"start": v(39.28, -68.7) * mm, "end": v(44.36, -68.7) * mm});
            skLineSegment(sketch, "E3.6.14.19", {"start": v(39.28, -63.61) * mm, "end": v(39.28, -68.7) * mm});
            skLineSegment(sketch, "E3.9.14.19", {"start": v(44.36, -63.61) * mm, "end": v(44.36, -68.7) * mm});
            skLineSegment(sketch, "E3.0.14.20", {"start": v(39.28, -71.23) * mm, "end": v(44.36, -71.23) * mm});
            skLineSegment(sketch, "E3.3.14.20", {"start": v(39.28, -76.31) * mm, "end": v(44.36, -76.31) * mm});
            skLineSegment(sketch, "E3.6.14.20", {"start": v(39.28, -71.23) * mm, "end": v(39.28, -76.31) * mm});
            skLineSegment(sketch, "E3.9.14.20", {"start": v(44.36, -71.23) * mm, "end": v(44.36, -76.31) * mm});
            skLineSegment(sketch, "E3.0.14.21", {"start": v(39.28, -78.85) * mm, "end": v(44.36, -78.85) * mm});
            skLineSegment(sketch, "E3.3.14.21", {"start": v(39.28, -83.93) * mm, "end": v(44.36, -83.93) * mm});
            skLineSegment(sketch, "E3.6.14.21", {"start": v(39.28, -78.85) * mm, "end": v(39.28, -83.93) * mm});
            skLineSegment(sketch, "E3.9.14.21", {"start": v(44.36, -78.85) * mm, "end": v(44.36, -83.93) * mm});
            skLineSegment(sketch, "E4.0.15.0", {"start": v(46.9, 81.17) * mm, "end": v(51.98, 81.17) * mm});
            skLineSegment(sketch, "E4.3.15.0", {"start": v(46.9, 76.09) * mm, "end": v(51.98, 76.09) * mm});
            skLineSegment(sketch, "E4.6.15.0", {"start": v(46.9, 81.17) * mm, "end": v(46.9, 76.09) * mm});
            skLineSegment(sketch, "E4.9.15.0", {"start": v(51.98, 81.17) * mm, "end": v(51.98, 76.09) * mm});
            skLineSegment(sketch, "E4.0.15.1", {"start": v(46.9, 73.55) * mm, "end": v(51.98, 73.55) * mm});
            skLineSegment(sketch, "E4.3.15.1", {"start": v(46.9, 68.47) * mm, "end": v(51.98, 68.47) * mm});
            skLineSegment(sketch, "E4.6.15.1", {"start": v(46.9, 73.55) * mm, "end": v(46.9, 68.47) * mm});
            skLineSegment(sketch, "E4.9.15.1", {"start": v(51.98, 73.55) * mm, "end": v(51.98, 68.47) * mm});
            skLineSegment(sketch, "E4.0.15.2", {"start": v(46.9, 65.93) * mm, "end": v(51.98, 65.93) * mm});
            skLineSegment(sketch, "E4.3.15.2", {"start": v(46.9, 60.85) * mm, "end": v(51.98, 60.85) * mm});
            skLineSegment(sketch, "E4.6.15.2", {"start": v(46.9, 65.93) * mm, "end": v(46.9, 60.85) * mm});
            skLineSegment(sketch, "E4.9.15.2", {"start": v(51.98, 65.93) * mm, "end": v(51.98, 60.85) * mm});
            skLineSegment(sketch, "E4.0.15.3", {"start": v(46.9, 58.3) * mm, "end": v(51.98, 58.3) * mm});
            skLineSegment(sketch, "E4.3.15.3", {"start": v(46.9, 53.23) * mm, "end": v(51.98, 53.23) * mm});
            skLineSegment(sketch, "E4.6.15.3", {"start": v(46.9, 58.3) * mm, "end": v(46.9, 53.23) * mm});
            skLineSegment(sketch, "E4.9.15.3", {"start": v(51.98, 58.3) * mm, "end": v(51.98, 53.23) * mm});
            skLineSegment(sketch, "E4.0.15.4", {"start": v(46.9, 50.69) * mm, "end": v(51.98, 50.69) * mm});
            skLineSegment(sketch, "E4.3.15.4", {"start": v(46.9, 45.6) * mm, "end": v(51.98, 45.6) * mm});
            skLineSegment(sketch, "E4.6.15.4", {"start": v(46.9, 50.69) * mm, "end": v(46.9, 45.6) * mm});
            skLineSegment(sketch, "E4.9.15.4", {"start": v(51.98, 50.69) * mm, "end": v(51.98, 45.6) * mm});
            skLineSegment(sketch, "E4.0.15.5", {"start": v(46.9, 43.07) * mm, "end": v(51.98, 43.07) * mm});
            skLineSegment(sketch, "E4.3.15.5", {"start": v(46.9, 37.99) * mm, "end": v(51.98, 37.99) * mm});
            skLineSegment(sketch, "E4.6.15.5", {"start": v(46.9, 43.07) * mm, "end": v(46.9, 37.99) * mm});
            skLineSegment(sketch, "E4.9.15.5", {"start": v(51.98, 43.07) * mm, "end": v(51.98, 37.99) * mm});
            skLineSegment(sketch, "E4.0.15.6", {"start": v(46.9, 35.45) * mm, "end": v(51.98, 35.45) * mm});
            skLineSegment(sketch, "E4.3.15.6", {"start": v(46.9, 30.37) * mm, "end": v(51.98, 30.37) * mm});
            skLineSegment(sketch, "E4.6.15.6", {"start": v(46.9, 35.45) * mm, "end": v(46.9, 30.37) * mm});
            skLineSegment(sketch, "E4.9.15.6", {"start": v(51.98, 35.45) * mm, "end": v(51.98, 30.37) * mm});
            skLineSegment(sketch, "E4.0.15.7", {"start": v(46.9, 27.83) * mm, "end": v(51.98, 27.83) * mm});
            skLineSegment(sketch, "E4.3.15.7", {"start": v(46.9, 22.75) * mm, "end": v(51.98, 22.75) * mm});
            skLineSegment(sketch, "E4.6.15.7", {"start": v(46.9, 27.83) * mm, "end": v(46.9, 22.75) * mm});
            skLineSegment(sketch, "E4.9.15.7", {"start": v(51.98, 27.83) * mm, "end": v(51.98, 22.75) * mm});
            skLineSegment(sketch, "E4.0.15.8", {"start": v(46.9, 20.2) * mm, "end": v(51.98, 20.2) * mm});
            skLineSegment(sketch, "E4.3.15.8", {"start": v(46.9, 15.13) * mm, "end": v(51.98, 15.13) * mm});
            skLineSegment(sketch, "E4.6.15.8", {"start": v(46.9, 20.2) * mm, "end": v(46.9, 15.13) * mm});
            skLineSegment(sketch, "E4.9.15.8", {"start": v(51.98, 20.2) * mm, "end": v(51.98, 15.13) * mm});
            skLineSegment(sketch, "E4.0.15.9", {"start": v(46.9, 12.59) * mm, "end": v(51.98, 12.59) * mm});
            skLineSegment(sketch, "E4.3.15.9", {"start": v(46.9, 7.5) * mm, "end": v(51.98, 7.5) * mm});
            skLineSegment(sketch, "E4.6.15.9", {"start": v(46.9, 12.59) * mm, "end": v(46.9, 7.5) * mm});
            skLineSegment(sketch, "E4.9.15.9", {"start": v(51.98, 12.59) * mm, "end": v(51.98, 7.5) * mm});
            skLineSegment(sketch, "E4.0.15.10", {"start": v(46.9, 4.97) * mm, "end": v(51.98, 4.97) * mm});
            skLineSegment(sketch, "E4.3.15.10", {"start": v(46.9, -0.11) * mm, "end": v(51.98, -0.11) * mm});
            skLineSegment(sketch, "E4.6.15.10", {"start": v(46.9, 4.97) * mm, "end": v(46.9, -0.11) * mm});
            skLineSegment(sketch, "E4.9.15.10", {"start": v(51.98, 4.97) * mm, "end": v(51.98, -0.11) * mm});
            skLineSegment(sketch, "E4.0.15.11", {"start": v(46.9, -2.65) * mm, "end": v(51.98, -2.65) * mm});
            skLineSegment(sketch, "E4.3.15.11", {"start": v(46.9, -7.73) * mm, "end": v(51.98, -7.73) * mm});
            skLineSegment(sketch, "E4.6.15.11", {"start": v(46.9, -2.65) * mm, "end": v(46.9, -7.73) * mm});
            skLineSegment(sketch, "E4.9.15.11", {"start": v(51.98, -2.65) * mm, "end": v(51.98, -7.73) * mm});
            skLineSegment(sketch, "E4.0.15.12", {"start": v(46.9, -10.27) * mm, "end": v(51.98, -10.27) * mm});
            skLineSegment(sketch, "E4.3.15.12", {"start": v(46.9, -15.35) * mm, "end": v(51.98, -15.35) * mm});
            skLineSegment(sketch, "E4.6.15.12", {"start": v(46.9, -10.27) * mm, "end": v(46.9, -15.35) * mm});
            skLineSegment(sketch, "E4.9.15.12", {"start": v(51.98, -10.27) * mm, "end": v(51.98, -15.35) * mm});
            skLineSegment(sketch, "E4.0.15.13", {"start": v(46.9, -17.9) * mm, "end": v(51.98, -17.9) * mm});
            skLineSegment(sketch, "E4.3.15.13", {"start": v(46.9, -22.97) * mm, "end": v(51.98, -22.97) * mm});
            skLineSegment(sketch, "E4.6.15.13", {"start": v(46.9, -17.9) * mm, "end": v(46.9, -22.97) * mm});
            skLineSegment(sketch, "E4.9.15.13", {"start": v(51.98, -17.9) * mm, "end": v(51.98, -22.97) * mm});
            skLineSegment(sketch, "E4.0.15.14", {"start": v(46.9, -25.51) * mm, "end": v(51.98, -25.51) * mm});
            skLineSegment(sketch, "E4.3.15.14", {"start": v(46.9, -30.6) * mm, "end": v(51.98, -30.6) * mm});
            skLineSegment(sketch, "E4.6.15.14", {"start": v(46.9, -25.51) * mm, "end": v(46.9, -30.6) * mm});
            skLineSegment(sketch, "E4.9.15.14", {"start": v(51.98, -25.51) * mm, "end": v(51.98, -30.6) * mm});
            skLineSegment(sketch, "E4.0.15.15", {"start": v(46.9, -33.13) * mm, "end": v(51.98, -33.13) * mm});
            skLineSegment(sketch, "E4.3.15.15", {"start": v(46.9, -38.21) * mm, "end": v(51.98, -38.21) * mm});
            skLineSegment(sketch, "E4.6.15.15", {"start": v(46.9, -33.13) * mm, "end": v(46.9, -38.21) * mm});
            skLineSegment(sketch, "E4.9.15.15", {"start": v(51.98, -33.13) * mm, "end": v(51.98, -38.21) * mm});
            skLineSegment(sketch, "E4.0.15.16", {"start": v(46.9, -40.75) * mm, "end": v(51.98, -40.75) * mm});
            skLineSegment(sketch, "E4.3.15.16", {"start": v(46.9, -45.83) * mm, "end": v(51.98, -45.83) * mm});
            skLineSegment(sketch, "E4.6.15.16", {"start": v(46.9, -40.75) * mm, "end": v(46.9, -45.83) * mm});
            skLineSegment(sketch, "E4.9.15.16", {"start": v(51.98, -40.75) * mm, "end": v(51.98, -45.83) * mm});
            skLineSegment(sketch, "E4.0.15.17", {"start": v(46.9, -48.37) * mm, "end": v(51.98, -48.37) * mm});
            skLineSegment(sketch, "E4.3.15.17", {"start": v(46.9, -53.45) * mm, "end": v(51.98, -53.45) * mm});
            skLineSegment(sketch, "E4.6.15.17", {"start": v(46.9, -48.37) * mm, "end": v(46.9, -53.45) * mm});
            skLineSegment(sketch, "E4.9.15.17", {"start": v(51.98, -48.37) * mm, "end": v(51.98, -53.45) * mm});
            skLineSegment(sketch, "E4.0.15.18", {"start": v(46.9, -56) * mm, "end": v(51.98, -56) * mm});
            skLineSegment(sketch, "E4.3.15.18", {"start": v(46.9, -61.07) * mm, "end": v(51.98, -61.07) * mm});
            skLineSegment(sketch, "E4.6.15.18", {"start": v(46.9, -56) * mm, "end": v(46.9, -61.07) * mm});
            skLineSegment(sketch, "E4.9.15.18", {"start": v(51.98, -56) * mm, "end": v(51.98, -61.07) * mm});
            skLineSegment(sketch, "E4.0.15.19", {"start": v(46.9, -63.61) * mm, "end": v(51.98, -63.61) * mm});
            skLineSegment(sketch, "E4.3.15.19", {"start": v(46.9, -68.7) * mm, "end": v(51.98, -68.7) * mm});
            skLineSegment(sketch, "E4.6.15.19", {"start": v(46.9, -63.61) * mm, "end": v(46.9, -68.7) * mm});
            skLineSegment(sketch, "E4.9.15.19", {"start": v(51.98, -63.61) * mm, "end": v(51.98, -68.7) * mm});
            skLineSegment(sketch, "E4.0.15.20", {"start": v(46.9, -71.23) * mm, "end": v(51.98, -71.23) * mm});
            skLineSegment(sketch, "E4.3.15.20", {"start": v(46.9, -76.31) * mm, "end": v(51.98, -76.31) * mm});
            skLineSegment(sketch, "E4.6.15.20", {"start": v(46.9, -71.23) * mm, "end": v(46.9, -76.31) * mm});
            skLineSegment(sketch, "E4.9.15.20", {"start": v(51.98, -71.23) * mm, "end": v(51.98, -76.31) * mm});
            skLineSegment(sketch, "E4.0.15.21", {"start": v(46.9, -78.85) * mm, "end": v(51.98, -78.85) * mm});
            skLineSegment(sketch, "E4.3.15.21", {"start": v(46.9, -83.93) * mm, "end": v(51.98, -83.93) * mm});
            skLineSegment(sketch, "E4.6.15.21", {"start": v(46.9, -78.85) * mm, "end": v(46.9, -83.93) * mm});
            skLineSegment(sketch, "E4.9.15.21", {"start": v(51.98, -78.85) * mm, "end": v(51.98, -83.93) * mm});
            skLineSegment(sketch, "E4.0.16.0", {"start": v(54.52, 81.17) * mm, "end": v(59.6, 81.17) * mm});
            skLineSegment(sketch, "E4.3.16.0", {"start": v(54.52, 76.09) * mm, "end": v(59.6, 76.09) * mm});
            skLineSegment(sketch, "E4.6.16.0", {"start": v(54.52, 81.17) * mm, "end": v(54.52, 76.09) * mm});
            skLineSegment(sketch, "E4.9.16.0", {"start": v(59.6, 81.17) * mm, "end": v(59.6, 76.09) * mm});
            skLineSegment(sketch, "E4.0.16.1", {"start": v(54.52, 73.55) * mm, "end": v(59.6, 73.55) * mm});
            skLineSegment(sketch, "E4.3.16.1", {"start": v(54.52, 68.47) * mm, "end": v(59.6, 68.47) * mm});
            skLineSegment(sketch, "E4.6.16.1", {"start": v(54.52, 73.55) * mm, "end": v(54.52, 68.47) * mm});
            skLineSegment(sketch, "E4.9.16.1", {"start": v(59.6, 73.55) * mm, "end": v(59.6, 68.47) * mm});
            skLineSegment(sketch, "E4.0.16.2", {"start": v(54.52, 65.93) * mm, "end": v(59.6, 65.93) * mm});
            skLineSegment(sketch, "E4.3.16.2", {"start": v(54.52, 60.85) * mm, "end": v(59.6, 60.85) * mm});
            skLineSegment(sketch, "E4.6.16.2", {"start": v(54.52, 65.93) * mm, "end": v(54.52, 60.85) * mm});
            skLineSegment(sketch, "E4.9.16.2", {"start": v(59.6, 65.93) * mm, "end": v(59.6, 60.85) * mm});
            skLineSegment(sketch, "E4.0.16.3", {"start": v(54.52, 58.3) * mm, "end": v(59.6, 58.3) * mm});
            skLineSegment(sketch, "E4.3.16.3", {"start": v(54.52, 53.23) * mm, "end": v(59.6, 53.23) * mm});
            skLineSegment(sketch, "E4.6.16.3", {"start": v(54.52, 58.3) * mm, "end": v(54.52, 53.23) * mm});
            skLineSegment(sketch, "E4.9.16.3", {"start": v(59.6, 58.3) * mm, "end": v(59.6, 53.23) * mm});
            skLineSegment(sketch, "E4.0.16.4", {"start": v(54.52, 50.69) * mm, "end": v(59.6, 50.69) * mm});
            skLineSegment(sketch, "E4.3.16.4", {"start": v(54.52, 45.6) * mm, "end": v(59.6, 45.6) * mm});
            skLineSegment(sketch, "E4.6.16.4", {"start": v(54.52, 50.69) * mm, "end": v(54.52, 45.6) * mm});
            skLineSegment(sketch, "E4.9.16.4", {"start": v(59.6, 50.69) * mm, "end": v(59.6, 45.6) * mm});
            skLineSegment(sketch, "E4.0.16.5", {"start": v(54.52, 43.07) * mm, "end": v(59.6, 43.07) * mm});
            skLineSegment(sketch, "E4.3.16.5", {"start": v(54.52, 37.99) * mm, "end": v(59.6, 37.99) * mm});
            skLineSegment(sketch, "E4.6.16.5", {"start": v(54.52, 43.07) * mm, "end": v(54.52, 37.99) * mm});
            skLineSegment(sketch, "E4.9.16.5", {"start": v(59.6, 43.07) * mm, "end": v(59.6, 37.99) * mm});
            skLineSegment(sketch, "E4.0.16.6", {"start": v(54.52, 35.45) * mm, "end": v(59.6, 35.45) * mm});
            skLineSegment(sketch, "E4.3.16.6", {"start": v(54.52, 30.37) * mm, "end": v(59.6, 30.37) * mm});
            skLineSegment(sketch, "E4.6.16.6", {"start": v(54.52, 35.45) * mm, "end": v(54.52, 30.37) * mm});
            skLineSegment(sketch, "E4.9.16.6", {"start": v(59.6, 35.45) * mm, "end": v(59.6, 30.37) * mm});
            skLineSegment(sketch, "E4.0.16.7", {"start": v(54.52, 27.83) * mm, "end": v(59.6, 27.83) * mm});
            skLineSegment(sketch, "E4.3.16.7", {"start": v(54.52, 22.75) * mm, "end": v(59.6, 22.75) * mm});
            skLineSegment(sketch, "E4.6.16.7", {"start": v(54.52, 27.83) * mm, "end": v(54.52, 22.75) * mm});
            skLineSegment(sketch, "E4.9.16.7", {"start": v(59.6, 27.83) * mm, "end": v(59.6, 22.75) * mm});
            skLineSegment(sketch, "E4.0.16.8", {"start": v(54.52, 20.2) * mm, "end": v(59.6, 20.2) * mm});
            skLineSegment(sketch, "E4.3.16.8", {"start": v(54.52, 15.13) * mm, "end": v(59.6, 15.13) * mm});
            skLineSegment(sketch, "E4.6.16.8", {"start": v(54.52, 20.2) * mm, "end": v(54.52, 15.13) * mm});
            skLineSegment(sketch, "E4.9.16.8", {"start": v(59.6, 20.2) * mm, "end": v(59.6, 15.13) * mm});
            skLineSegment(sketch, "E4.0.16.9", {"start": v(54.52, 12.59) * mm, "end": v(59.6, 12.59) * mm});
            skLineSegment(sketch, "E4.3.16.9", {"start": v(54.52, 7.5) * mm, "end": v(59.6, 7.5) * mm});
            skLineSegment(sketch, "E4.6.16.9", {"start": v(54.52, 12.59) * mm, "end": v(54.52, 7.5) * mm});
            skLineSegment(sketch, "E4.9.16.9", {"start": v(59.6, 12.59) * mm, "end": v(59.6, 7.5) * mm});
            skLineSegment(sketch, "E4.0.16.10", {"start": v(54.52, 4.97) * mm, "end": v(59.6, 4.97) * mm});
            skLineSegment(sketch, "E4.3.16.10", {"start": v(54.52, -0.11) * mm, "end": v(59.6, -0.11) * mm});
            skLineSegment(sketch, "E4.6.16.10", {"start": v(54.52, 4.97) * mm, "end": v(54.52, -0.11) * mm});
            skLineSegment(sketch, "E4.9.16.10", {"start": v(59.6, 4.97) * mm, "end": v(59.6, -0.11) * mm});
            skLineSegment(sketch, "E4.0.16.11", {"start": v(54.52, -2.65) * mm, "end": v(59.6, -2.65) * mm});
            skLineSegment(sketch, "E4.3.16.11", {"start": v(54.52, -7.73) * mm, "end": v(59.6, -7.73) * mm});
            skLineSegment(sketch, "E4.6.16.11", {"start": v(54.52, -2.65) * mm, "end": v(54.52, -7.73) * mm});
            skLineSegment(sketch, "E4.9.16.11", {"start": v(59.6, -2.65) * mm, "end": v(59.6, -7.73) * mm});
            skLineSegment(sketch, "E4.0.16.12", {"start": v(54.52, -10.27) * mm, "end": v(59.6, -10.27) * mm});
            skLineSegment(sketch, "E4.3.16.12", {"start": v(54.52, -15.35) * mm, "end": v(59.6, -15.35) * mm});
            skLineSegment(sketch, "E4.6.16.12", {"start": v(54.52, -10.27) * mm, "end": v(54.52, -15.35) * mm});
            skLineSegment(sketch, "E4.9.16.12", {"start": v(59.6, -10.27) * mm, "end": v(59.6, -15.35) * mm});
            skLineSegment(sketch, "E4.0.16.13", {"start": v(54.52, -17.9) * mm, "end": v(59.6, -17.9) * mm});
            skLineSegment(sketch, "E4.3.16.13", {"start": v(54.52, -22.97) * mm, "end": v(59.6, -22.97) * mm});
            skLineSegment(sketch, "E4.6.16.13", {"start": v(54.52, -17.9) * mm, "end": v(54.52, -22.97) * mm});
            skLineSegment(sketch, "E4.9.16.13", {"start": v(59.6, -17.9) * mm, "end": v(59.6, -22.97) * mm});
            skLineSegment(sketch, "E4.0.16.14", {"start": v(54.52, -25.51) * mm, "end": v(59.6, -25.51) * mm});
            skLineSegment(sketch, "E4.3.16.14", {"start": v(54.52, -30.6) * mm, "end": v(59.6, -30.6) * mm});
            skLineSegment(sketch, "E4.6.16.14", {"start": v(54.52, -25.51) * mm, "end": v(54.52, -30.6) * mm});
            skLineSegment(sketch, "E4.9.16.14", {"start": v(59.6, -25.51) * mm, "end": v(59.6, -30.6) * mm});
            skLineSegment(sketch, "E4.0.16.15", {"start": v(54.52, -33.13) * mm, "end": v(59.6, -33.13) * mm});
            skLineSegment(sketch, "E4.3.16.15", {"start": v(54.52, -38.21) * mm, "end": v(59.6, -38.21) * mm});
            skLineSegment(sketch, "E4.6.16.15", {"start": v(54.52, -33.13) * mm, "end": v(54.52, -38.21) * mm});
            skLineSegment(sketch, "E4.9.16.15", {"start": v(59.6, -33.13) * mm, "end": v(59.6, -38.21) * mm});
            skLineSegment(sketch, "E4.0.16.16", {"start": v(54.52, -40.75) * mm, "end": v(59.6, -40.75) * mm});
            skLineSegment(sketch, "E4.3.16.16", {"start": v(54.52, -45.83) * mm, "end": v(59.6, -45.83) * mm});
            skLineSegment(sketch, "E4.6.16.16", {"start": v(54.52, -40.75) * mm, "end": v(54.52, -45.83) * mm});
            skLineSegment(sketch, "E4.9.16.16", {"start": v(59.6, -40.75) * mm, "end": v(59.6, -45.83) * mm});
            skLineSegment(sketch, "E4.0.16.17", {"start": v(54.52, -48.37) * mm, "end": v(59.6, -48.37) * mm});
            skLineSegment(sketch, "E4.3.16.17", {"start": v(54.52, -53.45) * mm, "end": v(59.6, -53.45) * mm});
            skLineSegment(sketch, "E4.6.16.17", {"start": v(54.52, -48.37) * mm, "end": v(54.52, -53.45) * mm});
            skLineSegment(sketch, "E4.9.16.17", {"start": v(59.6, -48.37) * mm, "end": v(59.6, -53.45) * mm});
            skLineSegment(sketch, "E4.0.16.18", {"start": v(54.52, -56) * mm, "end": v(59.6, -56) * mm});
            skLineSegment(sketch, "E4.3.16.18", {"start": v(54.52, -61.07) * mm, "end": v(59.6, -61.07) * mm});
            skLineSegment(sketch, "E4.6.16.18", {"start": v(54.52, -56) * mm, "end": v(54.52, -61.07) * mm});
            skLineSegment(sketch, "E4.9.16.18", {"start": v(59.6, -56) * mm, "end": v(59.6, -61.07) * mm});
            skLineSegment(sketch, "E4.0.16.19", {"start": v(54.52, -63.61) * mm, "end": v(59.6, -63.61) * mm});
            skLineSegment(sketch, "E4.3.16.19", {"start": v(54.52, -68.7) * mm, "end": v(59.6, -68.7) * mm});
            skLineSegment(sketch, "E4.6.16.19", {"start": v(54.52, -63.61) * mm, "end": v(54.52, -68.7) * mm});
            skLineSegment(sketch, "E4.9.16.19", {"start": v(59.6, -63.61) * mm, "end": v(59.6, -68.7) * mm});
            skLineSegment(sketch, "E4.0.16.20", {"start": v(54.52, -71.23) * mm, "end": v(59.6, -71.23) * mm});
            skLineSegment(sketch, "E4.3.16.20", {"start": v(54.52, -76.31) * mm, "end": v(59.6, -76.31) * mm});
            skLineSegment(sketch, "E4.6.16.20", {"start": v(54.52, -71.23) * mm, "end": v(54.52, -76.31) * mm});
            skLineSegment(sketch, "E4.9.16.20", {"start": v(59.6, -71.23) * mm, "end": v(59.6, -76.31) * mm});
            skLineSegment(sketch, "E4.0.16.21", {"start": v(54.52, -78.85) * mm, "end": v(59.6, -78.85) * mm});
            skLineSegment(sketch, "E4.3.16.21", {"start": v(54.52, -83.93) * mm, "end": v(59.6, -83.93) * mm});
            skLineSegment(sketch, "E4.6.16.21", {"start": v(54.52, -78.85) * mm, "end": v(54.52, -83.93) * mm});
            skLineSegment(sketch, "E4.9.16.21", {"start": v(59.6, -78.85) * mm, "end": v(59.6, -83.93) * mm});
            skLineSegment(sketch, "E4.0.17.0", {"start": v(62.14, 81.17) * mm, "end": v(67.22, 81.17) * mm});
            skLineSegment(sketch, "E4.3.17.0", {"start": v(62.14, 76.09) * mm, "end": v(67.22, 76.09) * mm});
            skLineSegment(sketch, "E4.6.17.0", {"start": v(62.14, 81.17) * mm, "end": v(62.14, 76.09) * mm});
            skLineSegment(sketch, "E4.9.17.0", {"start": v(67.22, 81.17) * mm, "end": v(67.22, 76.09) * mm});
            skLineSegment(sketch, "E4.0.17.1", {"start": v(62.14, 73.55) * mm, "end": v(67.22, 73.55) * mm});
            skLineSegment(sketch, "E4.3.17.1", {"start": v(62.14, 68.47) * mm, "end": v(67.22, 68.47) * mm});
            skLineSegment(sketch, "E4.6.17.1", {"start": v(62.14, 73.55) * mm, "end": v(62.14, 68.47) * mm});
            skLineSegment(sketch, "E4.9.17.1", {"start": v(67.22, 73.55) * mm, "end": v(67.22, 68.47) * mm});
            skLineSegment(sketch, "E4.0.17.2", {"start": v(62.14, 65.93) * mm, "end": v(67.22, 65.93) * mm});
            skLineSegment(sketch, "E4.3.17.2", {"start": v(62.14, 60.85) * mm, "end": v(67.22, 60.85) * mm});
            skLineSegment(sketch, "E4.6.17.2", {"start": v(62.14, 65.93) * mm, "end": v(62.14, 60.85) * mm});
            skLineSegment(sketch, "E4.9.17.2", {"start": v(67.22, 65.93) * mm, "end": v(67.22, 60.85) * mm});
            skLineSegment(sketch, "E4.0.17.3", {"start": v(62.14, 58.3) * mm, "end": v(67.22, 58.3) * mm});
            skLineSegment(sketch, "E4.3.17.3", {"start": v(62.14, 53.23) * mm, "end": v(67.22, 53.23) * mm});
            skLineSegment(sketch, "E4.6.17.3", {"start": v(62.14, 58.3) * mm, "end": v(62.14, 53.23) * mm});
            skLineSegment(sketch, "E4.9.17.3", {"start": v(67.22, 58.3) * mm, "end": v(67.22, 53.23) * mm});
            skLineSegment(sketch, "E4.0.17.4", {"start": v(62.14, 50.69) * mm, "end": v(67.22, 50.69) * mm});
            skLineSegment(sketch, "E4.3.17.4", {"start": v(62.14, 45.6) * mm, "end": v(67.22, 45.6) * mm});
            skLineSegment(sketch, "E4.6.17.4", {"start": v(62.14, 50.69) * mm, "end": v(62.14, 45.6) * mm});
            skLineSegment(sketch, "E4.9.17.4", {"start": v(67.22, 50.69) * mm, "end": v(67.22, 45.6) * mm});
            skLineSegment(sketch, "E4.0.17.5", {"start": v(62.14, 43.07) * mm, "end": v(67.22, 43.07) * mm});
            skLineSegment(sketch, "E4.3.17.5", {"start": v(62.14, 37.99) * mm, "end": v(67.22, 37.99) * mm});
            skLineSegment(sketch, "E4.6.17.5", {"start": v(62.14, 43.07) * mm, "end": v(62.14, 37.99) * mm});
            skLineSegment(sketch, "E4.9.17.5", {"start": v(67.22, 43.07) * mm, "end": v(67.22, 37.99) * mm});
            skLineSegment(sketch, "E4.0.17.6", {"start": v(62.14, 35.45) * mm, "end": v(67.22, 35.45) * mm});
            skLineSegment(sketch, "E4.3.17.6", {"start": v(62.14, 30.37) * mm, "end": v(67.22, 30.37) * mm});
            skLineSegment(sketch, "E4.6.17.6", {"start": v(62.14, 35.45) * mm, "end": v(62.14, 30.37) * mm});
            skLineSegment(sketch, "E4.9.17.6", {"start": v(67.22, 35.45) * mm, "end": v(67.22, 30.37) * mm});
            skLineSegment(sketch, "E4.0.17.7", {"start": v(62.14, 27.83) * mm, "end": v(67.22, 27.83) * mm});
            skLineSegment(sketch, "E4.3.17.7", {"start": v(62.14, 22.75) * mm, "end": v(67.22, 22.75) * mm});
            skLineSegment(sketch, "E4.6.17.7", {"start": v(62.14, 27.83) * mm, "end": v(62.14, 22.75) * mm});
            skLineSegment(sketch, "E4.9.17.7", {"start": v(67.22, 27.83) * mm, "end": v(67.22, 22.75) * mm});
            skLineSegment(sketch, "E4.0.17.8", {"start": v(62.14, 20.2) * mm, "end": v(67.22, 20.2) * mm});
            skLineSegment(sketch, "E4.3.17.8", {"start": v(62.14, 15.13) * mm, "end": v(67.22, 15.13) * mm});
            skLineSegment(sketch, "E4.6.17.8", {"start": v(62.14, 20.2) * mm, "end": v(62.14, 15.13) * mm});
            skLineSegment(sketch, "E4.9.17.8", {"start": v(67.22, 20.2) * mm, "end": v(67.22, 15.13) * mm});
            skLineSegment(sketch, "E4.0.17.9", {"start": v(62.14, 12.59) * mm, "end": v(67.22, 12.59) * mm});
            skLineSegment(sketch, "E4.3.17.9", {"start": v(62.14, 7.5) * mm, "end": v(67.22, 7.5) * mm});
            skLineSegment(sketch, "E4.6.17.9", {"start": v(62.14, 12.59) * mm, "end": v(62.14, 7.5) * mm});
            skLineSegment(sketch, "E4.9.17.9", {"start": v(67.22, 12.59) * mm, "end": v(67.22, 7.5) * mm});
            skLineSegment(sketch, "E4.0.17.10", {"start": v(62.14, 4.97) * mm, "end": v(67.22, 4.97) * mm});
            skLineSegment(sketch, "E4.3.17.10", {"start": v(62.14, -0.11) * mm, "end": v(67.22, -0.11) * mm});
            skLineSegment(sketch, "E4.6.17.10", {"start": v(62.14, 4.97) * mm, "end": v(62.14, -0.11) * mm});
            skLineSegment(sketch, "E4.9.17.10", {"start": v(67.22, 4.97) * mm, "end": v(67.22, -0.11) * mm});
            skLineSegment(sketch, "E4.0.17.11", {"start": v(62.14, -2.65) * mm, "end": v(67.22, -2.65) * mm});
            skLineSegment(sketch, "E4.3.17.11", {"start": v(62.14, -7.73) * mm, "end": v(67.22, -7.73) * mm});
            skLineSegment(sketch, "E4.6.17.11", {"start": v(62.14, -2.65) * mm, "end": v(62.14, -7.73) * mm});
            skLineSegment(sketch, "E4.9.17.11", {"start": v(67.22, -2.65) * mm, "end": v(67.22, -7.73) * mm});
            skLineSegment(sketch, "E4.0.17.12", {"start": v(62.14, -10.27) * mm, "end": v(67.22, -10.27) * mm});
            skLineSegment(sketch, "E4.3.17.12", {"start": v(62.14, -15.35) * mm, "end": v(67.22, -15.35) * mm});
            skLineSegment(sketch, "E4.6.17.12", {"start": v(62.14, -10.27) * mm, "end": v(62.14, -15.35) * mm});
            skLineSegment(sketch, "E4.9.17.12", {"start": v(67.22, -10.27) * mm, "end": v(67.22, -15.35) * mm});
            skLineSegment(sketch, "E4.0.17.13", {"start": v(62.14, -17.9) * mm, "end": v(67.22, -17.9) * mm});
            skLineSegment(sketch, "E4.3.17.13", {"start": v(62.14, -22.97) * mm, "end": v(67.22, -22.97) * mm});
            skLineSegment(sketch, "E4.6.17.13", {"start": v(62.14, -17.9) * mm, "end": v(62.14, -22.97) * mm});
            skLineSegment(sketch, "E4.9.17.13", {"start": v(67.22, -17.9) * mm, "end": v(67.22, -22.97) * mm});
            skLineSegment(sketch, "E4.0.17.14", {"start": v(62.14, -25.51) * mm, "end": v(67.22, -25.51) * mm});
            skLineSegment(sketch, "E4.3.17.14", {"start": v(62.14, -30.6) * mm, "end": v(67.22, -30.6) * mm});
            skLineSegment(sketch, "E4.6.17.14", {"start": v(62.14, -25.51) * mm, "end": v(62.14, -30.6) * mm});
            skLineSegment(sketch, "E4.9.17.14", {"start": v(67.22, -25.51) * mm, "end": v(67.22, -30.6) * mm});
            skLineSegment(sketch, "E4.0.17.15", {"start": v(62.14, -33.13) * mm, "end": v(67.22, -33.13) * mm});
            skLineSegment(sketch, "E4.3.17.15", {"start": v(62.14, -38.21) * mm, "end": v(67.22, -38.21) * mm});
            skLineSegment(sketch, "E4.6.17.15", {"start": v(62.14, -33.13) * mm, "end": v(62.14, -38.21) * mm});
            skLineSegment(sketch, "E4.9.17.15", {"start": v(67.22, -33.13) * mm, "end": v(67.22, -38.21) * mm});
            skLineSegment(sketch, "E4.0.17.16", {"start": v(62.14, -40.75) * mm, "end": v(67.22, -40.75) * mm});
            skLineSegment(sketch, "E4.3.17.16", {"start": v(62.14, -45.83) * mm, "end": v(67.22, -45.83) * mm});
            skLineSegment(sketch, "E4.6.17.16", {"start": v(62.14, -40.75) * mm, "end": v(62.14, -45.83) * mm});
            skLineSegment(sketch, "E4.9.17.16", {"start": v(67.22, -40.75) * mm, "end": v(67.22, -45.83) * mm});
            skLineSegment(sketch, "E4.0.17.17", {"start": v(62.14, -48.37) * mm, "end": v(67.22, -48.37) * mm});
            skLineSegment(sketch, "E4.3.17.17", {"start": v(62.14, -53.45) * mm, "end": v(67.22, -53.45) * mm});
            skLineSegment(sketch, "E4.6.17.17", {"start": v(62.14, -48.37) * mm, "end": v(62.14, -53.45) * mm});
            skLineSegment(sketch, "E4.9.17.17", {"start": v(67.22, -48.37) * mm, "end": v(67.22, -53.45) * mm});
            skLineSegment(sketch, "E4.0.17.18", {"start": v(62.14, -56) * mm, "end": v(67.22, -56) * mm});
            skLineSegment(sketch, "E4.3.17.18", {"start": v(62.14, -61.07) * mm, "end": v(67.22, -61.07) * mm});
            skLineSegment(sketch, "E4.6.17.18", {"start": v(62.14, -56) * mm, "end": v(62.14, -61.07) * mm});
            skLineSegment(sketch, "E4.9.17.18", {"start": v(67.22, -56) * mm, "end": v(67.22, -61.07) * mm});
            skLineSegment(sketch, "E4.0.17.19", {"start": v(62.14, -63.61) * mm, "end": v(67.22, -63.61) * mm});
            skLineSegment(sketch, "E4.3.17.19", {"start": v(62.14, -68.7) * mm, "end": v(67.22, -68.7) * mm});
            skLineSegment(sketch, "E4.6.17.19", {"start": v(62.14, -63.61) * mm, "end": v(62.14, -68.7) * mm});
            skLineSegment(sketch, "E4.9.17.19", {"start": v(67.22, -63.61) * mm, "end": v(67.22, -68.7) * mm});
            skLineSegment(sketch, "E4.0.17.20", {"start": v(62.14, -71.23) * mm, "end": v(67.22, -71.23) * mm});
            skLineSegment(sketch, "E4.3.17.20", {"start": v(62.14, -76.31) * mm, "end": v(67.22, -76.31) * mm});
            skLineSegment(sketch, "E4.6.17.20", {"start": v(62.14, -71.23) * mm, "end": v(62.14, -76.31) * mm});
            skLineSegment(sketch, "E4.9.17.20", {"start": v(67.22, -71.23) * mm, "end": v(67.22, -76.31) * mm});
            skLineSegment(sketch, "E4.0.17.21", {"start": v(62.14, -78.85) * mm, "end": v(67.22, -78.85) * mm});
            skLineSegment(sketch, "E4.3.17.21", {"start": v(62.14, -83.93) * mm, "end": v(67.22, -83.93) * mm});
            skLineSegment(sketch, "E4.6.17.21", {"start": v(62.14, -78.85) * mm, "end": v(62.14, -83.93) * mm});
            skLineSegment(sketch, "E4.9.17.21", {"start": v(67.22, -78.85) * mm, "end": v(67.22, -83.93) * mm});
            skLineSegment(sketch, "E4.0.18.0", {"start": v(69.76, 81.17) * mm, "end": v(74.84, 81.17) * mm});
            skLineSegment(sketch, "E4.3.18.0", {"start": v(69.76, 76.09) * mm, "end": v(74.84, 76.09) * mm});
            skLineSegment(sketch, "E4.6.18.0", {"start": v(69.76, 81.17) * mm, "end": v(69.76, 76.09) * mm});
            skLineSegment(sketch, "E4.9.18.0", {"start": v(74.84, 81.17) * mm, "end": v(74.84, 76.09) * mm});
            skLineSegment(sketch, "E4.0.18.1", {"start": v(69.76, 73.55) * mm, "end": v(74.84, 73.55) * mm});
            skLineSegment(sketch, "E4.3.18.1", {"start": v(69.76, 68.47) * mm, "end": v(74.84, 68.47) * mm});
            skLineSegment(sketch, "E4.6.18.1", {"start": v(69.76, 73.55) * mm, "end": v(69.76, 68.47) * mm});
            skLineSegment(sketch, "E4.9.18.1", {"start": v(74.84, 73.55) * mm, "end": v(74.84, 68.47) * mm});
            skLineSegment(sketch, "E4.0.18.2", {"start": v(69.76, 65.93) * mm, "end": v(74.84, 65.93) * mm});
            skLineSegment(sketch, "E4.3.18.2", {"start": v(69.76, 60.85) * mm, "end": v(74.84, 60.85) * mm});
            skLineSegment(sketch, "E4.6.18.2", {"start": v(69.76, 65.93) * mm, "end": v(69.76, 60.85) * mm});
            skLineSegment(sketch, "E4.9.18.2", {"start": v(74.84, 65.93) * mm, "end": v(74.84, 60.85) * mm});
            skLineSegment(sketch, "E4.0.18.3", {"start": v(69.76, 58.3) * mm, "end": v(74.84, 58.3) * mm});
            skLineSegment(sketch, "E4.3.18.3", {"start": v(69.76, 53.23) * mm, "end": v(74.84, 53.23) * mm});
            skLineSegment(sketch, "E4.6.18.3", {"start": v(69.76, 58.3) * mm, "end": v(69.76, 53.23) * mm});
            skLineSegment(sketch, "E4.9.18.3", {"start": v(74.84, 58.3) * mm, "end": v(74.84, 53.23) * mm});
            skLineSegment(sketch, "E4.0.18.4", {"start": v(69.76, 50.69) * mm, "end": v(74.84, 50.69) * mm});
            skLineSegment(sketch, "E4.3.18.4", {"start": v(69.76, 45.6) * mm, "end": v(74.84, 45.6) * mm});
            skLineSegment(sketch, "E4.6.18.4", {"start": v(69.76, 50.69) * mm, "end": v(69.76, 45.6) * mm});
            skLineSegment(sketch, "E4.9.18.4", {"start": v(74.84, 50.69) * mm, "end": v(74.84, 45.6) * mm});
            skLineSegment(sketch, "E4.0.18.5", {"start": v(69.76, 43.07) * mm, "end": v(74.84, 43.07) * mm});
            skLineSegment(sketch, "E4.3.18.5", {"start": v(69.76, 37.99) * mm, "end": v(74.84, 37.99) * mm});
            skLineSegment(sketch, "E4.6.18.5", {"start": v(69.76, 43.07) * mm, "end": v(69.76, 37.99) * mm});
            skLineSegment(sketch, "E4.9.18.5", {"start": v(74.84, 43.07) * mm, "end": v(74.84, 37.99) * mm});
            skLineSegment(sketch, "E4.0.18.6", {"start": v(69.76, 35.45) * mm, "end": v(74.84, 35.45) * mm});
            skLineSegment(sketch, "E4.3.18.6", {"start": v(69.76, 30.37) * mm, "end": v(74.84, 30.37) * mm});
            skLineSegment(sketch, "E4.6.18.6", {"start": v(69.76, 35.45) * mm, "end": v(69.76, 30.37) * mm});
            skLineSegment(sketch, "E4.9.18.6", {"start": v(74.84, 35.45) * mm, "end": v(74.84, 30.37) * mm});
            skLineSegment(sketch, "E4.0.18.7", {"start": v(69.76, 27.83) * mm, "end": v(74.84, 27.83) * mm});
            skLineSegment(sketch, "E4.3.18.7", {"start": v(69.76, 22.75) * mm, "end": v(74.84, 22.75) * mm});
            skLineSegment(sketch, "E4.6.18.7", {"start": v(69.76, 27.83) * mm, "end": v(69.76, 22.75) * mm});
            skLineSegment(sketch, "E4.9.18.7", {"start": v(74.84, 27.83) * mm, "end": v(74.84, 22.75) * mm});
            skLineSegment(sketch, "E4.0.18.8", {"start": v(69.76, 20.2) * mm, "end": v(74.84, 20.2) * mm});
            skLineSegment(sketch, "E4.3.18.8", {"start": v(69.76, 15.13) * mm, "end": v(74.84, 15.13) * mm});
            skLineSegment(sketch, "E4.6.18.8", {"start": v(69.76, 20.2) * mm, "end": v(69.76, 15.13) * mm});
            skLineSegment(sketch, "E4.9.18.8", {"start": v(74.84, 20.2) * mm, "end": v(74.84, 15.13) * mm});
            skLineSegment(sketch, "E4.0.18.9", {"start": v(69.76, 12.59) * mm, "end": v(74.84, 12.59) * mm});
            skLineSegment(sketch, "E4.3.18.9", {"start": v(69.76, 7.5) * mm, "end": v(74.84, 7.5) * mm});
            skLineSegment(sketch, "E4.6.18.9", {"start": v(69.76, 12.59) * mm, "end": v(69.76, 7.5) * mm});
            skLineSegment(sketch, "E4.9.18.9", {"start": v(74.84, 12.59) * mm, "end": v(74.84, 7.5) * mm});
            skLineSegment(sketch, "E4.0.18.10", {"start": v(69.76, 4.97) * mm, "end": v(74.84, 4.97) * mm});
            skLineSegment(sketch, "E4.3.18.10", {"start": v(69.76, -0.11) * mm, "end": v(74.84, -0.11) * mm});
            skLineSegment(sketch, "E4.6.18.10", {"start": v(69.76, 4.97) * mm, "end": v(69.76, -0.11) * mm});
            skLineSegment(sketch, "E4.9.18.10", {"start": v(74.84, 4.97) * mm, "end": v(74.84, -0.11) * mm});
            skLineSegment(sketch, "E4.0.18.11", {"start": v(69.76, -2.65) * mm, "end": v(74.84, -2.65) * mm});
            skLineSegment(sketch, "E4.3.18.11", {"start": v(69.76, -7.73) * mm, "end": v(74.84, -7.73) * mm});
            skLineSegment(sketch, "E4.6.18.11", {"start": v(69.76, -2.65) * mm, "end": v(69.76, -7.73) * mm});
            skLineSegment(sketch, "E4.9.18.11", {"start": v(74.84, -2.65) * mm, "end": v(74.84, -7.73) * mm});
            skLineSegment(sketch, "E4.0.18.12", {"start": v(69.76, -10.27) * mm, "end": v(74.84, -10.27) * mm});
            skLineSegment(sketch, "E4.3.18.12", {"start": v(69.76, -15.35) * mm, "end": v(74.84, -15.35) * mm});
            skLineSegment(sketch, "E4.6.18.12", {"start": v(69.76, -10.27) * mm, "end": v(69.76, -15.35) * mm});
            skLineSegment(sketch, "E4.9.18.12", {"start": v(74.84, -10.27) * mm, "end": v(74.84, -15.35) * mm});
            skLineSegment(sketch, "E4.0.18.13", {"start": v(69.76, -17.9) * mm, "end": v(74.84, -17.9) * mm});
            skLineSegment(sketch, "E4.3.18.13", {"start": v(69.76, -22.97) * mm, "end": v(74.84, -22.97) * mm});
            skLineSegment(sketch, "E4.6.18.13", {"start": v(69.76, -17.9) * mm, "end": v(69.76, -22.97) * mm});
            skLineSegment(sketch, "E4.9.18.13", {"start": v(74.84, -17.9) * mm, "end": v(74.84, -22.97) * mm});
            skLineSegment(sketch, "E4.0.18.14", {"start": v(69.76, -25.51) * mm, "end": v(74.84, -25.51) * mm});
            skLineSegment(sketch, "E4.3.18.14", {"start": v(69.76, -30.6) * mm, "end": v(74.84, -30.6) * mm});
            skLineSegment(sketch, "E4.6.18.14", {"start": v(69.76, -25.51) * mm, "end": v(69.76, -30.6) * mm});
            skLineSegment(sketch, "E4.9.18.14", {"start": v(74.84, -25.51) * mm, "end": v(74.84, -30.6) * mm});
            skLineSegment(sketch, "E4.0.18.15", {"start": v(69.76, -33.13) * mm, "end": v(74.84, -33.13) * mm});
            skLineSegment(sketch, "E4.3.18.15", {"start": v(69.76, -38.21) * mm, "end": v(74.84, -38.21) * mm});
            skLineSegment(sketch, "E4.6.18.15", {"start": v(69.76, -33.13) * mm, "end": v(69.76, -38.21) * mm});
            skLineSegment(sketch, "E4.9.18.15", {"start": v(74.84, -33.13) * mm, "end": v(74.84, -38.21) * mm});
            skLineSegment(sketch, "E4.0.18.16", {"start": v(69.76, -40.75) * mm, "end": v(74.84, -40.75) * mm});
            skLineSegment(sketch, "E4.3.18.16", {"start": v(69.76, -45.83) * mm, "end": v(74.84, -45.83) * mm});
            skLineSegment(sketch, "E4.6.18.16", {"start": v(69.76, -40.75) * mm, "end": v(69.76, -45.83) * mm});
            skLineSegment(sketch, "E4.9.18.16", {"start": v(74.84, -40.75) * mm, "end": v(74.84, -45.83) * mm});
            skLineSegment(sketch, "E4.0.18.17", {"start": v(69.76, -48.37) * mm, "end": v(74.84, -48.37) * mm});
            skLineSegment(sketch, "E4.3.18.17", {"start": v(69.76, -53.45) * mm, "end": v(74.84, -53.45) * mm});
            skLineSegment(sketch, "E4.6.18.17", {"start": v(69.76, -48.37) * mm, "end": v(69.76, -53.45) * mm});
            skLineSegment(sketch, "E4.9.18.17", {"start": v(74.84, -48.37) * mm, "end": v(74.84, -53.45) * mm});
            skLineSegment(sketch, "E4.0.18.18", {"start": v(69.76, -56) * mm, "end": v(74.84, -56) * mm});
            skLineSegment(sketch, "E4.3.18.18", {"start": v(69.76, -61.07) * mm, "end": v(74.84, -61.07) * mm});
            skLineSegment(sketch, "E4.6.18.18", {"start": v(69.76, -56) * mm, "end": v(69.76, -61.07) * mm});
            skLineSegment(sketch, "E4.9.18.18", {"start": v(74.84, -56) * mm, "end": v(74.84, -61.07) * mm});
            skLineSegment(sketch, "E4.0.18.19", {"start": v(69.76, -63.61) * mm, "end": v(74.84, -63.61) * mm});
            skLineSegment(sketch, "E4.3.18.19", {"start": v(69.76, -68.7) * mm, "end": v(74.84, -68.7) * mm});
            skLineSegment(sketch, "E4.6.18.19", {"start": v(69.76, -63.61) * mm, "end": v(69.76, -68.7) * mm});
            skLineSegment(sketch, "E4.9.18.19", {"start": v(74.84, -63.61) * mm, "end": v(74.84, -68.7) * mm});
            skLineSegment(sketch, "E4.0.18.20", {"start": v(69.76, -71.23) * mm, "end": v(74.84, -71.23) * mm});
            skLineSegment(sketch, "E4.3.18.20", {"start": v(69.76, -76.31) * mm, "end": v(74.84, -76.31) * mm});
            skLineSegment(sketch, "E4.6.18.20", {"start": v(69.76, -71.23) * mm, "end": v(69.76, -76.31) * mm});
            skLineSegment(sketch, "E4.9.18.20", {"start": v(74.84, -71.23) * mm, "end": v(74.84, -76.31) * mm});
            skLineSegment(sketch, "E4.0.18.21", {"start": v(69.76, -78.85) * mm, "end": v(74.84, -78.85) * mm});
            skLineSegment(sketch, "E4.3.18.21", {"start": v(69.76, -83.93) * mm, "end": v(74.84, -83.93) * mm});
            skLineSegment(sketch, "E4.6.18.21", {"start": v(69.76, -78.85) * mm, "end": v(69.76, -83.93) * mm});
            skLineSegment(sketch, "E4.9.18.21", {"start": v(74.84, -78.85) * mm, "end": v(74.84, -83.93) * mm});
            skSolve(sketch);
        }
        {
            var Q0;
            Q0 = qSketchRegion(id + "F2", true);
            extrude(context, id + "F3", {"entities" : qUnion([Q0]), "operationType" : NewBodyOperationType.REMOVE, "oppositeDirection" : true, "depth" : 25.4 * mm});
        }
        {
            var Q0;
            Q0=makeQuery(id+"F1.opExtrude","CAP_FACE",FACE,{"disambiguationData":[OSD([sQuery(id+"F0.wireOp",EDGE,"E0")])],"isStart":false});
            var sketch = newSketch(context, id + "F4", { "sketchPlane" : qUnion([Q0])});
            skLineSegment(sketch, "E5.bottom", {"start": v(-75.02, 81.16) * mm, "end": v(-69.94, 81.16) * mm});
            skLineSegment(sketch, "E5.top", {"start": v(-75.02, 76.08) * mm, "end": v(-69.94, 76.08) * mm});
            skLineSegment(sketch, "E5.left", {"start": v(-75.02, 81.16) * mm, "end": v(-75.02, 76.08) * mm});
            skLineSegment(sketch, "E5.right", {"start": v(-69.94, 81.16) * mm, "end": v(-69.94, 76.08) * mm});
            skLineSegment(sketch, "E6.0.1.0", {"start": v(-75.02, 73.54) * mm, "end": v(-75.02, 68.46) * mm});
            skLineSegment(sketch, "E6.0.1.1", {"start": v(-75.02, 73.54) * mm, "end": v(-69.94, 73.54) * mm});
            skLineSegment(sketch, "E6.0.1.2", {"start": v(-69.94, 73.54) * mm, "end": v(-69.94, 68.46) * mm});
            skLineSegment(sketch, "E6.0.1.3", {"start": v(-75.02, 68.46) * mm, "end": v(-69.94, 68.46) * mm});
            skLineSegment(sketch, "E6.0.2.0", {"start": v(-75.02, 65.92) * mm, "end": v(-75.02, 60.84) * mm});
            skLineSegment(sketch, "E6.0.2.1", {"start": v(-75.02, 65.92) * mm, "end": v(-69.94, 65.92) * mm});
            skLineSegment(sketch, "E6.0.2.2", {"start": v(-69.94, 65.92) * mm, "end": v(-69.94, 60.84) * mm});
            skLineSegment(sketch, "E6.0.2.3", {"start": v(-75.02, 60.84) * mm, "end": v(-69.94, 60.84) * mm});
            skLineSegment(sketch, "E6.0.3.0", {"start": v(-75.02, 58.3) * mm, "end": v(-75.02, 53.22) * mm});
            skLineSegment(sketch, "E6.0.3.1", {"start": v(-75.02, 58.3) * mm, "end": v(-69.94, 58.3) * mm});
            skLineSegment(sketch, "E6.0.3.2", {"start": v(-69.94, 58.3) * mm, "end": v(-69.94, 53.22) * mm});
            skLineSegment(sketch, "E6.0.3.3", {"start": v(-75.02, 53.22) * mm, "end": v(-69.94, 53.22) * mm});
            skLineSegment(sketch, "E6.0.4.0", {"start": v(-75.02, 50.68) * mm, "end": v(-75.02, 45.6) * mm});
            skLineSegment(sketch, "E6.0.4.1", {"start": v(-75.02, 50.68) * mm, "end": v(-69.94, 50.68) * mm});
            skLineSegment(sketch, "E6.0.4.2", {"start": v(-69.94, 50.68) * mm, "end": v(-69.94, 45.6) * mm});
            skLineSegment(sketch, "E6.0.4.3", {"start": v(-75.02, 45.6) * mm, "end": v(-69.94, 45.6) * mm});
            skLineSegment(sketch, "E6.0.5.0", {"start": v(-75.02, 43.06) * mm, "end": v(-75.02, 37.98) * mm});
            skLineSegment(sketch, "E6.0.5.1", {"start": v(-75.02, 43.06) * mm, "end": v(-69.94, 43.06) * mm});
            skLineSegment(sketch, "E6.0.5.2", {"start": v(-69.94, 43.06) * mm, "end": v(-69.94, 37.98) * mm});
            skLineSegment(sketch, "E6.0.5.3", {"start": v(-75.02, 37.98) * mm, "end": v(-69.94, 37.98) * mm});
            skLineSegment(sketch, "E6.0.6.0", {"start": v(-75.02, 35.44) * mm, "end": v(-75.02, 30.36) * mm});
            skLineSegment(sketch, "E6.0.6.1", {"start": v(-75.02, 35.44) * mm, "end": v(-69.94, 35.44) * mm});
            skLineSegment(sketch, "E6.0.6.2", {"start": v(-69.94, 35.44) * mm, "end": v(-69.94, 30.36) * mm});
            skLineSegment(sketch, "E6.0.6.3", {"start": v(-75.02, 30.36) * mm, "end": v(-69.94, 30.36) * mm});
            skLineSegment(sketch, "E6.0.7.0", {"start": v(-75.02, 27.82) * mm, "end": v(-75.02, 22.74) * mm});
            skLineSegment(sketch, "E6.0.7.1", {"start": v(-75.02, 27.82) * mm, "end": v(-69.94, 27.82) * mm});
            skLineSegment(sketch, "E6.0.7.2", {"start": v(-69.94, 27.82) * mm, "end": v(-69.94, 22.74) * mm});
            skLineSegment(sketch, "E6.0.7.3", {"start": v(-75.02, 22.74) * mm, "end": v(-69.94, 22.74) * mm});
            skLineSegment(sketch, "E6.0.8.0", {"start": v(-75.02, 20.2) * mm, "end": v(-75.02, 15.12) * mm});
            skLineSegment(sketch, "E6.0.8.1", {"start": v(-75.02, 20.2) * mm, "end": v(-69.94, 20.2) * mm});
            skLineSegment(sketch, "E6.0.8.2", {"start": v(-69.94, 20.2) * mm, "end": v(-69.94, 15.12) * mm});
            skLineSegment(sketch, "E6.0.8.3", {"start": v(-75.02, 15.12) * mm, "end": v(-69.94, 15.12) * mm});
            skLineSegment(sketch, "E6.0.9.0", {"start": v(-75.02, 12.58) * mm, "end": v(-75.02, 7.5) * mm});
            skLineSegment(sketch, "E6.0.9.1", {"start": v(-75.02, 12.58) * mm, "end": v(-69.94, 12.58) * mm});
            skLineSegment(sketch, "E6.0.9.2", {"start": v(-69.94, 12.58) * mm, "end": v(-69.94, 7.5) * mm});
            skLineSegment(sketch, "E6.0.9.3", {"start": v(-75.02, 7.5) * mm, "end": v(-69.94, 7.5) * mm});
            skLineSegment(sketch, "E6.0.10.0", {"start": v(-75.02, 4.96) * mm, "end": v(-75.02, -0.12) * mm});
            skLineSegment(sketch, "E6.0.10.1", {"start": v(-75.02, 4.96) * mm, "end": v(-69.94, 4.96) * mm});
            skLineSegment(sketch, "E6.0.10.2", {"start": v(-69.94, 4.96) * mm, "end": v(-69.94, -0.12) * mm});
            skLineSegment(sketch, "E6.0.10.3", {"start": v(-75.02, -0.12) * mm, "end": v(-69.94, -0.12) * mm});
            skLineSegment(sketch, "E6.0.11.0", {"start": v(-75.02, -2.66) * mm, "end": v(-75.02, -7.74) * mm});
            skLineSegment(sketch, "E6.0.11.1", {"start": v(-75.02, -2.66) * mm, "end": v(-69.94, -2.66) * mm});
            skLineSegment(sketch, "E6.0.11.2", {"start": v(-69.94, -2.66) * mm, "end": v(-69.94, -7.74) * mm});
            skLineSegment(sketch, "E6.0.11.3", {"start": v(-75.02, -7.74) * mm, "end": v(-69.94, -7.74) * mm});
            skLineSegment(sketch, "E6.0.12.0", {"start": v(-75.02, -10.28) * mm, "end": v(-75.02, -15.36) * mm});
            skLineSegment(sketch, "E6.0.12.1", {"start": v(-75.02, -10.28) * mm, "end": v(-69.94, -10.28) * mm});
            skLineSegment(sketch, "E6.0.12.2", {"start": v(-69.94, -10.28) * mm, "end": v(-69.94, -15.36) * mm});
            skLineSegment(sketch, "E6.0.12.3", {"start": v(-75.02, -15.36) * mm, "end": v(-69.94, -15.36) * mm});
            skLineSegment(sketch, "E6.0.13.0", {"start": v(-75.02, -17.9) * mm, "end": v(-75.02, -22.98) * mm});
            skLineSegment(sketch, "E6.0.13.1", {"start": v(-75.02, -17.9) * mm, "end": v(-69.94, -17.9) * mm});
            skLineSegment(sketch, "E6.0.13.2", {"start": v(-69.94, -17.9) * mm, "end": v(-69.94, -22.98) * mm});
            skLineSegment(sketch, "E6.0.13.3", {"start": v(-75.02, -22.98) * mm, "end": v(-69.94, -22.98) * mm});
            skLineSegment(sketch, "E6.0.14.0", {"start": v(-75.02, -25.52) * mm, "end": v(-75.02, -30.6) * mm});
            skLineSegment(sketch, "E6.0.14.1", {"start": v(-75.02, -25.52) * mm, "end": v(-69.94, -25.52) * mm});
            skLineSegment(sketch, "E6.0.14.2", {"start": v(-69.94, -25.52) * mm, "end": v(-69.94, -30.6) * mm});
            skLineSegment(sketch, "E6.0.14.3", {"start": v(-75.02, -30.6) * mm, "end": v(-69.94, -30.6) * mm});
            skLineSegment(sketch, "E6.0.15.0", {"start": v(-75.02, -33.14) * mm, "end": v(-75.02, -38.22) * mm});
            skLineSegment(sketch, "E6.0.15.1", {"start": v(-75.02, -33.14) * mm, "end": v(-69.94, -33.14) * mm});
            skLineSegment(sketch, "E6.0.15.2", {"start": v(-69.94, -33.14) * mm, "end": v(-69.94, -38.22) * mm});
            skLineSegment(sketch, "E6.0.15.3", {"start": v(-75.02, -38.22) * mm, "end": v(-69.94, -38.22) * mm});
            skLineSegment(sketch, "E6.0.16.0", {"start": v(-75.02, -40.76) * mm, "end": v(-75.02, -45.84) * mm});
            skLineSegment(sketch, "E6.0.16.1", {"start": v(-75.02, -40.76) * mm, "end": v(-69.94, -40.76) * mm});
            skLineSegment(sketch, "E6.0.16.2", {"start": v(-69.94, -40.76) * mm, "end": v(-69.94, -45.84) * mm});
            skLineSegment(sketch, "E6.0.16.3", {"start": v(-75.02, -45.84) * mm, "end": v(-69.94, -45.84) * mm});
            skLineSegment(sketch, "E6.0.17.0", {"start": v(-75.02, -48.38) * mm, "end": v(-75.02, -53.46) * mm});
            skLineSegment(sketch, "E6.0.17.1", {"start": v(-75.02, -48.38) * mm, "end": v(-69.94, -48.38) * mm});
            skLineSegment(sketch, "E6.0.17.2", {"start": v(-69.94, -48.38) * mm, "end": v(-69.94, -53.46) * mm});
            skLineSegment(sketch, "E6.0.17.3", {"start": v(-75.02, -53.46) * mm, "end": v(-69.94, -53.46) * mm});
            skLineSegment(sketch, "E6.0.18.0", {"start": v(-75.02, -56) * mm, "end": v(-75.02, -61.08) * mm});
            skLineSegment(sketch, "E6.0.18.1", {"start": v(-75.02, -56) * mm, "end": v(-69.94, -56) * mm});
            skLineSegment(sketch, "E6.0.18.2", {"start": v(-69.94, -56) * mm, "end": v(-69.94, -61.08) * mm});
            skLineSegment(sketch, "E6.0.18.3", {"start": v(-75.02, -61.08) * mm, "end": v(-69.94, -61.08) * mm});
            skLineSegment(sketch, "E6.0.19.0", {"start": v(-75.02, -63.62) * mm, "end": v(-75.02, -68.7) * mm});
            skLineSegment(sketch, "E6.0.19.1", {"start": v(-75.02, -63.62) * mm, "end": v(-69.94, -63.62) * mm});
            skLineSegment(sketch, "E6.0.19.2", {"start": v(-69.94, -63.62) * mm, "end": v(-69.94, -68.7) * mm});
            skLineSegment(sketch, "E6.0.19.3", {"start": v(-75.02, -68.7) * mm, "end": v(-69.94, -68.7) * mm});
            skLineSegment(sketch, "E6.1.1.0", {"start": v(-82.64, 73.54) * mm, "end": v(-82.64, 68.46) * mm});
            skLineSegment(sketch, "E6.1.1.1", {"start": v(-82.64, 73.54) * mm, "end": v(-77.56, 73.54) * mm});
            skLineSegment(sketch, "E6.1.1.2", {"start": v(-77.56, 73.54) * mm, "end": v(-77.56, 68.46) * mm});
            skLineSegment(sketch, "E6.1.1.3", {"start": v(-82.64, 68.46) * mm, "end": v(-77.56, 68.46) * mm});
            skLineSegment(sketch, "E6.1.2.0", {"start": v(-82.64, 65.92) * mm, "end": v(-82.64, 60.84) * mm});
            skLineSegment(sketch, "E6.1.2.1", {"start": v(-82.64, 65.92) * mm, "end": v(-77.56, 65.92) * mm});
            skLineSegment(sketch, "E6.1.2.2", {"start": v(-77.56, 65.92) * mm, "end": v(-77.56, 60.84) * mm});
            skLineSegment(sketch, "E6.1.2.3", {"start": v(-82.64, 60.84) * mm, "end": v(-77.56, 60.84) * mm});
            skLineSegment(sketch, "E6.1.3.0", {"start": v(-82.64, 58.3) * mm, "end": v(-82.64, 53.22) * mm});
            skLineSegment(sketch, "E6.1.3.1", {"start": v(-82.64, 58.3) * mm, "end": v(-77.56, 58.3) * mm});
            skLineSegment(sketch, "E6.1.3.2", {"start": v(-77.56, 58.3) * mm, "end": v(-77.56, 53.22) * mm});
            skLineSegment(sketch, "E6.1.3.3", {"start": v(-82.64, 53.22) * mm, "end": v(-77.56, 53.22) * mm});
            skLineSegment(sketch, "E6.1.4.0", {"start": v(-82.64, 50.68) * mm, "end": v(-82.64, 45.6) * mm});
            skLineSegment(sketch, "E6.1.4.1", {"start": v(-82.64, 50.68) * mm, "end": v(-77.56, 50.68) * mm});
            skLineSegment(sketch, "E6.1.4.2", {"start": v(-77.56, 50.68) * mm, "end": v(-77.56, 45.6) * mm});
            skLineSegment(sketch, "E6.1.4.3", {"start": v(-82.64, 45.6) * mm, "end": v(-77.56, 45.6) * mm});
            skLineSegment(sketch, "E6.1.5.0", {"start": v(-82.64, 43.06) * mm, "end": v(-82.64, 37.98) * mm});
            skLineSegment(sketch, "E6.1.5.1", {"start": v(-82.64, 43.06) * mm, "end": v(-77.56, 43.06) * mm});
            skLineSegment(sketch, "E6.1.5.2", {"start": v(-77.56, 43.06) * mm, "end": v(-77.56, 37.98) * mm});
            skLineSegment(sketch, "E6.1.5.3", {"start": v(-82.64, 37.98) * mm, "end": v(-77.56, 37.98) * mm});
            skLineSegment(sketch, "E6.1.6.0", {"start": v(-82.64, 35.44) * mm, "end": v(-82.64, 30.36) * mm});
            skLineSegment(sketch, "E6.1.6.1", {"start": v(-82.64, 35.44) * mm, "end": v(-77.56, 35.44) * mm});
            skLineSegment(sketch, "E6.1.6.2", {"start": v(-77.56, 35.44) * mm, "end": v(-77.56, 30.36) * mm});
            skLineSegment(sketch, "E6.1.6.3", {"start": v(-82.64, 30.36) * mm, "end": v(-77.56, 30.36) * mm});
            skLineSegment(sketch, "E6.1.7.0", {"start": v(-82.64, 27.82) * mm, "end": v(-82.64, 22.74) * mm});
            skLineSegment(sketch, "E6.1.7.1", {"start": v(-82.64, 27.82) * mm, "end": v(-77.56, 27.82) * mm});
            skLineSegment(sketch, "E6.1.7.2", {"start": v(-77.56, 27.82) * mm, "end": v(-77.56, 22.74) * mm});
            skLineSegment(sketch, "E6.1.7.3", {"start": v(-82.64, 22.74) * mm, "end": v(-77.56, 22.74) * mm});
            skLineSegment(sketch, "E6.1.8.0", {"start": v(-82.64, 20.2) * mm, "end": v(-82.64, 15.12) * mm});
            skLineSegment(sketch, "E6.1.8.1", {"start": v(-82.64, 20.2) * mm, "end": v(-77.56, 20.2) * mm});
            skLineSegment(sketch, "E6.1.8.2", {"start": v(-77.56, 20.2) * mm, "end": v(-77.56, 15.12) * mm});
            skLineSegment(sketch, "E6.1.8.3", {"start": v(-82.64, 15.12) * mm, "end": v(-77.56, 15.12) * mm});
            skLineSegment(sketch, "E6.1.9.0", {"start": v(-82.64, 12.58) * mm, "end": v(-82.64, 7.5) * mm});
            skLineSegment(sketch, "E6.1.9.1", {"start": v(-82.64, 12.58) * mm, "end": v(-77.56, 12.58) * mm});
            skLineSegment(sketch, "E6.1.9.2", {"start": v(-77.56, 12.58) * mm, "end": v(-77.56, 7.5) * mm});
            skLineSegment(sketch, "E6.1.9.3", {"start": v(-82.64, 7.5) * mm, "end": v(-77.56, 7.5) * mm});
            skLineSegment(sketch, "E6.1.10.0", {"start": v(-82.64, 4.96) * mm, "end": v(-82.64, -0.12) * mm});
            skLineSegment(sketch, "E6.1.10.1", {"start": v(-82.64, 4.96) * mm, "end": v(-77.56, 4.96) * mm});
            skLineSegment(sketch, "E6.1.10.2", {"start": v(-77.56, 4.96) * mm, "end": v(-77.56, -0.12) * mm});
            skLineSegment(sketch, "E6.1.10.3", {"start": v(-82.64, -0.12) * mm, "end": v(-77.56, -0.12) * mm});
            skLineSegment(sketch, "E6.1.11.0", {"start": v(-82.64, -2.66) * mm, "end": v(-82.64, -7.74) * mm});
            skLineSegment(sketch, "E6.1.11.1", {"start": v(-82.64, -2.66) * mm, "end": v(-77.56, -2.66) * mm});
            skLineSegment(sketch, "E6.1.11.2", {"start": v(-77.56, -2.66) * mm, "end": v(-77.56, -7.74) * mm});
            skLineSegment(sketch, "E6.1.11.3", {"start": v(-82.64, -7.74) * mm, "end": v(-77.56, -7.74) * mm});
            skLineSegment(sketch, "E6.1.12.0", {"start": v(-82.64, -10.28) * mm, "end": v(-82.64, -15.36) * mm});
            skLineSegment(sketch, "E6.1.12.1", {"start": v(-82.64, -10.28) * mm, "end": v(-77.56, -10.28) * mm});
            skLineSegment(sketch, "E6.1.12.2", {"start": v(-77.56, -10.28) * mm, "end": v(-77.56, -15.36) * mm});
            skLineSegment(sketch, "E6.1.12.3", {"start": v(-82.64, -15.36) * mm, "end": v(-77.56, -15.36) * mm});
            skLineSegment(sketch, "E6.1.13.0", {"start": v(-82.64, -17.9) * mm, "end": v(-82.64, -22.98) * mm});
            skLineSegment(sketch, "E6.1.13.1", {"start": v(-82.64, -17.9) * mm, "end": v(-77.56, -17.9) * mm});
            skLineSegment(sketch, "E6.1.13.2", {"start": v(-77.56, -17.9) * mm, "end": v(-77.56, -22.98) * mm});
            skLineSegment(sketch, "E6.1.13.3", {"start": v(-82.64, -22.98) * mm, "end": v(-77.56, -22.98) * mm});
            skLineSegment(sketch, "E6.1.14.0", {"start": v(-82.64, -25.52) * mm, "end": v(-82.64, -30.6) * mm});
            skLineSegment(sketch, "E6.1.14.1", {"start": v(-82.64, -25.52) * mm, "end": v(-77.56, -25.52) * mm});
            skLineSegment(sketch, "E6.1.14.2", {"start": v(-77.56, -25.52) * mm, "end": v(-77.56, -30.6) * mm});
            skLineSegment(sketch, "E6.1.14.3", {"start": v(-82.64, -30.6) * mm, "end": v(-77.56, -30.6) * mm});
            skLineSegment(sketch, "E6.1.15.0", {"start": v(-82.64, -33.14) * mm, "end": v(-82.64, -38.22) * mm});
            skLineSegment(sketch, "E6.1.15.1", {"start": v(-82.64, -33.14) * mm, "end": v(-77.56, -33.14) * mm});
            skLineSegment(sketch, "E6.1.15.2", {"start": v(-77.56, -33.14) * mm, "end": v(-77.56, -38.22) * mm});
            skLineSegment(sketch, "E6.1.15.3", {"start": v(-82.64, -38.22) * mm, "end": v(-77.56, -38.22) * mm});
            skLineSegment(sketch, "E6.1.16.0", {"start": v(-82.64, -40.76) * mm, "end": v(-82.64, -45.84) * mm});
            skLineSegment(sketch, "E6.1.16.1", {"start": v(-82.64, -40.76) * mm, "end": v(-77.56, -40.76) * mm});
            skLineSegment(sketch, "E6.1.16.2", {"start": v(-77.56, -40.76) * mm, "end": v(-77.56, -45.84) * mm});
            skLineSegment(sketch, "E6.1.16.3", {"start": v(-82.64, -45.84) * mm, "end": v(-77.56, -45.84) * mm});
            skLineSegment(sketch, "E6.1.17.0", {"start": v(-82.64, -48.38) * mm, "end": v(-82.64, -53.46) * mm});
            skLineSegment(sketch, "E6.1.17.1", {"start": v(-82.64, -48.38) * mm, "end": v(-77.56, -48.38) * mm});
            skLineSegment(sketch, "E6.1.17.2", {"start": v(-77.56, -48.38) * mm, "end": v(-77.56, -53.46) * mm});
            skLineSegment(sketch, "E6.1.17.3", {"start": v(-82.64, -53.46) * mm, "end": v(-77.56, -53.46) * mm});
            skLineSegment(sketch, "E6.1.18.0", {"start": v(-82.64, -56) * mm, "end": v(-82.64, -61.08) * mm});
            skLineSegment(sketch, "E6.1.18.1", {"start": v(-82.64, -56) * mm, "end": v(-77.56, -56) * mm});
            skLineSegment(sketch, "E6.1.18.2", {"start": v(-77.56, -56) * mm, "end": v(-77.56, -61.08) * mm});
            skLineSegment(sketch, "E6.1.18.3", {"start": v(-82.64, -61.08) * mm, "end": v(-77.56, -61.08) * mm});
            skLineSegment(sketch, "E6.1.19.0", {"start": v(-82.64, -63.62) * mm, "end": v(-82.64, -68.7) * mm});
            skLineSegment(sketch, "E6.1.19.1", {"start": v(-82.64, -63.62) * mm, "end": v(-77.56, -63.62) * mm});
            skLineSegment(sketch, "E6.1.19.2", {"start": v(-77.56, -63.62) * mm, "end": v(-77.56, -68.7) * mm});
            skLineSegment(sketch, "E6.1.19.3", {"start": v(-82.64, -68.7) * mm, "end": v(-77.56, -68.7) * mm});
            skLineSegment(sketch, "E6.2.2.0", {"start": v(-90.26, 65.92) * mm, "end": v(-90.26, 60.84) * mm});
            skLineSegment(sketch, "E6.2.2.1", {"start": v(-90.26, 65.92) * mm, "end": v(-85.18, 65.92) * mm});
            skLineSegment(sketch, "E6.2.2.2", {"start": v(-85.18, 65.92) * mm, "end": v(-85.18, 60.84) * mm});
            skLineSegment(sketch, "E6.2.2.3", {"start": v(-90.26, 60.84) * mm, "end": v(-85.18, 60.84) * mm});
            skLineSegment(sketch, "E6.2.3.0", {"start": v(-90.26, 58.3) * mm, "end": v(-90.26, 53.22) * mm});
            skLineSegment(sketch, "E6.2.3.1", {"start": v(-90.26, 58.3) * mm, "end": v(-85.18, 58.3) * mm});
            skLineSegment(sketch, "E6.2.3.2", {"start": v(-85.18, 58.3) * mm, "end": v(-85.18, 53.22) * mm});
            skLineSegment(sketch, "E6.2.3.3", {"start": v(-90.26, 53.22) * mm, "end": v(-85.18, 53.22) * mm});
            skLineSegment(sketch, "E6.2.4.0", {"start": v(-90.26, 50.68) * mm, "end": v(-90.26, 45.6) * mm});
            skLineSegment(sketch, "E6.2.4.1", {"start": v(-90.26, 50.68) * mm, "end": v(-85.18, 50.68) * mm});
            skLineSegment(sketch, "E6.2.4.2", {"start": v(-85.18, 50.68) * mm, "end": v(-85.18, 45.6) * mm});
            skLineSegment(sketch, "E6.2.4.3", {"start": v(-90.26, 45.6) * mm, "end": v(-85.18, 45.6) * mm});
            skLineSegment(sketch, "E6.2.5.0", {"start": v(-90.26, 43.06) * mm, "end": v(-90.26, 37.98) * mm});
            skLineSegment(sketch, "E6.2.5.1", {"start": v(-90.26, 43.06) * mm, "end": v(-85.18, 43.06) * mm});
            skLineSegment(sketch, "E6.2.5.2", {"start": v(-85.18, 43.06) * mm, "end": v(-85.18, 37.98) * mm});
            skLineSegment(sketch, "E6.2.5.3", {"start": v(-90.26, 37.98) * mm, "end": v(-85.18, 37.98) * mm});
            skLineSegment(sketch, "E6.2.6.0", {"start": v(-90.26, 35.44) * mm, "end": v(-90.26, 30.36) * mm});
            skLineSegment(sketch, "E6.2.6.1", {"start": v(-90.26, 35.44) * mm, "end": v(-85.18, 35.44) * mm});
            skLineSegment(sketch, "E6.2.6.2", {"start": v(-85.18, 35.44) * mm, "end": v(-85.18, 30.36) * mm});
            skLineSegment(sketch, "E6.2.6.3", {"start": v(-90.26, 30.36) * mm, "end": v(-85.18, 30.36) * mm});
            skLineSegment(sketch, "E6.2.7.0", {"start": v(-90.26, 27.82) * mm, "end": v(-90.26, 22.74) * mm});
            skLineSegment(sketch, "E6.2.7.1", {"start": v(-90.26, 27.82) * mm, "end": v(-85.18, 27.82) * mm});
            skLineSegment(sketch, "E6.2.7.2", {"start": v(-85.18, 27.82) * mm, "end": v(-85.18, 22.74) * mm});
            skLineSegment(sketch, "E6.2.7.3", {"start": v(-90.26, 22.74) * mm, "end": v(-85.18, 22.74) * mm});
            skLineSegment(sketch, "E6.2.8.0", {"start": v(-90.26, 20.2) * mm, "end": v(-90.26, 15.12) * mm});
            skLineSegment(sketch, "E6.2.8.1", {"start": v(-90.26, 20.2) * mm, "end": v(-85.18, 20.2) * mm});
            skLineSegment(sketch, "E6.2.8.2", {"start": v(-85.18, 20.2) * mm, "end": v(-85.18, 15.12) * mm});
            skLineSegment(sketch, "E6.2.8.3", {"start": v(-90.26, 15.12) * mm, "end": v(-85.18, 15.12) * mm});
            skLineSegment(sketch, "E6.2.9.0", {"start": v(-90.26, 12.58) * mm, "end": v(-90.26, 7.5) * mm});
            skLineSegment(sketch, "E6.2.9.1", {"start": v(-90.26, 12.58) * mm, "end": v(-85.18, 12.58) * mm});
            skLineSegment(sketch, "E6.2.9.2", {"start": v(-85.18, 12.58) * mm, "end": v(-85.18, 7.5) * mm});
            skLineSegment(sketch, "E6.2.9.3", {"start": v(-90.26, 7.5) * mm, "end": v(-85.18, 7.5) * mm});
            skLineSegment(sketch, "E6.2.10.0", {"start": v(-90.26, 4.96) * mm, "end": v(-90.26, -0.12) * mm});
            skLineSegment(sketch, "E6.2.10.1", {"start": v(-90.26, 4.96) * mm, "end": v(-85.18, 4.96) * mm});
            skLineSegment(sketch, "E6.2.10.2", {"start": v(-85.18, 4.96) * mm, "end": v(-85.18, -0.12) * mm});
            skLineSegment(sketch, "E6.2.10.3", {"start": v(-90.26, -0.12) * mm, "end": v(-85.18, -0.12) * mm});
            skLineSegment(sketch, "E6.2.11.0", {"start": v(-90.26, -2.66) * mm, "end": v(-90.26, -7.74) * mm});
            skLineSegment(sketch, "E6.2.11.1", {"start": v(-90.26, -2.66) * mm, "end": v(-85.18, -2.66) * mm});
            skLineSegment(sketch, "E6.2.11.2", {"start": v(-85.18, -2.66) * mm, "end": v(-85.18, -7.74) * mm});
            skLineSegment(sketch, "E6.2.11.3", {"start": v(-90.26, -7.74) * mm, "end": v(-85.18, -7.74) * mm});
            skLineSegment(sketch, "E6.2.12.0", {"start": v(-90.26, -10.28) * mm, "end": v(-90.26, -15.36) * mm});
            skLineSegment(sketch, "E6.2.12.1", {"start": v(-90.26, -10.28) * mm, "end": v(-85.18, -10.28) * mm});
            skLineSegment(sketch, "E6.2.12.2", {"start": v(-85.18, -10.28) * mm, "end": v(-85.18, -15.36) * mm});
            skLineSegment(sketch, "E6.2.12.3", {"start": v(-90.26, -15.36) * mm, "end": v(-85.18, -15.36) * mm});
            skLineSegment(sketch, "E6.2.13.0", {"start": v(-90.26, -17.9) * mm, "end": v(-90.26, -22.98) * mm});
            skLineSegment(sketch, "E6.2.13.1", {"start": v(-90.26, -17.9) * mm, "end": v(-85.18, -17.9) * mm});
            skLineSegment(sketch, "E6.2.13.2", {"start": v(-85.18, -17.9) * mm, "end": v(-85.18, -22.98) * mm});
            skLineSegment(sketch, "E6.2.13.3", {"start": v(-90.26, -22.98) * mm, "end": v(-85.18, -22.98) * mm});
            skLineSegment(sketch, "E6.2.14.0", {"start": v(-90.26, -25.52) * mm, "end": v(-90.26, -30.6) * mm});
            skLineSegment(sketch, "E6.2.14.1", {"start": v(-90.26, -25.52) * mm, "end": v(-85.18, -25.52) * mm});
            skLineSegment(sketch, "E6.2.14.2", {"start": v(-85.18, -25.52) * mm, "end": v(-85.18, -30.6) * mm});
            skLineSegment(sketch, "E6.2.14.3", {"start": v(-90.26, -30.6) * mm, "end": v(-85.18, -30.6) * mm});
            skLineSegment(sketch, "E6.2.15.0", {"start": v(-90.26, -33.14) * mm, "end": v(-90.26, -38.22) * mm});
            skLineSegment(sketch, "E6.2.15.1", {"start": v(-90.26, -33.14) * mm, "end": v(-85.18, -33.14) * mm});
            skLineSegment(sketch, "E6.2.15.2", {"start": v(-85.18, -33.14) * mm, "end": v(-85.18, -38.22) * mm});
            skLineSegment(sketch, "E6.2.15.3", {"start": v(-90.26, -38.22) * mm, "end": v(-85.18, -38.22) * mm});
            skLineSegment(sketch, "E6.2.16.0", {"start": v(-90.26, -40.76) * mm, "end": v(-90.26, -45.84) * mm});
            skLineSegment(sketch, "E6.2.16.1", {"start": v(-90.26, -40.76) * mm, "end": v(-85.18, -40.76) * mm});
            skLineSegment(sketch, "E6.2.16.2", {"start": v(-85.18, -40.76) * mm, "end": v(-85.18, -45.84) * mm});
            skLineSegment(sketch, "E6.2.16.3", {"start": v(-90.26, -45.84) * mm, "end": v(-85.18, -45.84) * mm});
            skLineSegment(sketch, "E6.2.17.0", {"start": v(-90.26, -48.38) * mm, "end": v(-90.26, -53.46) * mm});
            skLineSegment(sketch, "E6.2.17.1", {"start": v(-90.26, -48.38) * mm, "end": v(-85.18, -48.38) * mm});
            skLineSegment(sketch, "E6.2.17.2", {"start": v(-85.18, -48.38) * mm, "end": v(-85.18, -53.46) * mm});
            skLineSegment(sketch, "E6.2.17.3", {"start": v(-90.26, -53.46) * mm, "end": v(-85.18, -53.46) * mm});
            skLineSegment(sketch, "E6.2.18.0", {"start": v(-90.26, -56) * mm, "end": v(-90.26, -61.08) * mm});
            skLineSegment(sketch, "E6.2.18.1", {"start": v(-90.26, -56) * mm, "end": v(-85.18, -56) * mm});
            skLineSegment(sketch, "E6.2.18.2", {"start": v(-85.18, -56) * mm, "end": v(-85.18, -61.08) * mm});
            skLineSegment(sketch, "E6.2.18.3", {"start": v(-90.26, -61.08) * mm, "end": v(-85.18, -61.08) * mm});
            skLineSegment(sketch, "E6.2.19.0", {"start": v(-90.26, -63.62) * mm, "end": v(-90.26, -68.7) * mm});
            skLineSegment(sketch, "E6.2.19.1", {"start": v(-90.26, -63.62) * mm, "end": v(-85.18, -63.62) * mm});
            skLineSegment(sketch, "E6.2.19.2", {"start": v(-85.18, -63.62) * mm, "end": v(-85.18, -68.7) * mm});
            skLineSegment(sketch, "E6.2.19.3", {"start": v(-90.26, -68.7) * mm, "end": v(-85.18, -68.7) * mm});
            skLineSegment(sketch, "E6.3.3.0", {"start": v(-97.88, 58.3) * mm, "end": v(-97.88, 53.22) * mm});
            skLineSegment(sketch, "E6.3.3.1", {"start": v(-97.88, 58.3) * mm, "end": v(-92.8, 58.3) * mm});
            skLineSegment(sketch, "E6.3.3.2", {"start": v(-92.8, 58.3) * mm, "end": v(-92.8, 53.22) * mm});
            skLineSegment(sketch, "E6.3.3.3", {"start": v(-97.88, 53.22) * mm, "end": v(-92.8, 53.22) * mm});
            skLineSegment(sketch, "E6.3.4.0", {"start": v(-97.88, 50.68) * mm, "end": v(-97.88, 45.6) * mm});
            skLineSegment(sketch, "E6.3.4.1", {"start": v(-97.88, 50.68) * mm, "end": v(-92.8, 50.68) * mm});
            skLineSegment(sketch, "E6.3.4.2", {"start": v(-92.8, 50.68) * mm, "end": v(-92.8, 45.6) * mm});
            skLineSegment(sketch, "E6.3.4.3", {"start": v(-97.88, 45.6) * mm, "end": v(-92.8, 45.6) * mm});
            skLineSegment(sketch, "E6.3.5.0", {"start": v(-97.88, 43.06) * mm, "end": v(-97.88, 37.98) * mm});
            skLineSegment(sketch, "E6.3.5.1", {"start": v(-97.88, 43.06) * mm, "end": v(-92.8, 43.06) * mm});
            skLineSegment(sketch, "E6.3.5.2", {"start": v(-92.8, 43.06) * mm, "end": v(-92.8, 37.98) * mm});
            skLineSegment(sketch, "E6.3.5.3", {"start": v(-97.88, 37.98) * mm, "end": v(-92.8, 37.98) * mm});
            skLineSegment(sketch, "E6.3.6.0", {"start": v(-97.88, 35.44) * mm, "end": v(-97.88, 30.36) * mm});
            skLineSegment(sketch, "E6.3.6.1", {"start": v(-97.88, 35.44) * mm, "end": v(-92.8, 35.44) * mm});
            skLineSegment(sketch, "E6.3.6.2", {"start": v(-92.8, 35.44) * mm, "end": v(-92.8, 30.36) * mm});
            skLineSegment(sketch, "E6.3.6.3", {"start": v(-97.88, 30.36) * mm, "end": v(-92.8, 30.36) * mm});
            skLineSegment(sketch, "E6.3.7.0", {"start": v(-97.88, 27.82) * mm, "end": v(-97.88, 22.74) * mm});
            skLineSegment(sketch, "E6.3.7.1", {"start": v(-97.88, 27.82) * mm, "end": v(-92.8, 27.82) * mm});
            skLineSegment(sketch, "E6.3.7.2", {"start": v(-92.8, 27.82) * mm, "end": v(-92.8, 22.74) * mm});
            skLineSegment(sketch, "E6.3.7.3", {"start": v(-97.88, 22.74) * mm, "end": v(-92.8, 22.74) * mm});
            skLineSegment(sketch, "E6.3.8.0", {"start": v(-97.88, 20.2) * mm, "end": v(-97.88, 15.12) * mm});
            skLineSegment(sketch, "E6.3.8.1", {"start": v(-97.88, 20.2) * mm, "end": v(-92.8, 20.2) * mm});
            skLineSegment(sketch, "E6.3.8.2", {"start": v(-92.8, 20.2) * mm, "end": v(-92.8, 15.12) * mm});
            skLineSegment(sketch, "E6.3.8.3", {"start": v(-97.88, 15.12) * mm, "end": v(-92.8, 15.12) * mm});
            skLineSegment(sketch, "E6.3.9.0", {"start": v(-97.88, 12.58) * mm, "end": v(-97.88, 7.5) * mm});
            skLineSegment(sketch, "E6.3.9.1", {"start": v(-97.88, 12.58) * mm, "end": v(-92.8, 12.58) * mm});
            skLineSegment(sketch, "E6.3.9.2", {"start": v(-92.8, 12.58) * mm, "end": v(-92.8, 7.5) * mm});
            skLineSegment(sketch, "E6.3.9.3", {"start": v(-97.88, 7.5) * mm, "end": v(-92.8, 7.5) * mm});
            skLineSegment(sketch, "E6.3.10.0", {"start": v(-97.88, 4.96) * mm, "end": v(-97.88, -0.12) * mm});
            skLineSegment(sketch, "E6.3.10.1", {"start": v(-97.88, 4.96) * mm, "end": v(-92.8, 4.96) * mm});
            skLineSegment(sketch, "E6.3.10.2", {"start": v(-92.8, 4.96) * mm, "end": v(-92.8, -0.12) * mm});
            skLineSegment(sketch, "E6.3.10.3", {"start": v(-97.88, -0.12) * mm, "end": v(-92.8, -0.12) * mm});
            skLineSegment(sketch, "E6.3.11.0", {"start": v(-97.88, -2.66) * mm, "end": v(-97.88, -7.74) * mm});
            skLineSegment(sketch, "E6.3.11.1", {"start": v(-97.88, -2.66) * mm, "end": v(-92.8, -2.66) * mm});
            skLineSegment(sketch, "E6.3.11.2", {"start": v(-92.8, -2.66) * mm, "end": v(-92.8, -7.74) * mm});
            skLineSegment(sketch, "E6.3.11.3", {"start": v(-97.88, -7.74) * mm, "end": v(-92.8, -7.74) * mm});
            skLineSegment(sketch, "E6.3.12.0", {"start": v(-97.88, -10.28) * mm, "end": v(-97.88, -15.36) * mm});
            skLineSegment(sketch, "E6.3.12.1", {"start": v(-97.88, -10.28) * mm, "end": v(-92.8, -10.28) * mm});
            skLineSegment(sketch, "E6.3.12.2", {"start": v(-92.8, -10.28) * mm, "end": v(-92.8, -15.36) * mm});
            skLineSegment(sketch, "E6.3.12.3", {"start": v(-97.88, -15.36) * mm, "end": v(-92.8, -15.36) * mm});
            skLineSegment(sketch, "E6.3.13.0", {"start": v(-97.88, -17.9) * mm, "end": v(-97.88, -22.98) * mm});
            skLineSegment(sketch, "E6.3.13.1", {"start": v(-97.88, -17.9) * mm, "end": v(-92.8, -17.9) * mm});
            skLineSegment(sketch, "E6.3.13.2", {"start": v(-92.8, -17.9) * mm, "end": v(-92.8, -22.98) * mm});
            skLineSegment(sketch, "E6.3.13.3", {"start": v(-97.88, -22.98) * mm, "end": v(-92.8, -22.98) * mm});
            skLineSegment(sketch, "E6.3.14.0", {"start": v(-97.88, -25.52) * mm, "end": v(-97.88, -30.6) * mm});
            skLineSegment(sketch, "E6.3.14.1", {"start": v(-97.88, -25.52) * mm, "end": v(-92.8, -25.52) * mm});
            skLineSegment(sketch, "E6.3.14.2", {"start": v(-92.8, -25.52) * mm, "end": v(-92.8, -30.6) * mm});
            skLineSegment(sketch, "E6.3.14.3", {"start": v(-97.88, -30.6) * mm, "end": v(-92.8, -30.6) * mm});
            skLineSegment(sketch, "E6.3.15.0", {"start": v(-97.88, -33.14) * mm, "end": v(-97.88, -38.22) * mm});
            skLineSegment(sketch, "E6.3.15.1", {"start": v(-97.88, -33.14) * mm, "end": v(-92.8, -33.14) * mm});
            skLineSegment(sketch, "E6.3.15.2", {"start": v(-92.8, -33.14) * mm, "end": v(-92.8, -38.22) * mm});
            skLineSegment(sketch, "E6.3.15.3", {"start": v(-97.88, -38.22) * mm, "end": v(-92.8, -38.22) * mm});
            skLineSegment(sketch, "E6.3.16.0", {"start": v(-97.88, -40.76) * mm, "end": v(-97.88, -45.84) * mm});
            skLineSegment(sketch, "E6.3.16.1", {"start": v(-97.88, -40.76) * mm, "end": v(-92.8, -40.76) * mm});
            skLineSegment(sketch, "E6.3.16.2", {"start": v(-92.8, -40.76) * mm, "end": v(-92.8, -45.84) * mm});
            skLineSegment(sketch, "E6.3.16.3", {"start": v(-97.88, -45.84) * mm, "end": v(-92.8, -45.84) * mm});
            skLineSegment(sketch, "E6.3.17.0", {"start": v(-97.88, -48.38) * mm, "end": v(-97.88, -53.46) * mm});
            skLineSegment(sketch, "E6.3.17.1", {"start": v(-97.88, -48.38) * mm, "end": v(-92.8, -48.38) * mm});
            skLineSegment(sketch, "E6.3.17.2", {"start": v(-92.8, -48.38) * mm, "end": v(-92.8, -53.46) * mm});
            skLineSegment(sketch, "E6.3.17.3", {"start": v(-97.88, -53.46) * mm, "end": v(-92.8, -53.46) * mm});
            skLineSegment(sketch, "E6.4.5.0", {"start": v(-105.5, 43.06) * mm, "end": v(-105.5, 37.98) * mm});
            skLineSegment(sketch, "E6.4.5.1", {"start": v(-105.5, 43.06) * mm, "end": v(-100.42, 43.06) * mm});
            skLineSegment(sketch, "E6.4.5.2", {"start": v(-100.42, 43.06) * mm, "end": v(-100.42, 37.98) * mm});
            skLineSegment(sketch, "E6.4.5.3", {"start": v(-105.5, 37.98) * mm, "end": v(-100.42, 37.98) * mm});
            skLineSegment(sketch, "E6.4.6.0", {"start": v(-105.5, 35.44) * mm, "end": v(-105.5, 30.36) * mm});
            skLineSegment(sketch, "E6.4.6.1", {"start": v(-105.5, 35.44) * mm, "end": v(-100.42, 35.44) * mm});
            skLineSegment(sketch, "E6.4.6.2", {"start": v(-100.42, 35.44) * mm, "end": v(-100.42, 30.36) * mm});
            skLineSegment(sketch, "E6.4.6.3", {"start": v(-105.5, 30.36) * mm, "end": v(-100.42, 30.36) * mm});
            skLineSegment(sketch, "E6.4.7.0", {"start": v(-105.5, 27.82) * mm, "end": v(-105.5, 22.74) * mm});
            skLineSegment(sketch, "E6.4.7.1", {"start": v(-105.5, 27.82) * mm, "end": v(-100.42, 27.82) * mm});
            skLineSegment(sketch, "E6.4.7.2", {"start": v(-100.42, 27.82) * mm, "end": v(-100.42, 22.74) * mm});
            skLineSegment(sketch, "E6.4.7.3", {"start": v(-105.5, 22.74) * mm, "end": v(-100.42, 22.74) * mm});
            skLineSegment(sketch, "E6.4.8.0", {"start": v(-105.5, 20.2) * mm, "end": v(-105.5, 15.12) * mm});
            skLineSegment(sketch, "E6.4.8.1", {"start": v(-105.5, 20.2) * mm, "end": v(-100.42, 20.2) * mm});
            skLineSegment(sketch, "E6.4.8.2", {"start": v(-100.42, 20.2) * mm, "end": v(-100.42, 15.12) * mm});
            skLineSegment(sketch, "E6.4.8.3", {"start": v(-105.5, 15.12) * mm, "end": v(-100.42, 15.12) * mm});
            skLineSegment(sketch, "E6.4.9.0", {"start": v(-105.5, 12.58) * mm, "end": v(-105.5, 7.5) * mm});
            skLineSegment(sketch, "E6.4.9.1", {"start": v(-105.5, 12.58) * mm, "end": v(-100.42, 12.58) * mm});
            skLineSegment(sketch, "E6.4.9.2", {"start": v(-100.42, 12.58) * mm, "end": v(-100.42, 7.5) * mm});
            skLineSegment(sketch, "E6.4.9.3", {"start": v(-105.5, 7.5) * mm, "end": v(-100.42, 7.5) * mm});
            skLineSegment(sketch, "E6.4.10.0", {"start": v(-105.5, 4.96) * mm, "end": v(-105.5, -0.12) * mm});
            skLineSegment(sketch, "E6.4.10.1", {"start": v(-105.5, 4.96) * mm, "end": v(-100.42, 4.96) * mm});
            skLineSegment(sketch, "E6.4.10.2", {"start": v(-100.42, 4.96) * mm, "end": v(-100.42, -0.12) * mm});
            skLineSegment(sketch, "E6.4.10.3", {"start": v(-105.5, -0.12) * mm, "end": v(-100.42, -0.12) * mm});
            skLineSegment(sketch, "E6.4.11.0", {"start": v(-105.5, -2.66) * mm, "end": v(-105.5, -7.74) * mm});
            skLineSegment(sketch, "E6.4.11.1", {"start": v(-105.5, -2.66) * mm, "end": v(-100.42, -2.66) * mm});
            skLineSegment(sketch, "E6.4.11.2", {"start": v(-100.42, -2.66) * mm, "end": v(-100.42, -7.74) * mm});
            skLineSegment(sketch, "E6.4.11.3", {"start": v(-105.5, -7.74) * mm, "end": v(-100.42, -7.74) * mm});
            skLineSegment(sketch, "E6.4.12.0", {"start": v(-105.5, -10.28) * mm, "end": v(-105.5, -15.36) * mm});
            skLineSegment(sketch, "E6.4.12.1", {"start": v(-105.5, -10.28) * mm, "end": v(-100.42, -10.28) * mm});
            skLineSegment(sketch, "E6.4.12.2", {"start": v(-100.42, -10.28) * mm, "end": v(-100.42, -15.36) * mm});
            skLineSegment(sketch, "E6.4.12.3", {"start": v(-105.5, -15.36) * mm, "end": v(-100.42, -15.36) * mm});
            skLineSegment(sketch, "E6.4.13.0", {"start": v(-105.5, -17.9) * mm, "end": v(-105.5, -22.98) * mm});
            skLineSegment(sketch, "E6.4.13.1", {"start": v(-105.5, -17.9) * mm, "end": v(-100.42, -17.9) * mm});
            skLineSegment(sketch, "E6.4.13.2", {"start": v(-100.42, -17.9) * mm, "end": v(-100.42, -22.98) * mm});
            skLineSegment(sketch, "E6.4.13.3", {"start": v(-105.5, -22.98) * mm, "end": v(-100.42, -22.98) * mm});
            skLineSegment(sketch, "E6.4.14.0", {"start": v(-105.5, -25.52) * mm, "end": v(-105.5, -30.6) * mm});
            skLineSegment(sketch, "E6.4.14.1", {"start": v(-105.5, -25.52) * mm, "end": v(-100.42, -25.52) * mm});
            skLineSegment(sketch, "E6.4.14.2", {"start": v(-100.42, -25.52) * mm, "end": v(-100.42, -30.6) * mm});
            skLineSegment(sketch, "E6.4.14.3", {"start": v(-105.5, -30.6) * mm, "end": v(-100.42, -30.6) * mm});
            skLineSegment(sketch, "E6.4.15.0", {"start": v(-105.5, -33.14) * mm, "end": v(-105.5, -38.22) * mm});
            skLineSegment(sketch, "E6.4.15.1", {"start": v(-105.5, -33.14) * mm, "end": v(-100.42, -33.14) * mm});
            skLineSegment(sketch, "E6.4.15.2", {"start": v(-100.42, -33.14) * mm, "end": v(-100.42, -38.22) * mm});
            skLineSegment(sketch, "E6.4.15.3", {"start": v(-105.5, -38.22) * mm, "end": v(-100.42, -38.22) * mm});
            skLineSegment(sketch, "E6.direction1", {"start": v(-75.02, 76.08) * mm, "end": v(-82.64, 76.08) * mm, "construction": true});
            skLineSegment(sketch, "E6.direction2", {"start": v(-75.02, 76.08) * mm, "end": v(-75.02, 68.46) * mm, "construction": true});
            skLineSegment(sketch, "E7.0.0.20", {"start": v(-75.02, -71.24) * mm, "end": v(-75.02, -76.32) * mm});
            skLineSegment(sketch, "E7.3.0.20", {"start": v(-75.02, -71.24) * mm, "end": v(-69.94, -71.24) * mm});
            skLineSegment(sketch, "E7.6.0.20", {"start": v(-69.94, -71.24) * mm, "end": v(-69.94, -76.32) * mm});
            skLineSegment(sketch, "E7.9.0.20", {"start": v(-75.02, -76.32) * mm, "end": v(-69.94, -76.32) * mm});
            skLineSegment(sketch, "E7.0.0.21", {"start": v(-75.02, -78.86) * mm, "end": v(-75.02, -83.94) * mm});
            skLineSegment(sketch, "E7.3.0.21", {"start": v(-75.02, -78.86) * mm, "end": v(-69.94, -78.86) * mm});
            skLineSegment(sketch, "E7.6.0.21", {"start": v(-69.94, -78.86) * mm, "end": v(-69.94, -83.94) * mm});
            skLineSegment(sketch, "E7.9.0.21", {"start": v(-75.02, -83.94) * mm, "end": v(-69.94, -83.94) * mm});
            skLineSegment(sketch, "E7.0.1.20", {"start": v(-82.64, -71.24) * mm, "end": v(-82.64, -76.32) * mm});
            skLineSegment(sketch, "E7.3.1.20", {"start": v(-82.64, -71.24) * mm, "end": v(-77.56, -71.24) * mm});
            skLineSegment(sketch, "E7.6.1.20", {"start": v(-77.56, -71.24) * mm, "end": v(-77.56, -76.32) * mm});
            skLineSegment(sketch, "E7.9.1.20", {"start": v(-82.64, -76.32) * mm, "end": v(-77.56, -76.32) * mm});
            skLineSegment(sketch, "E8", {"start": v(3.72, -0.11) * mm, "end": v(3.72, 4.97) * mm});
            skLineSegment(sketch, "E9.MirrorCS", {"start": v(82.46, 73.54) * mm, "end": v(82.46, 68.46) * mm});
            skLineSegment(sketch, "E10.MirrorCS", {"start": v(77.38, 4.96) * mm, "end": v(77.38, -0.12) * mm});
            skLineSegment(sketch, "E11.MirrorCS", {"start": v(97.7, -48.38) * mm, "end": v(92.62, -48.38) * mm});
            skLineSegment(sketch, "E12.MirrorCS", {"start": v(97.7, 7.5) * mm, "end": v(92.62, 7.5) * mm});
            skLineSegment(sketch, "E13.MirrorCS", {"start": v(82.46, -40.76) * mm, "end": v(82.46, -45.84) * mm});
            skLineSegment(sketch, "E14.MirrorCS", {"start": v(85, -63.62) * mm, "end": v(85, -68.7) * mm});
            skLineSegment(sketch, "E15.MirrorCS", {"start": v(100.24, 20.2) * mm, "end": v(100.24, 15.12) * mm});
            skLineSegment(sketch, "E16.MirrorCS", {"start": v(105.32, 35.44) * mm, "end": v(105.32, 30.36) * mm});
            skLineSegment(sketch, "E17.MirrorCS", {"start": v(92.62, -10.28) * mm, "end": v(92.62, -15.36) * mm});
            skLineSegment(sketch, "E18.MirrorCS", {"start": v(97.7, 58.3) * mm, "end": v(97.7, 53.22) * mm});
            skLineSegment(sketch, "E19.MirrorCS", {"start": v(82.46, -71.24) * mm, "end": v(82.46, -76.32) * mm});
            skLineSegment(sketch, "E20.MirrorCS", {"start": v(105.32, 30.36) * mm, "end": v(100.24, 30.36) * mm});
            skLineSegment(sketch, "E21.MirrorCS", {"start": v(105.32, -17.9) * mm, "end": v(105.32, -22.98) * mm});
            skLineSegment(sketch, "E22.MirrorCS", {"start": v(97.7, 35.44) * mm, "end": v(97.7, 30.36) * mm});
            skLineSegment(sketch, "E23.MirrorCS", {"start": v(97.7, 35.44) * mm, "end": v(92.62, 35.44) * mm});
            skLineSegment(sketch, "E24.MirrorCS", {"start": v(82.46, -2.66) * mm, "end": v(77.38, -2.66) * mm});
            skLineSegment(sketch, "E25.MirrorCS", {"start": v(85, 43.06) * mm, "end": v(85, 37.98) * mm});
            skLineSegment(sketch, "E26.MirrorCS", {"start": v(82.46, -10.28) * mm, "end": v(77.38, -10.28) * mm});
            skLineSegment(sketch, "E27.MirrorCS", {"start": v(82.46, -76.32) * mm, "end": v(77.38, -76.32) * mm});
            skLineSegment(sketch, "E28.MirrorCS", {"start": v(92.62, -2.66) * mm, "end": v(92.62, -7.74) * mm});
            skLineSegment(sketch, "E29.MirrorCS", {"start": v(90.08, 53.22) * mm, "end": v(85, 53.22) * mm});
            skLineSegment(sketch, "E30.MirrorCS", {"start": v(82.46, 30.36) * mm, "end": v(77.38, 30.36) * mm});
            skLineSegment(sketch, "E31.MirrorCS", {"start": v(82.46, -30.6) * mm, "end": v(77.38, -30.6) * mm});
            skLineSegment(sketch, "E32.MirrorCS", {"start": v(77.38, -71.24) * mm, "end": v(77.38, -76.32) * mm});
            skLineSegment(sketch, "E33.MirrorCS", {"start": v(82.46, -48.38) * mm, "end": v(82.46, -53.46) * mm});
            skLineSegment(sketch, "E34.MirrorCS", {"start": v(90.08, 65.92) * mm, "end": v(90.08, 60.84) * mm});
            skLineSegment(sketch, "E35.MirrorCS", {"start": v(90.08, -25.52) * mm, "end": v(90.08, -30.6) * mm});
            skLineSegment(sketch, "E36.MirrorCS", {"start": v(90.08, 4.96) * mm, "end": v(90.08, -0.12) * mm});
            skLineSegment(sketch, "E37.MirrorCS", {"start": v(82.46, -15.36) * mm, "end": v(77.38, -15.36) * mm});
            skLineSegment(sketch, "E38.MirrorCS", {"start": v(97.7, 4.96) * mm, "end": v(97.7, -0.12) * mm});
            skLineSegment(sketch, "E39.MirrorCS", {"start": v(77.38, 50.68) * mm, "end": v(77.38, 45.6) * mm});
            skLineSegment(sketch, "E40.MirrorCS", {"start": v(90.08, -17.9) * mm, "end": v(85, -17.9) * mm});
            skLineSegment(sketch, "E41.MirrorCS", {"start": v(92.62, -33.14) * mm, "end": v(92.62, -38.22) * mm});
            skLineSegment(sketch, "E42.MirrorCS", {"start": v(82.46, -0.12) * mm, "end": v(77.38, -0.12) * mm});
            skLineSegment(sketch, "E43.MirrorCS", {"start": v(90.08, -7.74) * mm, "end": v(85, -7.74) * mm});
            skLineSegment(sketch, "E44.MirrorCS", {"start": v(90.08, -38.22) * mm, "end": v(85, -38.22) * mm});
            skLineSegment(sketch, "E45.MirrorCS", {"start": v(82.46, -25.52) * mm, "end": v(82.46, -30.6) * mm});
            skLineSegment(sketch, "E46.MirrorCS", {"start": v(97.7, 50.68) * mm, "end": v(97.7, 45.6) * mm});
            skLineSegment(sketch, "E47.MirrorCS", {"start": v(82.46, -56) * mm, "end": v(82.46, -61.08) * mm});
            skLineSegment(sketch, "E48.MirrorCS", {"start": v(100.24, 35.44) * mm, "end": v(100.24, 30.36) * mm});
            skLineSegment(sketch, "E49.MirrorCS", {"start": v(90.08, 43.06) * mm, "end": v(90.08, 37.98) * mm});
            skLineSegment(sketch, "E50.MirrorCS", {"start": v(82.46, 58.3) * mm, "end": v(82.46, 53.22) * mm});
            skLineSegment(sketch, "E51.MirrorCS", {"start": v(82.46, 50.68) * mm, "end": v(77.38, 50.68) * mm});
            skLineSegment(sketch, "E52.MirrorCS", {"start": v(85, 12.58) * mm, "end": v(85, 7.5) * mm});
            skLineSegment(sketch, "E53.MirrorCS", {"start": v(97.7, 30.36) * mm, "end": v(92.62, 30.36) * mm});
            skLineSegment(sketch, "E54.MirrorCS", {"start": v(90.08, -40.76) * mm, "end": v(90.08, -45.84) * mm});
            skLineSegment(sketch, "E55.MirrorCS", {"start": v(90.08, -10.28) * mm, "end": v(90.08, -15.36) * mm});
            skLineSegment(sketch, "E56.MirrorCS", {"start": v(90.08, 50.68) * mm, "end": v(90.08, 45.6) * mm});
            skLineSegment(sketch, "E57.MirrorCS", {"start": v(90.08, 4.96) * mm, "end": v(85, 4.96) * mm});
            skLineSegment(sketch, "E58.MirrorCS", {"start": v(97.7, -10.28) * mm, "end": v(92.62, -10.28) * mm});
            skLineSegment(sketch, "E59.MirrorCS", {"start": v(90.08, -17.9) * mm, "end": v(90.08, -22.98) * mm});
            skLineSegment(sketch, "E60.MirrorCS", {"start": v(100.24, 4.96) * mm, "end": v(100.24, -0.12) * mm});
            skLineSegment(sketch, "E61.MirrorCS", {"start": v(90.08, -61.08) * mm, "end": v(85, -61.08) * mm});
            skLineSegment(sketch, "E62.MirrorCS", {"start": v(90.08, 60.84) * mm, "end": v(85, 60.84) * mm});
            skLineSegment(sketch, "E63.MirrorCS", {"start": v(97.7, -0.12) * mm, "end": v(92.62, -0.12) * mm});
            skLineSegment(sketch, "E64.MirrorCS", {"start": v(82.46, 27.82) * mm, "end": v(82.46, 22.74) * mm});
            skLineSegment(sketch, "E65.MirrorCS", {"start": v(90.08, -48.38) * mm, "end": v(85, -48.38) * mm});
            skLineSegment(sketch, "E66.MirrorCS", {"start": v(92.62, -48.38) * mm, "end": v(92.62, -53.46) * mm});
            skLineSegment(sketch, "E67.MirrorCS", {"start": v(82.46, -56) * mm, "end": v(77.38, -56) * mm});
            skLineSegment(sketch, "E68.MirrorCS", {"start": v(90.08, 43.06) * mm, "end": v(85, 43.06) * mm});
            skLineSegment(sketch, "E69.MirrorCS", {"start": v(97.7, 27.82) * mm, "end": v(92.62, 27.82) * mm});
            skLineSegment(sketch, "E70.MirrorCS", {"start": v(97.7, -33.14) * mm, "end": v(92.62, -33.14) * mm});
            skLineSegment(sketch, "E71.MirrorCS", {"start": v(82.46, -61.08) * mm, "end": v(77.38, -61.08) * mm});
            skLineSegment(sketch, "E72.MirrorCS", {"start": v(82.46, 43.06) * mm, "end": v(82.46, 37.98) * mm});
            skLineSegment(sketch, "E73.MirrorCS", {"start": v(77.38, -48.38) * mm, "end": v(77.38, -53.46) * mm});
            skLineSegment(sketch, "E74.MirrorCS", {"start": v(97.7, 12.58) * mm, "end": v(92.62, 12.58) * mm});
            skLineSegment(sketch, "E75.MirrorCS", {"start": v(105.32, 12.58) * mm, "end": v(100.24, 12.58) * mm});
            skLineSegment(sketch, "E76.MirrorCS", {"start": v(105.32, -10.28) * mm, "end": v(100.24, -10.28) * mm});
            skLineSegment(sketch, "E77.MirrorCS", {"start": v(90.08, 45.6) * mm, "end": v(85, 45.6) * mm});
            skLineSegment(sketch, "E78.MirrorCS", {"start": v(90.08, -2.66) * mm, "end": v(90.08, -7.74) * mm});
            skLineSegment(sketch, "E79.MirrorCS", {"start": v(82.46, 15.12) * mm, "end": v(77.38, 15.12) * mm});
            skLineSegment(sketch, "E80.MirrorCS", {"start": v(90.08, 58.3) * mm, "end": v(90.08, 53.22) * mm});
            skLineSegment(sketch, "E81.MirrorCS", {"start": v(82.46, -2.66) * mm, "end": v(82.46, -7.74) * mm});
            skLineSegment(sketch, "E82.MirrorCS", {"start": v(82.46, -25.52) * mm, "end": v(77.38, -25.52) * mm});
            skLineSegment(sketch, "E83.MirrorCS", {"start": v(97.7, 37.98) * mm, "end": v(92.62, 37.98) * mm});
            skLineSegment(sketch, "E84.MirrorCS", {"start": v(82.46, -40.76) * mm, "end": v(77.38, -40.76) * mm});
            skLineSegment(sketch, "E85.MirrorCS", {"start": v(105.32, -33.14) * mm, "end": v(100.24, -33.14) * mm});
            skLineSegment(sketch, "E86.MirrorCS", {"start": v(105.32, 35.44) * mm, "end": v(100.24, 35.44) * mm});
            skLineSegment(sketch, "E87.MirrorCS", {"start": v(85, 35.44) * mm, "end": v(85, 30.36) * mm});
            skLineSegment(sketch, "E88.MirrorCS", {"start": v(82.46, 35.44) * mm, "end": v(82.46, 30.36) * mm});
            skLineSegment(sketch, "E89.MirrorCS", {"start": v(82.46, -17.9) * mm, "end": v(82.46, -22.98) * mm});
            skLineSegment(sketch, "E90.MirrorCS", {"start": v(82.46, 22.74) * mm, "end": v(77.38, 22.74) * mm});
            skLineSegment(sketch, "E91.MirrorCS", {"start": v(97.7, -48.38) * mm, "end": v(97.7, -53.46) * mm});
            skLineSegment(sketch, "E92.MirrorCS", {"start": v(105.32, -30.6) * mm, "end": v(100.24, -30.6) * mm});
            skLineSegment(sketch, "E93.MirrorCS", {"start": v(82.46, -33.14) * mm, "end": v(82.46, -38.22) * mm});
            skLineSegment(sketch, "E94.MirrorCS", {"start": v(97.7, -25.52) * mm, "end": v(97.7, -30.6) * mm});
            skLineSegment(sketch, "E95.MirrorCS", {"start": v(82.46, -33.14) * mm, "end": v(77.38, -33.14) * mm});
            skLineSegment(sketch, "E96.MirrorCS", {"start": v(82.46, -63.62) * mm, "end": v(77.38, -63.62) * mm});
            skLineSegment(sketch, "E97.MirrorCS", {"start": v(77.38, 58.3) * mm, "end": v(77.38, 53.22) * mm});
            skLineSegment(sketch, "E98.MirrorCS", {"start": v(77.38, 12.58) * mm, "end": v(77.38, 7.5) * mm});
            skLineSegment(sketch, "E99.MirrorCS", {"start": v(85, 65.92) * mm, "end": v(85, 60.84) * mm});
            skLineSegment(sketch, "E100.MirrorCS", {"start": v(82.46, 4.96) * mm, "end": v(82.46, -0.12) * mm});
            skLineSegment(sketch, "E101.MirrorCS", {"start": v(90.08, -33.14) * mm, "end": v(85, -33.14) * mm});
            skLineSegment(sketch, "E102.MirrorCS", {"start": v(97.7, 45.6) * mm, "end": v(92.62, 45.6) * mm});
            skLineSegment(sketch, "E103.MirrorCS", {"start": v(105.32, 4.96) * mm, "end": v(100.24, 4.96) * mm});
            skLineSegment(sketch, "E104.MirrorCS", {"start": v(82.46, 37.98) * mm, "end": v(77.38, 37.98) * mm});
            skLineSegment(sketch, "E105.MirrorCS", {"start": v(90.08, 30.36) * mm, "end": v(85, 30.36) * mm});
            skLineSegment(sketch, "E106.MirrorCS", {"start": v(77.38, 65.92) * mm, "end": v(77.38, 60.84) * mm});
            skLineSegment(sketch, "E107.MirrorCS", {"start": v(82.46, 65.92) * mm, "end": v(77.38, 65.92) * mm});
            skLineSegment(sketch, "E108.MirrorCS", {"start": v(105.32, -22.98) * mm, "end": v(100.24, -22.98) * mm});
            skLineSegment(sketch, "E109.MirrorCS", {"start": v(85, -48.38) * mm, "end": v(85, -53.46) * mm});
            skLineSegment(sketch, "E110.MirrorCS", {"start": v(97.7, -30.6) * mm, "end": v(92.62, -30.6) * mm});
            skLineSegment(sketch, "E111.MirrorCS", {"start": v(105.32, -7.74) * mm, "end": v(100.24, -7.74) * mm});
            skLineSegment(sketch, "E112.MirrorCS", {"start": v(90.08, -0.12) * mm, "end": v(85, -0.12) * mm});
            skLineSegment(sketch, "E113.MirrorCS", {"start": v(105.32, 27.82) * mm, "end": v(105.32, 22.74) * mm});
            skLineSegment(sketch, "E114.MirrorCS", {"start": v(85, -17.9) * mm, "end": v(85, -22.98) * mm});
            skLineSegment(sketch, "E115.MirrorCS", {"start": v(97.7, 22.74) * mm, "end": v(92.62, 22.74) * mm});
            skLineSegment(sketch, "E116.MirrorCS", {"start": v(82.46, -63.62) * mm, "end": v(82.46, -68.7) * mm});
            skLineSegment(sketch, "E117.MirrorCS", {"start": v(90.08, 20.2) * mm, "end": v(90.08, 15.12) * mm});
            skLineSegment(sketch, "E118.MirrorCS", {"start": v(97.7, 58.3) * mm, "end": v(92.62, 58.3) * mm});
            skLineSegment(sketch, "E119.MirrorCS", {"start": v(82.46, 4.96) * mm, "end": v(77.38, 4.96) * mm});
            skLineSegment(sketch, "E120.MirrorCS", {"start": v(97.7, -2.66) * mm, "end": v(92.62, -2.66) * mm});
            skLineSegment(sketch, "E121.MirrorCS", {"start": v(90.08, -68.7) * mm, "end": v(85, -68.7) * mm});
            skLineSegment(sketch, "E122.MirrorCS", {"start": v(77.38, 43.06) * mm, "end": v(77.38, 37.98) * mm});
            skLineSegment(sketch, "E123.MirrorCS", {"start": v(90.08, -56) * mm, "end": v(90.08, -61.08) * mm});
            skLineSegment(sketch, "E124.MirrorCS", {"start": v(82.46, 12.58) * mm, "end": v(82.46, 7.5) * mm});
            skLineSegment(sketch, "E125.MirrorCS", {"start": v(105.32, 43.06) * mm, "end": v(100.24, 43.06) * mm});
            skLineSegment(sketch, "E126.MirrorCS", {"start": v(82.46, 53.22) * mm, "end": v(77.38, 53.22) * mm});
            skLineSegment(sketch, "E127.MirrorCS", {"start": v(97.7, -40.76) * mm, "end": v(92.62, -40.76) * mm});
            skLineSegment(sketch, "E128.MirrorCS", {"start": v(85, -33.14) * mm, "end": v(85, -38.22) * mm});
            skLineSegment(sketch, "E129.MirrorCS", {"start": v(77.38, 35.44) * mm, "end": v(77.38, 30.36) * mm});
            skLineSegment(sketch, "E130.MirrorCS", {"start": v(90.08, -56) * mm, "end": v(85, -56) * mm});
            skLineSegment(sketch, "E131.MirrorCS", {"start": v(105.32, 37.98) * mm, "end": v(100.24, 37.98) * mm});
            skLineSegment(sketch, "E132.MirrorCS", {"start": v(90.08, -33.14) * mm, "end": v(90.08, -38.22) * mm});
            skLineSegment(sketch, "E133.MirrorCS", {"start": v(97.7, -38.22) * mm, "end": v(92.62, -38.22) * mm});
            skLineSegment(sketch, "E134.MirrorCS", {"start": v(97.7, -17.9) * mm, "end": v(92.62, -17.9) * mm});
            skLineSegment(sketch, "E135.MirrorCS", {"start": v(90.08, 12.58) * mm, "end": v(90.08, 7.5) * mm});
            skLineSegment(sketch, "E136.MirrorCS", {"start": v(97.7, -2.66) * mm, "end": v(97.7, -7.74) * mm});
            skLineSegment(sketch, "E137.MirrorCS", {"start": v(82.46, -68.7) * mm, "end": v(77.38, -68.7) * mm});
            skLineSegment(sketch, "E138.MirrorCS", {"start": v(82.46, -10.28) * mm, "end": v(82.46, -15.36) * mm});
            skLineSegment(sketch, "E139.MirrorCS", {"start": v(82.46, -7.74) * mm, "end": v(77.38, -7.74) * mm});
            skLineSegment(sketch, "E140.MirrorCS", {"start": v(105.32, -0.12) * mm, "end": v(100.24, -0.12) * mm});
            skLineSegment(sketch, "E141.MirrorCS", {"start": v(97.7, -7.74) * mm, "end": v(92.62, -7.74) * mm});
            skLineSegment(sketch, "E142.MirrorCS", {"start": v(77.38, -10.28) * mm, "end": v(77.38, -15.36) * mm});
            skLineSegment(sketch, "E143.MirrorCS", {"start": v(90.08, 12.58) * mm, "end": v(85, 12.58) * mm});
            skLineSegment(sketch, "E144.MirrorCS", {"start": v(105.32, -2.66) * mm, "end": v(100.24, -2.66) * mm});
            skLineSegment(sketch, "E145.MirrorCS", {"start": v(90.08, 22.74) * mm, "end": v(85, 22.74) * mm});
            skLineSegment(sketch, "E146.MirrorCS", {"start": v(90.08, 35.44) * mm, "end": v(90.08, 30.36) * mm});
            skLineSegment(sketch, "E147.MirrorCS", {"start": v(97.7, -40.76) * mm, "end": v(97.7, -45.84) * mm});
            skLineSegment(sketch, "E148.MirrorCS", {"start": v(97.7, 20.2) * mm, "end": v(97.7, 15.12) * mm});
            skLineSegment(sketch, "E149.MirrorCS", {"start": v(100.24, 43.06) * mm, "end": v(100.24, 37.98) * mm});
            skLineSegment(sketch, "E150.MirrorCS", {"start": v(77.38, 73.54) * mm, "end": v(77.38, 68.46) * mm});
            skLineSegment(sketch, "E151.MirrorCS", {"start": v(97.7, -33.14) * mm, "end": v(97.7, -38.22) * mm});
            skLineSegment(sketch, "E152.MirrorCS", {"start": v(105.32, -17.9) * mm, "end": v(100.24, -17.9) * mm});
            skLineSegment(sketch, "E153.MirrorCS", {"start": v(105.32, -25.52) * mm, "end": v(105.32, -30.6) * mm});
            skLineSegment(sketch, "E154.MirrorCS", {"start": v(90.08, 27.82) * mm, "end": v(85, 27.82) * mm});
            skLineSegment(sketch, "E155.MirrorCS", {"start": v(90.08, -2.66) * mm, "end": v(85, -2.66) * mm});
            skLineSegment(sketch, "E156.MirrorCS", {"start": v(97.7, 43.06) * mm, "end": v(92.62, 43.06) * mm});
            skLineSegment(sketch, "E157.MirrorCS", {"start": v(82.46, 12.58) * mm, "end": v(77.38, 12.58) * mm});
            skLineSegment(sketch, "E158.MirrorCS", {"start": v(82.46, 43.06) * mm, "end": v(77.38, 43.06) * mm});
            skLineSegment(sketch, "E159.MirrorCS", {"start": v(90.08, -63.62) * mm, "end": v(85, -63.62) * mm});
            skLineSegment(sketch, "E160.MirrorCS", {"start": v(82.46, 7.5) * mm, "end": v(77.38, 7.5) * mm});
            skLineSegment(sketch, "E161.MirrorCS", {"start": v(82.46, 73.54) * mm, "end": v(77.38, 73.54) * mm});
            skLineSegment(sketch, "E162.MirrorCS", {"start": v(97.7, -10.28) * mm, "end": v(97.7, -15.36) * mm});
            skLineSegment(sketch, "E163.MirrorCS", {"start": v(90.08, 58.3) * mm, "end": v(85, 58.3) * mm});
            skLineSegment(sketch, "E164.MirrorCS", {"start": v(100.24, -25.52) * mm, "end": v(100.24, -30.6) * mm});
            skLineSegment(sketch, "E165.MirrorCS", {"start": v(105.32, -38.22) * mm, "end": v(100.24, -38.22) * mm});
            skLineSegment(sketch, "E166.MirrorCS", {"start": v(77.38, -25.52) * mm, "end": v(77.38, -30.6) * mm});
            skLineSegment(sketch, "E167.MirrorCS", {"start": v(97.7, 20.2) * mm, "end": v(92.62, 20.2) * mm});
            skLineSegment(sketch, "E168.MirrorCS", {"start": v(92.62, 27.82) * mm, "end": v(92.62, 22.74) * mm});
            skLineSegment(sketch, "E169.MirrorCS", {"start": v(77.38, -56) * mm, "end": v(77.38, -61.08) * mm});
            skLineSegment(sketch, "E170.MirrorCS", {"start": v(105.32, 20.2) * mm, "end": v(100.24, 20.2) * mm});
            skLineSegment(sketch, "E171.MirrorCS", {"start": v(97.7, 27.82) * mm, "end": v(97.7, 22.74) * mm});
            skLineSegment(sketch, "E172.MirrorCS", {"start": v(97.7, 50.68) * mm, "end": v(92.62, 50.68) * mm});
            skLineSegment(sketch, "E173.MirrorCS", {"start": v(85, -2.66) * mm, "end": v(85, -7.74) * mm});
            skLineSegment(sketch, "E174.MirrorCS", {"start": v(85, 27.82) * mm, "end": v(85, 22.74) * mm});
            skLineSegment(sketch, "E175.MirrorCS", {"start": v(90.08, 65.92) * mm, "end": v(85, 65.92) * mm});
            skLineSegment(sketch, "E176.MirrorCS", {"start": v(82.46, -17.9) * mm, "end": v(77.38, -17.9) * mm});
            skLineSegment(sketch, "E177.MirrorCS", {"start": v(77.38, -17.9) * mm, "end": v(77.38, -22.98) * mm});
            skLineSegment(sketch, "E178.MirrorCS", {"start": v(90.08, 35.44) * mm, "end": v(85, 35.44) * mm});
            skLineSegment(sketch, "E179.MirrorCS", {"start": v(82.46, 35.44) * mm, "end": v(77.38, 35.44) * mm});
            skLineSegment(sketch, "E180.MirrorCS", {"start": v(82.46, -48.38) * mm, "end": v(77.38, -48.38) * mm});
            skLineSegment(sketch, "E181.MirrorCS", {"start": v(92.62, 12.58) * mm, "end": v(92.62, 7.5) * mm});
            skLineSegment(sketch, "E182.MirrorCS", {"start": v(92.62, -17.9) * mm, "end": v(92.62, -22.98) * mm});
            skLineSegment(sketch, "E183.MirrorCS", {"start": v(82.46, 27.82) * mm, "end": v(77.38, 27.82) * mm});
            skLineSegment(sketch, "E184.MirrorCS", {"start": v(85, 58.3) * mm, "end": v(85, 53.22) * mm});
            skLineSegment(sketch, "E185.MirrorCS", {"start": v(92.62, 43.06) * mm, "end": v(92.62, 37.98) * mm});
            skLineSegment(sketch, "E186.MirrorCS", {"start": v(97.7, 15.12) * mm, "end": v(92.62, 15.12) * mm});
            skLineSegment(sketch, "E187.MirrorCS", {"start": v(97.7, -15.36) * mm, "end": v(92.62, -15.36) * mm});
            skLineSegment(sketch, "E188.MirrorCS", {"start": v(97.7, -53.46) * mm, "end": v(92.62, -53.46) * mm});
            skLineSegment(sketch, "E189.MirrorCS", {"start": v(82.46, -53.46) * mm, "end": v(77.38, -53.46) * mm});
            skLineSegment(sketch, "E190.MirrorCS", {"start": v(97.7, -45.84) * mm, "end": v(92.62, -45.84) * mm});
            skLineSegment(sketch, "E191.MirrorCS", {"start": v(90.08, -30.6) * mm, "end": v(85, -30.6) * mm});
            skLineSegment(sketch, "E192.MirrorCS", {"start": v(90.08, -25.52) * mm, "end": v(85, -25.52) * mm});
            skLineSegment(sketch, "E193.MirrorCS", {"start": v(105.32, 22.74) * mm, "end": v(100.24, 22.74) * mm});
            skLineSegment(sketch, "E194.MirrorCS", {"start": v(82.46, -22.98) * mm, "end": v(77.38, -22.98) * mm});
            skLineSegment(sketch, "E195.MirrorCS", {"start": v(100.24, -10.28) * mm, "end": v(100.24, -15.36) * mm});
            skLineSegment(sketch, "E196.MirrorCS", {"start": v(82.46, 68.46) * mm, "end": v(77.38, 68.46) * mm});
            skLineSegment(sketch, "E197.MirrorCS", {"start": v(105.32, 15.12) * mm, "end": v(100.24, 15.12) * mm});
            skLineSegment(sketch, "E198.MirrorCS", {"start": v(82.46, 58.3) * mm, "end": v(77.38, 58.3) * mm});
            skLineSegment(sketch, "E199.MirrorCS", {"start": v(92.62, 58.3) * mm, "end": v(92.62, 53.22) * mm});
            skLineSegment(sketch, "E200.MirrorCS", {"start": v(105.32, 27.82) * mm, "end": v(100.24, 27.82) * mm});
            skLineSegment(sketch, "E201.MirrorCS", {"start": v(105.32, -25.52) * mm, "end": v(100.24, -25.52) * mm});
            skLineSegment(sketch, "E202.MirrorCS", {"start": v(105.32, -15.36) * mm, "end": v(100.24, -15.36) * mm});
            skLineSegment(sketch, "E203.MirrorCS", {"start": v(82.46, 60.84) * mm, "end": v(77.38, 60.84) * mm});
            skLineSegment(sketch, "E204.MirrorCS", {"start": v(82.46, 65.92) * mm, "end": v(82.46, 60.84) * mm});
            skLineSegment(sketch, "E205.MirrorCS", {"start": v(82.46, 20.2) * mm, "end": v(77.38, 20.2) * mm});
            skLineSegment(sketch, "E206.MirrorCS", {"start": v(92.62, 35.44) * mm, "end": v(92.62, 30.36) * mm});
            skLineSegment(sketch, "E207.MirrorCS", {"start": v(105.32, -2.66) * mm, "end": v(105.32, -7.74) * mm});
            skLineSegment(sketch, "E208.MirrorCS", {"start": v(85, 4.96) * mm, "end": v(85, -0.12) * mm});
            skLineSegment(sketch, "E209.MirrorCS", {"start": v(85, -56) * mm, "end": v(85, -61.08) * mm});
            skLineSegment(sketch, "E210.MirrorCS", {"start": v(105.32, -33.14) * mm, "end": v(105.32, -38.22) * mm});
            skLineSegment(sketch, "E211.MirrorCS", {"start": v(92.62, 50.68) * mm, "end": v(92.62, 45.6) * mm});
            skLineSegment(sketch, "E212.MirrorCS", {"start": v(85, -25.52) * mm, "end": v(85, -30.6) * mm});
            skLineSegment(sketch, "E213.MirrorCS", {"start": v(92.62, -40.76) * mm, "end": v(92.62, -45.84) * mm});
            skLineSegment(sketch, "E214.MirrorCS", {"start": v(97.7, -22.98) * mm, "end": v(92.62, -22.98) * mm});
            skLineSegment(sketch, "E215.MirrorCS", {"start": v(100.24, -17.9) * mm, "end": v(100.24, -22.98) * mm});
            skLineSegment(sketch, "E216.MirrorCS", {"start": v(100.24, 12.58) * mm, "end": v(100.24, 7.5) * mm});
            skLineSegment(sketch, "E217.MirrorCS", {"start": v(105.32, 4.96) * mm, "end": v(105.32, -0.12) * mm});
            skLineSegment(sketch, "E218.MirrorCS", {"start": v(92.62, 20.2) * mm, "end": v(92.62, 15.12) * mm});
            skLineSegment(sketch, "E219.MirrorCS", {"start": v(100.24, 27.82) * mm, "end": v(100.24, 22.74) * mm});
            skLineSegment(sketch, "E220.MirrorCS", {"start": v(100.24, -2.66) * mm, "end": v(100.24, -7.74) * mm});
            skLineSegment(sketch, "E221.MirrorCS", {"start": v(92.62, 4.96) * mm, "end": v(92.62, -0.12) * mm});
            skLineSegment(sketch, "E222.MirrorCS", {"start": v(90.08, -22.98) * mm, "end": v(85, -22.98) * mm});
            skLineSegment(sketch, "E223.MirrorCS", {"start": v(90.08, 7.5) * mm, "end": v(85, 7.5) * mm});
            skLineSegment(sketch, "E224.MirrorCS", {"start": v(85, -40.76) * mm, "end": v(85, -45.84) * mm});
            skLineSegment(sketch, "E225.MirrorCS", {"start": v(85, 50.68) * mm, "end": v(85, 45.6) * mm});
            skLineSegment(sketch, "E226.MirrorCS", {"start": v(77.38, -63.62) * mm, "end": v(77.38, -68.7) * mm});
            skLineSegment(sketch, "E227.MirrorCS", {"start": v(97.7, 53.22) * mm, "end": v(92.62, 53.22) * mm});
            skLineSegment(sketch, "E228.MirrorCS", {"start": v(90.08, -53.46) * mm, "end": v(85, -53.46) * mm});
            skLineSegment(sketch, "E229.MirrorCS", {"start": v(77.38, 27.82) * mm, "end": v(77.38, 22.74) * mm});
            skLineSegment(sketch, "E230.MirrorCS", {"start": v(100.24, -33.14) * mm, "end": v(100.24, -38.22) * mm});
            skLineSegment(sketch, "E231.MirrorCS", {"start": v(85, -10.28) * mm, "end": v(85, -15.36) * mm});
            skLineSegment(sketch, "E232.MirrorCS", {"start": v(85, 20.2) * mm, "end": v(85, 15.12) * mm});
            skLineSegment(sketch, "E233.MirrorCS", {"start": v(77.38, -2.66) * mm, "end": v(77.38, -7.74) * mm});
            skLineSegment(sketch, "E234.MirrorCS", {"start": v(77.38, -33.14) * mm, "end": v(77.38, -38.22) * mm});
            skLineSegment(sketch, "E235.MirrorCS", {"start": v(90.08, 15.12) * mm, "end": v(85, 15.12) * mm});
            skLineSegment(sketch, "E236.MirrorCS", {"start": v(90.08, -45.84) * mm, "end": v(85, -45.84) * mm});
            skLineSegment(sketch, "E237.MirrorCS", {"start": v(97.7, -17.9) * mm, "end": v(97.7, -22.98) * mm});
            skLineSegment(sketch, "E238.MirrorCS", {"start": v(82.46, 45.6) * mm, "end": v(77.38, 45.6) * mm});
            skLineSegment(sketch, "E239.MirrorCS", {"start": v(92.62, -25.52) * mm, "end": v(92.62, -30.6) * mm});
            skLineSegment(sketch, "E240.MirrorCS", {"start": v(90.08, -15.36) * mm, "end": v(85, -15.36) * mm});
            skLineSegment(sketch, "E241.MirrorCS", {"start": v(90.08, 27.82) * mm, "end": v(90.08, 22.74) * mm});
            skLineSegment(sketch, "E242.MirrorCS", {"start": v(90.08, 37.98) * mm, "end": v(85, 37.98) * mm});
            skLineSegment(sketch, "E243.MirrorCS", {"start": v(82.46, -45.84) * mm, "end": v(77.38, -45.84) * mm});
            skLineSegment(sketch, "E244.MirrorCS", {"start": v(90.08, -48.38) * mm, "end": v(90.08, -53.46) * mm});
            skLineSegment(sketch, "E245.MirrorCS", {"start": v(82.46, 50.68) * mm, "end": v(82.46, 45.6) * mm});
            skLineSegment(sketch, "E246.MirrorCS", {"start": v(82.46, -71.24) * mm, "end": v(77.38, -71.24) * mm});
            skLineSegment(sketch, "E247.MirrorCS", {"start": v(82.46, 20.2) * mm, "end": v(82.46, 15.12) * mm});
            skLineSegment(sketch, "E248.MirrorCS", {"start": v(105.32, 7.5) * mm, "end": v(100.24, 7.5) * mm});
            skLineSegment(sketch, "E249.MirrorCS", {"start": v(105.32, 20.2) * mm, "end": v(105.32, 15.12) * mm});
            skLineSegment(sketch, "E250.MirrorCS", {"start": v(105.32, -10.28) * mm, "end": v(105.32, -15.36) * mm});
            skLineSegment(sketch, "E251.MirrorCS", {"start": v(105.32, 43.06) * mm, "end": v(105.32, 37.98) * mm});
            skLineSegment(sketch, "E252.MirrorCS", {"start": v(105.32, 12.58) * mm, "end": v(105.32, 7.5) * mm});
            skLineSegment(sketch, "E253.MirrorCS", {"start": v(97.7, 12.58) * mm, "end": v(97.7, 7.5) * mm});
            skLineSegment(sketch, "E254.MirrorCS", {"start": v(90.08, -63.62) * mm, "end": v(90.08, -68.7) * mm});
            skLineSegment(sketch, "E255.MirrorCS", {"start": v(82.46, -38.22) * mm, "end": v(77.38, -38.22) * mm});
            skLineSegment(sketch, "E256.MirrorCS", {"start": v(97.7, 43.06) * mm, "end": v(97.7, 37.98) * mm});
            skLineSegment(sketch, "E257.MirrorCS", {"start": v(90.08, -10.28) * mm, "end": v(85, -10.28) * mm});
            skLineSegment(sketch, "E258.MirrorCS", {"start": v(77.38, -40.76) * mm, "end": v(77.38, -45.84) * mm});
            skLineSegment(sketch, "E259.MirrorCS", {"start": v(77.38, 20.2) * mm, "end": v(77.38, 15.12) * mm});
            skLineSegment(sketch, "E260.MirrorCS", {"start": v(97.7, 4.96) * mm, "end": v(92.62, 4.96) * mm});
            skLineSegment(sketch, "E261.MirrorCS", {"start": v(90.08, 20.2) * mm, "end": v(85, 20.2) * mm});
            skLineSegment(sketch, "E262.MirrorCS", {"start": v(97.7, -25.52) * mm, "end": v(92.62, -25.52) * mm});
            skLineSegment(sketch, "E263.MirrorCS", {"start": v(90.08, -40.76) * mm, "end": v(85, -40.76) * mm});
            skLineSegment(sketch, "E264.MirrorCS", {"start": v(90.08, 50.68) * mm, "end": v(85, 50.68) * mm});
            skSolve(sketch);
        }
        {
            var Q0;
            Q0 = qSketchRegion(id + "F4", true);
            extrude(context, id + "F5", {"entities" : qUnion([Q0]), "operationType" : NewBodyOperationType.REMOVE, "oppositeDirection" : true, "depth" : 50.8 * mm});
        }
        {
            var Q0;
            Q0=makeQuery(id+"F1.opExtrude","CAP_FACE",FACE,{"disambiguationData":[OSD([sQuery(id+"F0.wireOp",EDGE,"E0")])],"isStart":false});
            var sketch = newSketch(context, id + "F6", { "sketchPlane" : qUnion([Q0])});
            skLineSegment(sketch, "E265.bottom", {"start": v(-67.42, 83.7) * mm, "end": v(-62.34, 83.7) * mm});
            skLineSegment(sketch, "E265.top", {"start": v(-67.42, 88.79) * mm, "end": v(-62.34, 88.79) * mm});
            skLineSegment(sketch, "E265.left", {"start": v(-67.42, 83.7) * mm, "end": v(-67.42, 88.79) * mm});
            skLineSegment(sketch, "E265.right", {"start": v(-62.34, 83.7) * mm, "end": v(-62.34, 88.79) * mm});
            skLineSegment(sketch, "E266.1.0.0", {"start": v(-54.72, 83.7) * mm, "end": v(-54.72, 88.79) * mm});
            skLineSegment(sketch, "E266.1.0.1", {"start": v(-59.8, 88.79) * mm, "end": v(-54.72, 88.79) * mm});
            skLineSegment(sketch, "E266.1.0.2", {"start": v(-59.8, 83.7) * mm, "end": v(-59.8, 88.79) * mm});
            skLineSegment(sketch, "E266.1.0.3", {"start": v(-59.8, 83.7) * mm, "end": v(-54.72, 83.7) * mm});
            skLineSegment(sketch, "E266.1.1.0", {"start": v(-54.72, 91.33) * mm, "end": v(-54.72, 96.4) * mm});
            skLineSegment(sketch, "E266.1.1.1", {"start": v(-59.8, 96.4) * mm, "end": v(-54.72, 96.4) * mm});
            skLineSegment(sketch, "E266.1.1.2", {"start": v(-59.8, 91.33) * mm, "end": v(-59.8, 96.4) * mm});
            skLineSegment(sketch, "E266.1.1.3", {"start": v(-59.8, 91.33) * mm, "end": v(-54.72, 91.33) * mm});
            skLineSegment(sketch, "E266.2.0.0", {"start": v(-47.1, 83.7) * mm, "end": v(-47.1, 88.79) * mm});
            skLineSegment(sketch, "E266.2.0.1", {"start": v(-52.18, 88.79) * mm, "end": v(-47.1, 88.79) * mm});
            skLineSegment(sketch, "E266.2.0.2", {"start": v(-52.18, 83.7) * mm, "end": v(-52.18, 88.79) * mm});
            skLineSegment(sketch, "E266.2.0.3", {"start": v(-52.18, 83.7) * mm, "end": v(-47.1, 83.7) * mm});
            skLineSegment(sketch, "E266.2.1.0", {"start": v(-47.1, 91.33) * mm, "end": v(-47.1, 96.4) * mm});
            skLineSegment(sketch, "E266.2.1.1", {"start": v(-52.18, 96.4) * mm, "end": v(-47.1, 96.4) * mm});
            skLineSegment(sketch, "E266.2.1.2", {"start": v(-52.18, 91.33) * mm, "end": v(-52.18, 96.4) * mm});
            skLineSegment(sketch, "E266.2.1.3", {"start": v(-52.18, 91.33) * mm, "end": v(-47.1, 91.33) * mm});
            skLineSegment(sketch, "E266.3.0.0", {"start": v(-39.48, 83.7) * mm, "end": v(-39.48, 88.79) * mm});
            skLineSegment(sketch, "E266.3.0.1", {"start": v(-44.56, 88.79) * mm, "end": v(-39.48, 88.79) * mm});
            skLineSegment(sketch, "E266.3.0.2", {"start": v(-44.56, 83.7) * mm, "end": v(-44.56, 88.79) * mm});
            skLineSegment(sketch, "E266.3.0.3", {"start": v(-44.56, 83.7) * mm, "end": v(-39.48, 83.7) * mm});
            skLineSegment(sketch, "E266.3.1.0", {"start": v(-39.48, 91.33) * mm, "end": v(-39.48, 96.4) * mm});
            skLineSegment(sketch, "E266.3.1.1", {"start": v(-44.56, 96.4) * mm, "end": v(-39.48, 96.4) * mm});
            skLineSegment(sketch, "E266.3.1.2", {"start": v(-44.56, 91.33) * mm, "end": v(-44.56, 96.4) * mm});
            skLineSegment(sketch, "E266.3.1.3", {"start": v(-44.56, 91.33) * mm, "end": v(-39.48, 91.33) * mm});
            skLineSegment(sketch, "E266.3.2.0", {"start": v(-39.48, 98.95) * mm, "end": v(-39.48, 104.03) * mm});
            skLineSegment(sketch, "E266.3.2.1", {"start": v(-44.56, 104.03) * mm, "end": v(-39.48, 104.03) * mm});
            skLineSegment(sketch, "E266.3.2.2", {"start": v(-44.56, 98.95) * mm, "end": v(-44.56, 104.03) * mm});
            skLineSegment(sketch, "E266.3.2.3", {"start": v(-44.56, 98.95) * mm, "end": v(-39.48, 98.95) * mm});
            skLineSegment(sketch, "E266.4.0.0", {"start": v(-31.86, 83.7) * mm, "end": v(-31.86, 88.79) * mm});
            skLineSegment(sketch, "E266.4.0.1", {"start": v(-36.94, 88.79) * mm, "end": v(-31.86, 88.79) * mm});
            skLineSegment(sketch, "E266.4.0.2", {"start": v(-36.94, 83.7) * mm, "end": v(-36.94, 88.79) * mm});
            skLineSegment(sketch, "E266.4.0.3", {"start": v(-36.94, 83.7) * mm, "end": v(-31.86, 83.7) * mm});
            skLineSegment(sketch, "E266.4.1.0", {"start": v(-31.86, 91.33) * mm, "end": v(-31.86, 96.4) * mm});
            skLineSegment(sketch, "E266.4.1.1", {"start": v(-36.94, 96.4) * mm, "end": v(-31.86, 96.4) * mm});
            skLineSegment(sketch, "E266.4.1.2", {"start": v(-36.94, 91.33) * mm, "end": v(-36.94, 96.4) * mm});
            skLineSegment(sketch, "E266.4.1.3", {"start": v(-36.94, 91.33) * mm, "end": v(-31.86, 91.33) * mm});
            skLineSegment(sketch, "E266.4.2.0", {"start": v(-31.86, 98.95) * mm, "end": v(-31.86, 104.03) * mm});
            skLineSegment(sketch, "E266.4.2.1", {"start": v(-36.94, 104.03) * mm, "end": v(-31.86, 104.03) * mm});
            skLineSegment(sketch, "E266.4.2.2", {"start": v(-36.94, 98.95) * mm, "end": v(-36.94, 104.03) * mm});
            skLineSegment(sketch, "E266.4.2.3", {"start": v(-36.94, 98.95) * mm, "end": v(-31.86, 98.95) * mm});
            skLineSegment(sketch, "E266.5.0.0", {"start": v(-24.24, 83.7) * mm, "end": v(-24.24, 88.79) * mm});
            skLineSegment(sketch, "E266.5.0.1", {"start": v(-29.32, 88.79) * mm, "end": v(-24.24, 88.79) * mm});
            skLineSegment(sketch, "E266.5.0.2", {"start": v(-29.32, 83.7) * mm, "end": v(-29.32, 88.79) * mm});
            skLineSegment(sketch, "E266.5.0.3", {"start": v(-29.32, 83.7) * mm, "end": v(-24.24, 83.7) * mm});
            skLineSegment(sketch, "E266.5.1.0", {"start": v(-24.24, 91.33) * mm, "end": v(-24.24, 96.4) * mm});
            skLineSegment(sketch, "E266.5.1.1", {"start": v(-29.32, 96.4) * mm, "end": v(-24.24, 96.4) * mm});
            skLineSegment(sketch, "E266.5.1.2", {"start": v(-29.32, 91.33) * mm, "end": v(-29.32, 96.4) * mm});
            skLineSegment(sketch, "E266.5.1.3", {"start": v(-29.32, 91.33) * mm, "end": v(-24.24, 91.33) * mm});
            skLineSegment(sketch, "E266.5.2.0", {"start": v(-24.24, 98.95) * mm, "end": v(-24.24, 104.03) * mm});
            skLineSegment(sketch, "E266.5.2.1", {"start": v(-29.32, 104.03) * mm, "end": v(-24.24, 104.03) * mm});
            skLineSegment(sketch, "E266.5.2.2", {"start": v(-29.32, 98.95) * mm, "end": v(-29.32, 104.03) * mm});
            skLineSegment(sketch, "E266.5.2.3", {"start": v(-29.32, 98.95) * mm, "end": v(-24.24, 98.95) * mm});
            skLineSegment(sketch, "E266.6.0.0", {"start": v(-16.62, 83.7) * mm, "end": v(-16.62, 88.79) * mm});
            skLineSegment(sketch, "E266.6.0.1", {"start": v(-21.7, 88.79) * mm, "end": v(-16.62, 88.79) * mm});
            skLineSegment(sketch, "E266.6.0.2", {"start": v(-21.7, 83.7) * mm, "end": v(-21.7, 88.79) * mm});
            skLineSegment(sketch, "E266.6.0.3", {"start": v(-21.7, 83.7) * mm, "end": v(-16.62, 83.7) * mm});
            skLineSegment(sketch, "E266.6.1.0", {"start": v(-16.62, 91.33) * mm, "end": v(-16.62, 96.4) * mm});
            skLineSegment(sketch, "E266.6.1.1", {"start": v(-21.7, 96.4) * mm, "end": v(-16.62, 96.4) * mm});
            skLineSegment(sketch, "E266.6.1.2", {"start": v(-21.7, 91.33) * mm, "end": v(-21.7, 96.4) * mm});
            skLineSegment(sketch, "E266.6.1.3", {"start": v(-21.7, 91.33) * mm, "end": v(-16.62, 91.33) * mm});
            skLineSegment(sketch, "E266.6.2.0", {"start": v(-16.62, 98.95) * mm, "end": v(-16.62, 104.03) * mm});
            skLineSegment(sketch, "E266.6.2.1", {"start": v(-21.7, 104.03) * mm, "end": v(-16.62, 104.03) * mm});
            skLineSegment(sketch, "E266.6.2.2", {"start": v(-21.7, 98.95) * mm, "end": v(-21.7, 104.03) * mm});
            skLineSegment(sketch, "E266.6.2.3", {"start": v(-21.7, 98.95) * mm, "end": v(-16.62, 98.95) * mm});
            skLineSegment(sketch, "E266.7.0.0", {"start": v(-9, 83.7) * mm, "end": v(-9, 88.79) * mm});
            skLineSegment(sketch, "E266.7.0.1", {"start": v(-14.08, 88.79) * mm, "end": v(-9, 88.79) * mm});
            skLineSegment(sketch, "E266.7.0.2", {"start": v(-14.08, 83.7) * mm, "end": v(-14.08, 88.79) * mm});
            skLineSegment(sketch, "E266.7.0.3", {"start": v(-14.08, 83.7) * mm, "end": v(-9, 83.7) * mm});
            skLineSegment(sketch, "E266.7.1.0", {"start": v(-9, 91.33) * mm, "end": v(-9, 96.4) * mm});
            skLineSegment(sketch, "E266.7.1.1", {"start": v(-14.08, 96.4) * mm, "end": v(-9, 96.4) * mm});
            skLineSegment(sketch, "E266.7.1.2", {"start": v(-14.08, 91.33) * mm, "end": v(-14.08, 96.4) * mm});
            skLineSegment(sketch, "E266.7.1.3", {"start": v(-14.08, 91.33) * mm, "end": v(-9, 91.33) * mm});
            skLineSegment(sketch, "E266.7.2.0", {"start": v(-9, 98.95) * mm, "end": v(-9, 104.03) * mm});
            skLineSegment(sketch, "E266.7.2.1", {"start": v(-14.08, 104.03) * mm, "end": v(-9, 104.03) * mm});
            skLineSegment(sketch, "E266.7.2.2", {"start": v(-14.08, 98.95) * mm, "end": v(-14.08, 104.03) * mm});
            skLineSegment(sketch, "E266.7.2.3", {"start": v(-14.08, 98.95) * mm, "end": v(-9, 98.95) * mm});
            skLineSegment(sketch, "E266.8.0.0", {"start": v(-1.38, 83.7) * mm, "end": v(-1.38, 88.79) * mm});
            skLineSegment(sketch, "E266.8.0.1", {"start": v(-6.46, 88.79) * mm, "end": v(-1.38, 88.79) * mm});
            skLineSegment(sketch, "E266.8.0.2", {"start": v(-6.46, 83.7) * mm, "end": v(-6.46, 88.79) * mm});
            skLineSegment(sketch, "E266.8.0.3", {"start": v(-6.46, 83.7) * mm, "end": v(-1.38, 83.7) * mm});
            skLineSegment(sketch, "E266.8.1.0", {"start": v(-1.38, 91.33) * mm, "end": v(-1.38, 96.4) * mm});
            skLineSegment(sketch, "E266.8.1.1", {"start": v(-6.46, 96.4) * mm, "end": v(-1.38, 96.4) * mm});
            skLineSegment(sketch, "E266.8.1.2", {"start": v(-6.46, 91.33) * mm, "end": v(-6.46, 96.4) * mm});
            skLineSegment(sketch, "E266.8.1.3", {"start": v(-6.46, 91.33) * mm, "end": v(-1.38, 91.33) * mm});
            skLineSegment(sketch, "E266.8.2.0", {"start": v(-1.38, 98.95) * mm, "end": v(-1.38, 104.03) * mm});
            skLineSegment(sketch, "E266.8.2.1", {"start": v(-6.46, 104.03) * mm, "end": v(-1.38, 104.03) * mm});
            skLineSegment(sketch, "E266.8.2.2", {"start": v(-6.46, 98.95) * mm, "end": v(-6.46, 104.03) * mm});
            skLineSegment(sketch, "E266.8.2.3", {"start": v(-6.46, 98.95) * mm, "end": v(-1.38, 98.95) * mm});
            skLineSegment(sketch, "E266.9.0.0", {"start": v(6.24, 83.7) * mm, "end": v(6.24, 88.79) * mm});
            skLineSegment(sketch, "E266.9.0.1", {"start": v(1.16, 88.79) * mm, "end": v(6.24, 88.79) * mm});
            skLineSegment(sketch, "E266.9.0.2", {"start": v(1.16, 83.7) * mm, "end": v(1.16, 88.79) * mm});
            skLineSegment(sketch, "E266.9.0.3", {"start": v(1.16, 83.7) * mm, "end": v(6.24, 83.7) * mm});
            skLineSegment(sketch, "E266.9.1.0", {"start": v(6.24, 91.33) * mm, "end": v(6.24, 96.4) * mm});
            skLineSegment(sketch, "E266.9.1.1", {"start": v(1.16, 96.4) * mm, "end": v(6.24, 96.4) * mm});
            skLineSegment(sketch, "E266.9.1.2", {"start": v(1.16, 91.33) * mm, "end": v(1.16, 96.4) * mm});
            skLineSegment(sketch, "E266.9.1.3", {"start": v(1.16, 91.33) * mm, "end": v(6.24, 91.33) * mm});
            skLineSegment(sketch, "E266.9.2.0", {"start": v(6.24, 98.95) * mm, "end": v(6.24, 104.03) * mm});
            skLineSegment(sketch, "E266.9.2.1", {"start": v(1.16, 104.03) * mm, "end": v(6.24, 104.03) * mm});
            skLineSegment(sketch, "E266.9.2.2", {"start": v(1.16, 98.95) * mm, "end": v(1.16, 104.03) * mm});
            skLineSegment(sketch, "E266.9.2.3", {"start": v(1.16, 98.95) * mm, "end": v(6.24, 98.95) * mm});
            skLineSegment(sketch, "E266.10.0.0", {"start": v(13.86, 83.7) * mm, "end": v(13.86, 88.79) * mm});
            skLineSegment(sketch, "E266.10.0.1", {"start": v(8.78, 88.79) * mm, "end": v(13.86, 88.79) * mm});
            skLineSegment(sketch, "E266.10.0.2", {"start": v(8.78, 83.7) * mm, "end": v(8.78, 88.79) * mm});
            skLineSegment(sketch, "E266.10.0.3", {"start": v(8.78, 83.7) * mm, "end": v(13.86, 83.7) * mm});
            skLineSegment(sketch, "E266.10.1.0", {"start": v(13.86, 91.33) * mm, "end": v(13.86, 96.4) * mm});
            skLineSegment(sketch, "E266.10.1.1", {"start": v(8.78, 96.4) * mm, "end": v(13.86, 96.4) * mm});
            skLineSegment(sketch, "E266.10.1.2", {"start": v(8.78, 91.33) * mm, "end": v(8.78, 96.4) * mm});
            skLineSegment(sketch, "E266.10.1.3", {"start": v(8.78, 91.33) * mm, "end": v(13.86, 91.33) * mm});
            skLineSegment(sketch, "E266.10.2.0", {"start": v(13.86, 98.95) * mm, "end": v(13.86, 104.03) * mm});
            skLineSegment(sketch, "E266.10.2.1", {"start": v(8.78, 104.03) * mm, "end": v(13.86, 104.03) * mm});
            skLineSegment(sketch, "E266.10.2.2", {"start": v(8.78, 98.95) * mm, "end": v(8.78, 104.03) * mm});
            skLineSegment(sketch, "E266.10.2.3", {"start": v(8.78, 98.95) * mm, "end": v(13.86, 98.95) * mm});
            skLineSegment(sketch, "E266.11.0.0", {"start": v(21.48, 83.7) * mm, "end": v(21.48, 88.79) * mm});
            skLineSegment(sketch, "E266.11.0.1", {"start": v(16.4, 88.79) * mm, "end": v(21.48, 88.79) * mm});
            skLineSegment(sketch, "E266.11.0.2", {"start": v(16.4, 83.7) * mm, "end": v(16.4, 88.79) * mm});
            skLineSegment(sketch, "E266.11.0.3", {"start": v(16.4, 83.7) * mm, "end": v(21.48, 83.7) * mm});
            skLineSegment(sketch, "E266.11.1.0", {"start": v(21.48, 91.33) * mm, "end": v(21.48, 96.4) * mm});
            skLineSegment(sketch, "E266.11.1.1", {"start": v(16.4, 96.4) * mm, "end": v(21.48, 96.4) * mm});
            skLineSegment(sketch, "E266.11.1.2", {"start": v(16.4, 91.33) * mm, "end": v(16.4, 96.4) * mm});
            skLineSegment(sketch, "E266.11.1.3", {"start": v(16.4, 91.33) * mm, "end": v(21.48, 91.33) * mm});
            skLineSegment(sketch, "E266.11.2.0", {"start": v(21.48, 98.95) * mm, "end": v(21.48, 104.03) * mm});
            skLineSegment(sketch, "E266.11.2.1", {"start": v(16.4, 104.03) * mm, "end": v(21.48, 104.03) * mm});
            skLineSegment(sketch, "E266.11.2.2", {"start": v(16.4, 98.95) * mm, "end": v(16.4, 104.03) * mm});
            skLineSegment(sketch, "E266.11.2.3", {"start": v(16.4, 98.95) * mm, "end": v(21.48, 98.95) * mm});
            skLineSegment(sketch, "E266.12.0.0", {"start": v(29.1, 83.7) * mm, "end": v(29.1, 88.79) * mm});
            skLineSegment(sketch, "E266.12.0.1", {"start": v(24.02, 88.79) * mm, "end": v(29.1, 88.79) * mm});
            skLineSegment(sketch, "E266.12.0.2", {"start": v(24.02, 83.7) * mm, "end": v(24.02, 88.79) * mm});
            skLineSegment(sketch, "E266.12.0.3", {"start": v(24.02, 83.7) * mm, "end": v(29.1, 83.7) * mm});
            skLineSegment(sketch, "E266.12.1.0", {"start": v(29.1, 91.33) * mm, "end": v(29.1, 96.4) * mm});
            skLineSegment(sketch, "E266.12.1.1", {"start": v(24.02, 96.4) * mm, "end": v(29.1, 96.4) * mm});
            skLineSegment(sketch, "E266.12.1.2", {"start": v(24.02, 91.33) * mm, "end": v(24.02, 96.4) * mm});
            skLineSegment(sketch, "E266.12.1.3", {"start": v(24.02, 91.33) * mm, "end": v(29.1, 91.33) * mm});
            skLineSegment(sketch, "E266.12.2.0", {"start": v(29.1, 98.95) * mm, "end": v(29.1, 104.03) * mm});
            skLineSegment(sketch, "E266.12.2.1", {"start": v(24.02, 104.03) * mm, "end": v(29.1, 104.03) * mm});
            skLineSegment(sketch, "E266.12.2.2", {"start": v(24.02, 98.95) * mm, "end": v(24.02, 104.03) * mm});
            skLineSegment(sketch, "E266.12.2.3", {"start": v(24.02, 98.95) * mm, "end": v(29.1, 98.95) * mm});
            skLineSegment(sketch, "E266.13.0.0", {"start": v(36.72, 83.7) * mm, "end": v(36.72, 88.79) * mm});
            skLineSegment(sketch, "E266.13.0.1", {"start": v(31.64, 88.79) * mm, "end": v(36.72, 88.79) * mm});
            skLineSegment(sketch, "E266.13.0.2", {"start": v(31.64, 83.7) * mm, "end": v(31.64, 88.79) * mm});
            skLineSegment(sketch, "E266.13.0.3", {"start": v(31.64, 83.7) * mm, "end": v(36.72, 83.7) * mm});
            skLineSegment(sketch, "E266.13.1.0", {"start": v(36.72, 91.33) * mm, "end": v(36.72, 96.4) * mm});
            skLineSegment(sketch, "E266.13.1.1", {"start": v(31.64, 96.4) * mm, "end": v(36.72, 96.4) * mm});
            skLineSegment(sketch, "E266.13.1.2", {"start": v(31.64, 91.33) * mm, "end": v(31.64, 96.4) * mm});
            skLineSegment(sketch, "E266.13.1.3", {"start": v(31.64, 91.33) * mm, "end": v(36.72, 91.33) * mm});
            skLineSegment(sketch, "E266.13.2.0", {"start": v(36.72, 98.95) * mm, "end": v(36.72, 104.03) * mm});
            skLineSegment(sketch, "E266.13.2.1", {"start": v(31.64, 104.03) * mm, "end": v(36.72, 104.03) * mm});
            skLineSegment(sketch, "E266.13.2.2", {"start": v(31.64, 98.95) * mm, "end": v(31.64, 104.03) * mm});
            skLineSegment(sketch, "E266.13.2.3", {"start": v(31.64, 98.95) * mm, "end": v(36.72, 98.95) * mm});
            skLineSegment(sketch, "E266.14.0.0", {"start": v(44.34, 83.7) * mm, "end": v(44.34, 88.79) * mm});
            skLineSegment(sketch, "E266.14.0.1", {"start": v(39.26, 88.79) * mm, "end": v(44.34, 88.79) * mm});
            skLineSegment(sketch, "E266.14.0.2", {"start": v(39.26, 83.7) * mm, "end": v(39.26, 88.79) * mm});
            skLineSegment(sketch, "E266.14.0.3", {"start": v(39.26, 83.7) * mm, "end": v(44.34, 83.7) * mm});
            skLineSegment(sketch, "E266.14.1.0", {"start": v(44.34, 91.33) * mm, "end": v(44.34, 96.4) * mm});
            skLineSegment(sketch, "E266.14.1.1", {"start": v(39.26, 96.4) * mm, "end": v(44.34, 96.4) * mm});
            skLineSegment(sketch, "E266.14.1.2", {"start": v(39.26, 91.33) * mm, "end": v(39.26, 96.4) * mm});
            skLineSegment(sketch, "E266.14.1.3", {"start": v(39.26, 91.33) * mm, "end": v(44.34, 91.33) * mm});
            skLineSegment(sketch, "E266.14.2.0", {"start": v(44.34, 98.95) * mm, "end": v(44.34, 104.03) * mm});
            skLineSegment(sketch, "E266.14.2.1", {"start": v(39.26, 104.03) * mm, "end": v(44.34, 104.03) * mm});
            skLineSegment(sketch, "E266.14.2.2", {"start": v(39.26, 98.95) * mm, "end": v(39.26, 104.03) * mm});
            skLineSegment(sketch, "E266.14.2.3", {"start": v(39.26, 98.95) * mm, "end": v(44.34, 98.95) * mm});
            skLineSegment(sketch, "E266.15.0.0", {"start": v(51.96, 83.7) * mm, "end": v(51.96, 88.79) * mm});
            skLineSegment(sketch, "E266.15.0.1", {"start": v(46.88, 88.79) * mm, "end": v(51.96, 88.79) * mm});
            skLineSegment(sketch, "E266.15.0.2", {"start": v(46.88, 83.7) * mm, "end": v(46.88, 88.79) * mm});
            skLineSegment(sketch, "E266.15.0.3", {"start": v(46.88, 83.7) * mm, "end": v(51.96, 83.7) * mm});
            skLineSegment(sketch, "E266.15.1.0", {"start": v(51.96, 91.33) * mm, "end": v(51.96, 96.4) * mm});
            skLineSegment(sketch, "E266.15.1.1", {"start": v(46.88, 96.4) * mm, "end": v(51.96, 96.4) * mm});
            skLineSegment(sketch, "E266.15.1.2", {"start": v(46.88, 91.33) * mm, "end": v(46.88, 96.4) * mm});
            skLineSegment(sketch, "E266.15.1.3", {"start": v(46.88, 91.33) * mm, "end": v(51.96, 91.33) * mm});
            skLineSegment(sketch, "E266.16.0.0", {"start": v(59.58, 83.7) * mm, "end": v(59.58, 88.79) * mm});
            skLineSegment(sketch, "E266.16.0.1", {"start": v(54.5, 88.79) * mm, "end": v(59.58, 88.79) * mm});
            skLineSegment(sketch, "E266.16.0.2", {"start": v(54.5, 83.7) * mm, "end": v(54.5, 88.79) * mm});
            skLineSegment(sketch, "E266.16.0.3", {"start": v(54.5, 83.7) * mm, "end": v(59.58, 83.7) * mm});
            skLineSegment(sketch, "E266.16.1.0", {"start": v(59.58, 91.33) * mm, "end": v(59.58, 96.4) * mm});
            skLineSegment(sketch, "E266.16.1.1", {"start": v(54.5, 96.4) * mm, "end": v(59.58, 96.4) * mm});
            skLineSegment(sketch, "E266.16.1.2", {"start": v(54.5, 91.33) * mm, "end": v(54.5, 96.4) * mm});
            skLineSegment(sketch, "E266.16.1.3", {"start": v(54.5, 91.33) * mm, "end": v(59.58, 91.33) * mm});
            skLineSegment(sketch, "E266.17.0.0", {"start": v(67.2, 83.7) * mm, "end": v(67.2, 88.79) * mm});
            skLineSegment(sketch, "E266.17.0.1", {"start": v(62.12, 88.79) * mm, "end": v(67.2, 88.79) * mm});
            skLineSegment(sketch, "E266.17.0.2", {"start": v(62.12, 83.7) * mm, "end": v(62.12, 88.79) * mm});
            skLineSegment(sketch, "E266.17.0.3", {"start": v(62.12, 83.7) * mm, "end": v(67.2, 83.7) * mm});
            skLineSegment(sketch, "E266.direction1", {"start": v(-62.34, 83.7) * mm, "end": v(-54.72, 83.7) * mm, "construction": true});
            skLineSegment(sketch, "E266.direction2", {"start": v(-62.34, 83.7) * mm, "end": v(-62.34, 91.33) * mm, "construction": true});
            skLineSegment(sketch, "E267.bottom", {"start": v(-67.4, -86.47) * mm, "end": v(-62.32, -86.47) * mm});
            skLineSegment(sketch, "E267.top", {"start": v(-67.4, -91.55) * mm, "end": v(-62.32, -91.55) * mm});
            skLineSegment(sketch, "E267.left", {"start": v(-67.4, -86.47) * mm, "end": v(-67.4, -91.55) * mm});
            skLineSegment(sketch, "E267.right", {"start": v(-62.32, -86.47) * mm, "end": v(-62.32, -91.55) * mm});
            skLineSegment(sketch, "E268.1.0.0", {"start": v(-59.78, -91.55) * mm, "end": v(-54.7, -91.55) * mm});
            skLineSegment(sketch, "E268.1.0.1", {"start": v(-54.7, -86.47) * mm, "end": v(-54.7, -91.55) * mm});
            skLineSegment(sketch, "E268.1.0.2", {"start": v(-59.78, -86.47) * mm, "end": v(-59.78, -91.55) * mm});
            skLineSegment(sketch, "E268.1.0.3", {"start": v(-59.78, -86.47) * mm, "end": v(-54.7, -86.47) * mm});
            skLineSegment(sketch, "E268.2.0.0", {"start": v(-52.16, -91.55) * mm, "end": v(-47.08, -91.55) * mm});
            skLineSegment(sketch, "E268.2.0.1", {"start": v(-47.08, -86.47) * mm, "end": v(-47.08, -91.55) * mm});
            skLineSegment(sketch, "E268.2.0.2", {"start": v(-52.16, -86.47) * mm, "end": v(-52.16, -91.55) * mm});
            skLineSegment(sketch, "E268.2.0.3", {"start": v(-52.16, -86.47) * mm, "end": v(-47.08, -86.47) * mm});
            skLineSegment(sketch, "E268.2.1.0", {"start": v(-52.16, -99.17) * mm, "end": v(-47.08, -99.17) * mm});
            skLineSegment(sketch, "E268.2.1.1", {"start": v(-47.08, -94.1) * mm, "end": v(-47.08, -99.17) * mm});
            skLineSegment(sketch, "E268.2.1.2", {"start": v(-52.16, -94.1) * mm, "end": v(-52.16, -99.17) * mm});
            skLineSegment(sketch, "E268.2.1.3", {"start": v(-52.16, -94.1) * mm, "end": v(-47.08, -94.1) * mm});
            skLineSegment(sketch, "E268.3.0.0", {"start": v(-44.54, -91.55) * mm, "end": v(-39.46, -91.55) * mm});
            skLineSegment(sketch, "E268.3.0.1", {"start": v(-39.46, -86.47) * mm, "end": v(-39.46, -91.55) * mm});
            skLineSegment(sketch, "E268.3.0.2", {"start": v(-44.54, -86.47) * mm, "end": v(-44.54, -91.55) * mm});
            skLineSegment(sketch, "E268.3.0.3", {"start": v(-44.54, -86.47) * mm, "end": v(-39.46, -86.47) * mm});
            skLineSegment(sketch, "E268.3.1.0", {"start": v(-44.54, -99.17) * mm, "end": v(-39.46, -99.17) * mm});
            skLineSegment(sketch, "E268.3.1.1", {"start": v(-39.46, -94.1) * mm, "end": v(-39.46, -99.17) * mm});
            skLineSegment(sketch, "E268.3.1.2", {"start": v(-44.54, -94.1) * mm, "end": v(-44.54, -99.17) * mm});
            skLineSegment(sketch, "E268.3.1.3", {"start": v(-44.54, -94.1) * mm, "end": v(-39.46, -94.1) * mm});
            skLineSegment(sketch, "E268.4.0.0", {"start": v(-36.92, -91.55) * mm, "end": v(-31.84, -91.55) * mm});
            skLineSegment(sketch, "E268.4.0.1", {"start": v(-31.84, -86.47) * mm, "end": v(-31.84, -91.55) * mm});
            skLineSegment(sketch, "E268.4.0.2", {"start": v(-36.92, -86.47) * mm, "end": v(-36.92, -91.55) * mm});
            skLineSegment(sketch, "E268.4.0.3", {"start": v(-36.92, -86.47) * mm, "end": v(-31.84, -86.47) * mm});
            skLineSegment(sketch, "E268.4.1.0", {"start": v(-36.92, -99.17) * mm, "end": v(-31.84, -99.17) * mm});
            skLineSegment(sketch, "E268.4.1.1", {"start": v(-31.84, -94.1) * mm, "end": v(-31.84, -99.17) * mm});
            skLineSegment(sketch, "E268.4.1.2", {"start": v(-36.92, -94.1) * mm, "end": v(-36.92, -99.17) * mm});
            skLineSegment(sketch, "E268.4.1.3", {"start": v(-36.92, -94.1) * mm, "end": v(-31.84, -94.1) * mm});
            skLineSegment(sketch, "E268.4.2.0", {"start": v(-36.92, -106.8) * mm, "end": v(-31.84, -106.8) * mm});
            skLineSegment(sketch, "E268.4.2.1", {"start": v(-31.84, -101.71) * mm, "end": v(-31.84, -106.8) * mm});
            skLineSegment(sketch, "E268.4.2.2", {"start": v(-36.92, -101.71) * mm, "end": v(-36.92, -106.8) * mm});
            skLineSegment(sketch, "E268.4.2.3", {"start": v(-36.92, -101.71) * mm, "end": v(-31.84, -101.71) * mm});
            skLineSegment(sketch, "E268.5.0.0", {"start": v(-29.3, -91.55) * mm, "end": v(-24.22, -91.55) * mm});
            skLineSegment(sketch, "E268.5.0.1", {"start": v(-24.22, -86.47) * mm, "end": v(-24.22, -91.55) * mm});
            skLineSegment(sketch, "E268.5.0.2", {"start": v(-29.3, -86.47) * mm, "end": v(-29.3, -91.55) * mm});
            skLineSegment(sketch, "E268.5.0.3", {"start": v(-29.3, -86.47) * mm, "end": v(-24.22, -86.47) * mm});
            skLineSegment(sketch, "E268.5.1.0", {"start": v(-29.3, -99.17) * mm, "end": v(-24.22, -99.17) * mm});
            skLineSegment(sketch, "E268.5.1.1", {"start": v(-24.22, -94.1) * mm, "end": v(-24.22, -99.17) * mm});
            skLineSegment(sketch, "E268.5.1.2", {"start": v(-29.3, -94.1) * mm, "end": v(-29.3, -99.17) * mm});
            skLineSegment(sketch, "E268.5.1.3", {"start": v(-29.3, -94.1) * mm, "end": v(-24.22, -94.1) * mm});
            skLineSegment(sketch, "E268.5.2.0", {"start": v(-29.3, -106.8) * mm, "end": v(-24.22, -106.8) * mm});
            skLineSegment(sketch, "E268.5.2.1", {"start": v(-24.22, -101.71) * mm, "end": v(-24.22, -106.8) * mm});
            skLineSegment(sketch, "E268.5.2.2", {"start": v(-29.3, -101.71) * mm, "end": v(-29.3, -106.8) * mm});
            skLineSegment(sketch, "E268.5.2.3", {"start": v(-29.3, -101.71) * mm, "end": v(-24.22, -101.71) * mm});
            skLineSegment(sketch, "E268.6.0.0", {"start": v(-21.68, -91.55) * mm, "end": v(-16.6, -91.55) * mm});
            skLineSegment(sketch, "E268.6.0.1", {"start": v(-16.6, -86.47) * mm, "end": v(-16.6, -91.55) * mm});
            skLineSegment(sketch, "E268.6.0.2", {"start": v(-21.68, -86.47) * mm, "end": v(-21.68, -91.55) * mm});
            skLineSegment(sketch, "E268.6.0.3", {"start": v(-21.68, -86.47) * mm, "end": v(-16.6, -86.47) * mm});
            skLineSegment(sketch, "E268.6.1.0", {"start": v(-21.68, -99.17) * mm, "end": v(-16.6, -99.17) * mm});
            skLineSegment(sketch, "E268.6.1.1", {"start": v(-16.6, -94.1) * mm, "end": v(-16.6, -99.17) * mm});
            skLineSegment(sketch, "E268.6.1.2", {"start": v(-21.68, -94.1) * mm, "end": v(-21.68, -99.17) * mm});
            skLineSegment(sketch, "E268.6.1.3", {"start": v(-21.68, -94.1) * mm, "end": v(-16.6, -94.1) * mm});
            skLineSegment(sketch, "E268.6.2.0", {"start": v(-21.68, -106.8) * mm, "end": v(-16.6, -106.8) * mm});
            skLineSegment(sketch, "E268.6.2.1", {"start": v(-16.6, -101.71) * mm, "end": v(-16.6, -106.8) * mm});
            skLineSegment(sketch, "E268.6.2.2", {"start": v(-21.68, -101.71) * mm, "end": v(-21.68, -106.8) * mm});
            skLineSegment(sketch, "E268.6.2.3", {"start": v(-21.68, -101.71) * mm, "end": v(-16.6, -101.71) * mm});
            skLineSegment(sketch, "E268.7.0.0", {"start": v(-14.06, -91.55) * mm, "end": v(-8.98, -91.55) * mm});
            skLineSegment(sketch, "E268.7.0.1", {"start": v(-8.98, -86.47) * mm, "end": v(-8.98, -91.55) * mm});
            skLineSegment(sketch, "E268.7.0.2", {"start": v(-14.06, -86.47) * mm, "end": v(-14.06, -91.55) * mm});
            skLineSegment(sketch, "E268.7.0.3", {"start": v(-14.06, -86.47) * mm, "end": v(-8.98, -86.47) * mm});
            skLineSegment(sketch, "E268.7.1.0", {"start": v(-14.06, -99.17) * mm, "end": v(-8.98, -99.17) * mm});
            skLineSegment(sketch, "E268.7.1.1", {"start": v(-8.98, -94.1) * mm, "end": v(-8.98, -99.17) * mm});
            skLineSegment(sketch, "E268.7.1.2", {"start": v(-14.06, -94.1) * mm, "end": v(-14.06, -99.17) * mm});
            skLineSegment(sketch, "E268.7.1.3", {"start": v(-14.06, -94.1) * mm, "end": v(-8.98, -94.1) * mm});
            skLineSegment(sketch, "E268.7.2.0", {"start": v(-14.06, -106.8) * mm, "end": v(-8.98, -106.8) * mm});
            skLineSegment(sketch, "E268.7.2.1", {"start": v(-8.98, -101.71) * mm, "end": v(-8.98, -106.8) * mm});
            skLineSegment(sketch, "E268.7.2.2", {"start": v(-14.06, -101.71) * mm, "end": v(-14.06, -106.8) * mm});
            skLineSegment(sketch, "E268.7.2.3", {"start": v(-14.06, -101.71) * mm, "end": v(-8.98, -101.71) * mm});
            skLineSegment(sketch, "E268.8.0.0", {"start": v(-6.44, -91.55) * mm, "end": v(-1.36, -91.55) * mm});
            skLineSegment(sketch, "E268.8.0.1", {"start": v(-1.36, -86.47) * mm, "end": v(-1.36, -91.55) * mm});
            skLineSegment(sketch, "E268.8.0.2", {"start": v(-6.44, -86.47) * mm, "end": v(-6.44, -91.55) * mm});
            skLineSegment(sketch, "E268.8.0.3", {"start": v(-6.44, -86.47) * mm, "end": v(-1.36, -86.47) * mm});
            skLineSegment(sketch, "E268.8.1.0", {"start": v(-6.44, -99.17) * mm, "end": v(-1.36, -99.17) * mm});
            skLineSegment(sketch, "E268.8.1.1", {"start": v(-1.36, -94.1) * mm, "end": v(-1.36, -99.17) * mm});
            skLineSegment(sketch, "E268.8.1.2", {"start": v(-6.44, -94.1) * mm, "end": v(-6.44, -99.17) * mm});
            skLineSegment(sketch, "E268.8.1.3", {"start": v(-6.44, -94.1) * mm, "end": v(-1.36, -94.1) * mm});
            skLineSegment(sketch, "E268.8.2.0", {"start": v(-6.44, -106.8) * mm, "end": v(-1.36, -106.8) * mm});
            skLineSegment(sketch, "E268.8.2.1", {"start": v(-1.36, -101.71) * mm, "end": v(-1.36, -106.8) * mm});
            skLineSegment(sketch, "E268.8.2.2", {"start": v(-6.44, -101.71) * mm, "end": v(-6.44, -106.8) * mm});
            skLineSegment(sketch, "E268.8.2.3", {"start": v(-6.44, -101.71) * mm, "end": v(-1.36, -101.71) * mm});
            skLineSegment(sketch, "E268.9.0.0", {"start": v(1.18, -91.55) * mm, "end": v(6.26, -91.55) * mm});
            skLineSegment(sketch, "E268.9.0.1", {"start": v(6.26, -86.47) * mm, "end": v(6.26, -91.55) * mm});
            skLineSegment(sketch, "E268.9.0.2", {"start": v(1.18, -86.47) * mm, "end": v(1.18, -91.55) * mm});
            skLineSegment(sketch, "E268.9.0.3", {"start": v(1.18, -86.47) * mm, "end": v(6.26, -86.47) * mm});
            skLineSegment(sketch, "E268.9.1.0", {"start": v(1.18, -99.17) * mm, "end": v(6.26, -99.17) * mm});
            skLineSegment(sketch, "E268.9.1.1", {"start": v(6.26, -94.1) * mm, "end": v(6.26, -99.17) * mm});
            skLineSegment(sketch, "E268.9.1.2", {"start": v(1.18, -94.1) * mm, "end": v(1.18, -99.17) * mm});
            skLineSegment(sketch, "E268.9.1.3", {"start": v(1.18, -94.1) * mm, "end": v(6.26, -94.1) * mm});
            skLineSegment(sketch, "E268.9.2.0", {"start": v(1.18, -106.8) * mm, "end": v(6.26, -106.8) * mm});
            skLineSegment(sketch, "E268.9.2.1", {"start": v(6.26, -101.71) * mm, "end": v(6.26, -106.8) * mm});
            skLineSegment(sketch, "E268.9.2.2", {"start": v(1.18, -101.71) * mm, "end": v(1.18, -106.8) * mm});
            skLineSegment(sketch, "E268.9.2.3", {"start": v(1.18, -101.71) * mm, "end": v(6.26, -101.71) * mm});
            skLineSegment(sketch, "E268.10.0.0", {"start": v(8.8, -91.55) * mm, "end": v(13.88, -91.55) * mm});
            skLineSegment(sketch, "E268.10.0.1", {"start": v(13.88, -86.47) * mm, "end": v(13.88, -91.55) * mm});
            skLineSegment(sketch, "E268.10.0.2", {"start": v(8.8, -86.47) * mm, "end": v(8.8, -91.55) * mm});
            skLineSegment(sketch, "E268.10.0.3", {"start": v(8.8, -86.47) * mm, "end": v(13.88, -86.47) * mm});
            skLineSegment(sketch, "E268.10.1.0", {"start": v(8.8, -99.17) * mm, "end": v(13.88, -99.17) * mm});
            skLineSegment(sketch, "E268.10.1.1", {"start": v(13.88, -94.1) * mm, "end": v(13.88, -99.17) * mm});
            skLineSegment(sketch, "E268.10.1.2", {"start": v(8.8, -94.1) * mm, "end": v(8.8, -99.17) * mm});
            skLineSegment(sketch, "E268.10.1.3", {"start": v(8.8, -94.1) * mm, "end": v(13.88, -94.1) * mm});
            skLineSegment(sketch, "E268.10.2.0", {"start": v(8.8, -106.8) * mm, "end": v(13.88, -106.8) * mm});
            skLineSegment(sketch, "E268.10.2.1", {"start": v(13.88, -101.71) * mm, "end": v(13.88, -106.8) * mm});
            skLineSegment(sketch, "E268.10.2.2", {"start": v(8.8, -101.71) * mm, "end": v(8.8, -106.8) * mm});
            skLineSegment(sketch, "E268.10.2.3", {"start": v(8.8, -101.71) * mm, "end": v(13.88, -101.71) * mm});
            skLineSegment(sketch, "E268.11.0.0", {"start": v(16.42, -91.55) * mm, "end": v(21.5, -91.55) * mm});
            skLineSegment(sketch, "E268.11.0.1", {"start": v(21.5, -86.47) * mm, "end": v(21.5, -91.55) * mm});
            skLineSegment(sketch, "E268.11.0.2", {"start": v(16.42, -86.47) * mm, "end": v(16.42, -91.55) * mm});
            skLineSegment(sketch, "E268.11.0.3", {"start": v(16.42, -86.47) * mm, "end": v(21.5, -86.47) * mm});
            skLineSegment(sketch, "E268.11.1.0", {"start": v(16.42, -99.17) * mm, "end": v(21.5, -99.17) * mm});
            skLineSegment(sketch, "E268.11.1.1", {"start": v(21.5, -94.1) * mm, "end": v(21.5, -99.17) * mm});
            skLineSegment(sketch, "E268.11.1.2", {"start": v(16.42, -94.1) * mm, "end": v(16.42, -99.17) * mm});
            skLineSegment(sketch, "E268.11.1.3", {"start": v(16.42, -94.1) * mm, "end": v(21.5, -94.1) * mm});
            skLineSegment(sketch, "E268.11.2.0", {"start": v(16.42, -106.8) * mm, "end": v(21.5, -106.8) * mm});
            skLineSegment(sketch, "E268.11.2.1", {"start": v(21.5, -101.71) * mm, "end": v(21.5, -106.8) * mm});
            skLineSegment(sketch, "E268.11.2.2", {"start": v(16.42, -101.71) * mm, "end": v(16.42, -106.8) * mm});
            skLineSegment(sketch, "E268.11.2.3", {"start": v(16.42, -101.71) * mm, "end": v(21.5, -101.71) * mm});
            skLineSegment(sketch, "E268.12.0.0", {"start": v(24.04, -91.55) * mm, "end": v(29.12, -91.55) * mm});
            skLineSegment(sketch, "E268.12.0.1", {"start": v(29.12, -86.47) * mm, "end": v(29.12, -91.55) * mm});
            skLineSegment(sketch, "E268.12.0.2", {"start": v(24.04, -86.47) * mm, "end": v(24.04, -91.55) * mm});
            skLineSegment(sketch, "E268.12.0.3", {"start": v(24.04, -86.47) * mm, "end": v(29.12, -86.47) * mm});
            skLineSegment(sketch, "E268.12.1.0", {"start": v(24.04, -99.17) * mm, "end": v(29.12, -99.17) * mm});
            skLineSegment(sketch, "E268.12.1.1", {"start": v(29.12, -94.1) * mm, "end": v(29.12, -99.17) * mm});
            skLineSegment(sketch, "E268.12.1.2", {"start": v(24.04, -94.1) * mm, "end": v(24.04, -99.17) * mm});
            skLineSegment(sketch, "E268.12.1.3", {"start": v(24.04, -94.1) * mm, "end": v(29.12, -94.1) * mm});
            skLineSegment(sketch, "E268.12.2.0", {"start": v(24.04, -106.8) * mm, "end": v(29.12, -106.8) * mm});
            skLineSegment(sketch, "E268.12.2.1", {"start": v(29.12, -101.71) * mm, "end": v(29.12, -106.8) * mm});
            skLineSegment(sketch, "E268.12.2.2", {"start": v(24.04, -101.71) * mm, "end": v(24.04, -106.8) * mm});
            skLineSegment(sketch, "E268.12.2.3", {"start": v(24.04, -101.71) * mm, "end": v(29.12, -101.71) * mm});
            skLineSegment(sketch, "E268.13.0.0", {"start": v(31.66, -91.55) * mm, "end": v(36.74, -91.55) * mm});
            skLineSegment(sketch, "E268.13.0.1", {"start": v(36.74, -86.47) * mm, "end": v(36.74, -91.55) * mm});
            skLineSegment(sketch, "E268.13.0.2", {"start": v(31.66, -86.47) * mm, "end": v(31.66, -91.55) * mm});
            skLineSegment(sketch, "E268.13.0.3", {"start": v(31.66, -86.47) * mm, "end": v(36.74, -86.47) * mm});
            skLineSegment(sketch, "E268.13.1.0", {"start": v(31.66, -99.17) * mm, "end": v(36.74, -99.17) * mm});
            skLineSegment(sketch, "E268.13.1.1", {"start": v(36.74, -94.1) * mm, "end": v(36.74, -99.17) * mm});
            skLineSegment(sketch, "E268.13.1.2", {"start": v(31.66, -94.1) * mm, "end": v(31.66, -99.17) * mm});
            skLineSegment(sketch, "E268.13.1.3", {"start": v(31.66, -94.1) * mm, "end": v(36.74, -94.1) * mm});
            skLineSegment(sketch, "E268.13.2.0", {"start": v(31.66, -106.8) * mm, "end": v(36.74, -106.8) * mm});
            skLineSegment(sketch, "E268.13.2.1", {"start": v(36.74, -101.71) * mm, "end": v(36.74, -106.8) * mm});
            skLineSegment(sketch, "E268.13.2.2", {"start": v(31.66, -101.71) * mm, "end": v(31.66, -106.8) * mm});
            skLineSegment(sketch, "E268.13.2.3", {"start": v(31.66, -101.71) * mm, "end": v(36.74, -101.71) * mm});
            skLineSegment(sketch, "E268.14.0.0", {"start": v(39.28, -91.55) * mm, "end": v(44.36, -91.55) * mm});
            skLineSegment(sketch, "E268.14.0.1", {"start": v(44.36, -86.47) * mm, "end": v(44.36, -91.55) * mm});
            skLineSegment(sketch, "E268.14.0.2", {"start": v(39.28, -86.47) * mm, "end": v(39.28, -91.55) * mm});
            skLineSegment(sketch, "E268.14.0.3", {"start": v(39.28, -86.47) * mm, "end": v(44.36, -86.47) * mm});
            skLineSegment(sketch, "E268.14.1.0", {"start": v(39.28, -99.17) * mm, "end": v(44.36, -99.17) * mm});
            skLineSegment(sketch, "E268.14.1.1", {"start": v(44.36, -94.1) * mm, "end": v(44.36, -99.17) * mm});
            skLineSegment(sketch, "E268.14.1.2", {"start": v(39.28, -94.1) * mm, "end": v(39.28, -99.17) * mm});
            skLineSegment(sketch, "E268.14.1.3", {"start": v(39.28, -94.1) * mm, "end": v(44.36, -94.1) * mm});
            skLineSegment(sketch, "E268.15.0.0", {"start": v(46.9, -91.55) * mm, "end": v(51.98, -91.55) * mm});
            skLineSegment(sketch, "E268.15.0.1", {"start": v(51.98, -86.47) * mm, "end": v(51.98, -91.55) * mm});
            skLineSegment(sketch, "E268.15.0.2", {"start": v(46.9, -86.47) * mm, "end": v(46.9, -91.55) * mm});
            skLineSegment(sketch, "E268.15.0.3", {"start": v(46.9, -86.47) * mm, "end": v(51.98, -86.47) * mm});
            skLineSegment(sketch, "E268.15.1.0", {"start": v(46.9, -99.17) * mm, "end": v(51.98, -99.17) * mm});
            skLineSegment(sketch, "E268.15.1.1", {"start": v(51.98, -94.1) * mm, "end": v(51.98, -99.17) * mm});
            skLineSegment(sketch, "E268.15.1.2", {"start": v(46.9, -94.1) * mm, "end": v(46.9, -99.17) * mm});
            skLineSegment(sketch, "E268.15.1.3", {"start": v(46.9, -94.1) * mm, "end": v(51.98, -94.1) * mm});
            skLineSegment(sketch, "E268.16.0.0", {"start": v(54.52, -91.55) * mm, "end": v(59.6, -91.55) * mm});
            skLineSegment(sketch, "E268.16.0.1", {"start": v(59.6, -86.47) * mm, "end": v(59.6, -91.55) * mm});
            skLineSegment(sketch, "E268.16.0.2", {"start": v(54.52, -86.47) * mm, "end": v(54.52, -91.55) * mm});
            skLineSegment(sketch, "E268.16.0.3", {"start": v(54.52, -86.47) * mm, "end": v(59.6, -86.47) * mm});
            skLineSegment(sketch, "E268.17.0.0", {"start": v(62.14, -91.55) * mm, "end": v(67.22, -91.55) * mm});
            skLineSegment(sketch, "E268.17.0.1", {"start": v(67.22, -86.47) * mm, "end": v(67.22, -91.55) * mm});
            skLineSegment(sketch, "E268.17.0.2", {"start": v(62.14, -86.47) * mm, "end": v(62.14, -91.55) * mm});
            skLineSegment(sketch, "E268.17.0.3", {"start": v(62.14, -86.47) * mm, "end": v(67.22, -86.47) * mm});
            skLineSegment(sketch, "E268.direction1", {"start": v(-67.4, -91.55) * mm, "end": v(-59.78, -91.55) * mm, "construction": true});
            skSolve(sketch);
        }
        {
            var Q0;
            Q0 = qSketchRegion(id + "F6", true);
            extrude(context, id + "F7", {"entities" : qUnion([Q0]), "operationType" : NewBodyOperationType.REMOVE, "oppositeDirection" : true, "depth" : 25.4 * mm});
        }
    });
